FCSTD DOCUMENT  (FreeCAD 0.19R24267 +99 (Git))
Label: Pedals
License: All rights reserved
LicenseURL: http://en.wikipedia.org/wiki/All_rights_reserved
objects: Part::Feature×135, TechDraw::DrawViewDimension×109, TechDraw::DrawProjGroupItem×35, Sketcher::SketchObject×29, PartDesign::Body×19, PartDesign::Pad×16, TechDraw::DrawProjGroup×16, PartDesign::Pocket×13, TechDraw::DrawViewAnnotation×13, Part::FeaturePython×11, TechDraw::DrawSVGTemplate×7, TechDraw::DrawPage×7, App::Part×6, PartDesign::Draft×3, PartDesign::FeatureBase×3, PartDesign::Chamfer×2, TechDraw::DrawViewSection×2, App::DocumentObjectGroup×2, PartDesign::Thickness×1, TechDraw::DrawViewDetail×1
note: 267 computed .brp shape members not serialized (recipe doc carries the construction recipe); baked Part::Feature solids carry a one-line shape summary decoded from their .brp

FEATURE [Sketcher::SketchObject] Sketch
  FullyConstrained = true
  MapMode = 5
  Support = -> [XY_Plane008]
  sketch-geometry (12):
    g0: LineSegment StartX=-14 StartY=10 StartZ=0 EndX=14 EndY=10 EndZ=0
    g1: LineSegment StartX=14 StartY=10 StartZ=0 EndX=14 EndY=-10 EndZ=0
    g2: LineSegment StartX=14 StartY=-10 StartZ=0 EndX=-14 EndY=-10 EndZ=0
    g3: LineSegment StartX=-14 StartY=-10 StartZ=0 EndX=-14 EndY=10 EndZ=0
    g4: LineSegment StartX=-13 StartY=9 StartZ=0 EndX=13 EndY=9 EndZ=0
    g5: LineSegment StartX=13 StartY=9 StartZ=0 EndX=13 EndY=-9 EndZ=0
    g6: LineSegment StartX=13 StartY=-9 StartZ=0 EndX=-13 EndY=-9 EndZ=0
    g7: LineSegment StartX=-13 StartY=-9 StartZ=0 EndX=-13 EndY=9 EndZ=0
    g8: LineSegment StartX=-13 StartY=10 StartZ=0 EndX=-13 EndY=-9 EndZ=0
    g9: LineSegment StartX=13 StartY=10 StartZ=0 EndX=13 EndY=-9 EndZ=0
    g10: LineSegment StartX=-14 StartY=10 StartZ=0 EndX=-13 EndY=10 EndZ=0
    g11: LineSegment StartX=13 StartY=10 StartZ=0 EndX=14 EndY=10 EndZ=0
  constraints (32):
    c: Coincident(g0,g1)
    c: Coincident(g1,g2)
    c: Coincident(g2,g3)
    c: Coincident(g3,g0)
    c: Horizontal(g0)
    c: Horizontal(g2)
    c: Vertical(g1)
    c: Vertical(g3)
    c: Symmetric(g0,g2,g-1)
    c: DistanceY(g3,g3) = 20
    c: DistanceX(g2,g2) = 28
    c: Coincident(g4,g5)
    c: Coincident(g5,g6)
    c: Coincident(g6,g7)
    c: Coincident(g7,g4)
    c: Horizontal(g4)
    c: Horizontal(g6)
    c: Vertical(g5)
    c: Vertical(g7)
    c: DistanceY(g4,g3) = 1
    c: DistanceX(g3,g4) = 1
    c: Symmetric(g4,g6,g-1)
    c: PointOnObject(g8,g0)
    c: Coincident(g8,g6)
    c: Vertical(g8)
    c: PointOnObject(g9,g0)
    c: Coincident(g9,g5)
    c: Vertical(g9)
    c: Coincident(g10,g3)
    c: Coincident(g10,g8)
    c: Coincident(g11,g9)
    c: Coincident(g11,g1)
FEATURE [PartDesign::Pad] Pad
  Direction = (1,1,1)
  Length = 180
  Length2 = 100
  Profile = -> Sketch
  Type = 0
FEATURE [Sketcher::SketchObject] Sketch001
  FullyConstrained = true
  MapMode = 5
  Support = -> [XY_Plane009]
  sketch-geometry (12):
    g0: LineSegment StartX=-15 StartY=10 StartZ=0 EndX=15 EndY=10 EndZ=0
    g1: LineSegment StartX=15 StartY=10 StartZ=0 EndX=15 EndY=-10 EndZ=0
    g2: LineSegment StartX=15 StartY=-10 StartZ=0 EndX=-15 EndY=-10 EndZ=0
    g3: LineSegment StartX=-15 StartY=-10 StartZ=0 EndX=-15 EndY=10 EndZ=0
    g4: LineSegment StartX=-14 StartY=9 StartZ=0 EndX=14 EndY=9 EndZ=0
    g5: LineSegment StartX=14 StartY=9 StartZ=0 EndX=14 EndY=-9 EndZ=0
    g6: LineSegment StartX=14 StartY=-9 StartZ=0 EndX=-14 EndY=-9 EndZ=0
    g7: LineSegment StartX=-14 StartY=-9 StartZ=0 EndX=-14 EndY=9 EndZ=0
    g8: LineSegment StartX=-14 StartY=10 StartZ=0 EndX=-14 EndY=-9 EndZ=0
    g9: LineSegment StartX=14 StartY=10 StartZ=0 EndX=14 EndY=-9 EndZ=0
    g10: LineSegment StartX=-15 StartY=10 StartZ=0 EndX=-14 EndY=10 EndZ=0
    g11: LineSegment StartX=14 StartY=10 StartZ=0 EndX=15 EndY=10 EndZ=0
  constraints (32):
    c: Coincident(g0,g1)
    c: Coincident(g1,g2)
    c: Coincident(g2,g3)
    c: Coincident(g3,g0)
    c: Horizontal(g0)
    c: Horizontal(g2)
    c: Vertical(g1)
    c: Vertical(g3)
    c: Symmetric(g0,g2,g-1)
    c: DistanceY(g3,g3) = 20
    c: DistanceX(g2,g2) = 30
    c: Coincident(g4,g5)
    c: Coincident(g5,g6)
    c: Coincident(g6,g7)
    c: Coincident(g7,g4)
    c: Horizontal(g4)
    c: Horizontal(g6)
    c: Vertical(g5)
    c: Vertical(g7)
    c: DistanceY(g4,g3) = 1
    c: DistanceX(g3,g4) = 1
    c: Symmetric(g4,g6,g-1)
    c: PointOnObject(g8,g0)
    c: Coincident(g8,g6)
    c: Vertical(g8)
    c: PointOnObject(g9,g0)
    c: Coincident(g9,g5)
    c: Vertical(g9)
    c: Coincident(g10,g3)
    c: Coincident(g10,g8)
    c: Coincident(g11,g9)
    c: Coincident(g11,g1)
FEATURE [PartDesign::Pad] Pad001
  Direction = (1,1,1)
  Length = 240
  Length2 = 100
  Offset = -10
  Profile = -> Sketch001
  Type = 0
FEATURE [Sketcher::SketchObject] Sketch002
  ExternalGeometry = -> [Pad001]
  FullyConstrained = true
  MapMode = 5
  Placement = pos=(15,0,0) rot=(0.57735,0.57735,0.57735;2.0944rad)
  Support = -> [Pad001]
  sketch-geometry (3):
    g0: LineSegment StartX=0 StartY=240 StartZ=0 EndX=0 EndY=0 EndZ=0
    g1: Circle CenterX=0 CenterY=190 CenterZ=0 NormalX=0 NormalY=0 NormalZ=1 AngleXU=0 Radius=3
    g2: Circle CenterX=4e-16 CenterY=25 CenterZ=0 NormalX=0 NormalY=0 NormalZ=1 AngleXU=0 Radius=3
  constraints (10):
    c: PointOnObject(g0,g-4)
    c: Coincident(g0,g-1)
    c: Vertical(g0)
    c: PointOnObject(g1,g0)
    c: Diameter(g1) = 6
    c: Distance(g1,g0) = 50
    c: Distance(g-4) = 20
    c: Diameter(g2) = 6
    c: Distance(g2,g1) = 165
    c: Distance(g2,g-5) = 10
FEATURE [PartDesign::Pocket] Pocket
  BaseFeature = -> Pad001
  Length = 5
  Length2 = 100
  Profile = -> Sketch002
  Type = 1
FEATURE [Sketcher::SketchObject] Sketch003
  ExternalGeometry = -> [Pad]
  FullyConstrained = false
  MapMode = 5
  Placement = pos=(14,0,0) rot=(0.57735,0.57735,0.57735;2.0944rad)
  Support = -> [Pad]
  sketch-geometry (8):
    g0: LineSegment StartX=0 StartY=180 StartZ=0 EndX=0 EndY=0 EndZ=0
    g1: Circle CenterX=0 CenterY=10 CenterZ=0 NormalX=0 NormalY=0 NormalZ=1 AngleXU=0 Radius=3
    g2: Circle CenterX=4e-16 CenterY=80 CenterZ=0 NormalX=0 NormalY=0 NormalZ=1 AngleXU=0 Radius=3
    g3: LineSegment StartX=4e-16 StartY=80 StartZ=0 EndX=4e-16 EndY=120.768 EndZ=0
    g4: Circle CenterX=4e-16 CenterY=90 CenterZ=0 NormalX=0 NormalY=0 NormalZ=1 AngleXU=0 Radius=3
    g5: Circle CenterX=4e-16 CenterY=100 CenterZ=0 NormalX=0 NormalY=0 NormalZ=1 AngleXU=0 Radius=3
    g6: Circle CenterX=4e-16 CenterY=110 CenterZ=0 NormalX=0 NormalY=0 NormalZ=1 AngleXU=0 Radius=3
    g7: Circle CenterX=0 CenterY=60 CenterZ=0 NormalX=0 NormalY=0 NormalZ=1 AngleXU=0 Radius=2
  constraints (23):
    c: PointOnObject(g0,g-5)
    c: Coincident(g0,g-1)
    c: Vertical(g0)
    c: PointOnObject(g1,g0)
    c: Diameter(g1) = 6
    c: DistanceY(g-1,g1) = 10
    c: Diameter(g2) = 6
    c: Distance(g2,g-4) = 10
    c: DistanceY(g1,g2) = 70
    c: Coincident(g3,g2)
    c: Vertical(g3)
    c: PointOnObject(g4,g3)
    c: Equal(g4,g5)
    c: Equal(g5,g2)
    c: DistanceY(g2,g4) = 10
    c: DistanceY(g4,g5) = 10
    c: PointOnObject(g5,g3)
    c: PointOnObject(g6,g3)
    c: DistanceY(g5,g6) = 10
    c: Equal(g6,g5)
    c: PointOnObject(g7,g0)
    c: Diameter(g7) = 4
    c: DistanceY(g-6,g7) = 60
FEATURE [PartDesign::Pocket] Pocket001
  BaseFeature = -> Pad
  Length = 5
  Length2 = 100
  Profile = -> Sketch003
  Type = 1
FEATURE [Sketcher::SketchObject] Sketch005
  FullyConstrained = true
  MapMode = 5
  Support = -> [XY_Plane010]
  sketch-geometry (12):
    g0: LineSegment StartX=-14 StartY=12.5 StartZ=0 EndX=14 EndY=12.5 EndZ=0
    g1: LineSegment StartX=14 StartY=12.5 StartZ=0 EndX=14 EndY=-12.5 EndZ=0
    g2: LineSegment StartX=14 StartY=-12.5 StartZ=0 EndX=-14 EndY=-12.5 EndZ=0
    g3: LineSegment StartX=-14 StartY=-12.5 StartZ=0 EndX=-14 EndY=12.5 EndZ=0
    g4: LineSegment StartX=-13 StartY=11.5 StartZ=0 EndX=13 EndY=11.5 EndZ=0
    g5: LineSegment StartX=13 StartY=11.5 StartZ=0 EndX=13 EndY=-11.5 EndZ=0
    g6: LineSegment StartX=13 StartY=-11.5 StartZ=0 EndX=-13 EndY=-11.5 EndZ=0
    g7: LineSegment StartX=-13 StartY=-11.5 StartZ=0 EndX=-13 EndY=11.5 EndZ=0
    g8: LineSegment StartX=-13 StartY=12.5 StartZ=0 EndX=-13 EndY=-11.5 EndZ=0
    g9: LineSegment StartX=13 StartY=12.5 StartZ=0 EndX=13 EndY=-11.5 EndZ=0
    g10: LineSegment StartX=-14 StartY=12.5 StartZ=0 EndX=-13 EndY=12.5 EndZ=0
    g11: LineSegment StartX=13 StartY=12.5 StartZ=0 EndX=14 EndY=12.5 EndZ=0
  constraints (32):
    c: Coincident(g0,g1)
    c: Coincident(g1,g2)
    c: Coincident(g2,g3)
    c: Coincident(g3,g0)
    c: Horizontal(g0)
    c: Horizontal(g2)
    c: Vertical(g1)
    c: Vertical(g3)
    c: Symmetric(g0,g2,g-1)
    c: DistanceY(g3,g3) = 25
    c: DistanceX(g2,g2) = 28
    c: Coincident(g4,g5)
    c: Coincident(g5,g6)
    c: Coincident(g6,g7)
    c: Coincident(g7,g4)
    c: Horizontal(g4)
    c: Horizontal(g6)
    c: Vertical(g5)
    c: Vertical(g7)
    c: DistanceY(g4,g3) = 1
    c: DistanceX(g3,g4) = 1
    c: Symmetric(g4,g6,g-1)
    c: PointOnObject(g8,g0)
    c: Coincident(g8,g6)
    c: Vertical(g8)
    c: PointOnObject(g9,g0)
    c: Coincident(g9,g5)
    c: Vertical(g9)
    c: Coincident(g10,g3)
    c: Coincident(g10,g8)
    c: Coincident(g11,g9)
    c: Coincident(g11,g1)
FEATURE [PartDesign::Pad] Pad002
  Direction = (1,1,1)
  Length = 50
  Length2 = 100
  Profile = -> Sketch005
  Type = 0
FEATURE [PartDesign::Draft] Draft
  Angle = 15
  Base = -> Pad002 [Face9]
  BaseFeature = -> Pad002
  SupportTransform = false
FEATURE [Sketcher::SketchObject] Sketch006
  FullyConstrained = true
  MapMode = 5
  Placement = pos=(14,0,0) rot=(0.57735,0.57735,0.57735;2.0944rad)
  Support = -> [Draft]
  sketch-geometry (1):
    g0: Circle CenterX=0 CenterY=12 CenterZ=0 NormalX=0 NormalY=0 NormalZ=1 AngleXU=0 Radius=3
  constraints (3):
    c: PointOnObject(g0,g-2)
    c: Diameter(g0) = 6
    c: Distance(g-1,g0) = 12
FEATURE [PartDesign::Pocket] Pocket002
  BaseFeature = -> Draft
  Length = 5
  Length2 = 100
  Profile = -> Sketch006
  Type = 1
FEATURE [PartDesign::Body] _______________________003  label="Упор пружины"
  Group = -> [Sketch005,Pad002,Draft,Sketch006,Pocket002]
  Origin = -> Origin010
  Placement = pos=(0,-13.1352,-2.8136) rot=(-1,0,0;0.523599rad)
  Tip = -> Pocket002
FEATURE [Part::Feature] Part__Feature069  label="01 - Pied"
  Placement = pos=(142.918,-74.3145,196.645) rot=(0,0,1;0rad)
  shape: bbox 314.5 x 48 x 7.5 mm, 33 faces (baked)
FEATURE [Part::Feature] Part__Feature070  label="02 - Pied SYM"
  Placement = pos=(142.918,-74.3145,-127.355) rot=(0,0,1;0rad)
  shape: bbox 314.5 x 48 x 7.5 mm, 33 faces (baked)
FEATURE [Part::Feature] Part__Feature071  label="03 - Equerre fixation sol"
  Placement = pos=(267.668,181.146,167.895) rot=(1,0,0;1.5708rad)
  shape: bbox 65 x 37.5 x 50 mm, 100 faces, 2 solids (baked)
FEATURE [Part::Feature] Part__Feature072  label="04 - Equerre fixation sol SYM"
  Placement = pos=(267.668,181.146,-56.1054) rot=(1,0,0;1.5708rad)
  shape: bbox 65 x 37.5 x 50 mm, 100 faces, 2 solids (baked)
FEATURE [Part::Feature] Part__Feature073  label="05 - Equerre fixation sol 2"
  Placement = pos=(19.4178,179.899,167.895) rot=(1,0,0;1.5708rad)
  shape: bbox 65 x 27 x 50 mm, 97 faces, 2 solids (baked)
FEATURE [Part::Feature] Part__Feature074  label="06 - Equerre fixation sol 2 SYM"
  Placement = pos=(19.4178,179.899,-56.1054) rot=(1,0,0;1.5708rad)
  shape: bbox 65 x 27 x 50 mm, 97 faces, 2 solids (baked)
FEATURE [Part::Feature] Part__Feature075  label="07 - Axe court"
  Placement = pos=(288.168,200.646,30.8946) rot=(0,0,1;0rad)
  shape: bbox 17.32 x 17.32 x 316 mm, 29 faces (baked)
FEATURE [Part::Feature] Part__Feature076  label="07 - Axe court001"
  Placement = pos=(25.9178,189.899,30.8946) rot=(0,0,1;0rad)
  shape: bbox 17.32 x 17.32 x 316 mm, 29 faces (baked)
FEATURE [Part::Feature] Part__Feature077  label="08 - Axe long"
  Placement = pos=(130.86,215.417,30.8946) rot=(0,0,1;0rad)
  shape: bbox 17.32 x 17.32 x 324 mm, 29 faces (baked)
FEATURE [Part::Feature] Part__Feature078  label="09 - Levier pedales A-E"
  Placement = pos=(178.538,257.451,148.595) rot=(-0.810568,-0.414113,0.414113;1.77929rad)
  shape: bbox 94.99 x 131.6 x 40 mm, 76 faces (baked)
FEATURE [Part::Feature] Part__Feature079  label="10 - Levier pedales F"
  Placement = pos=(178.562,257.423,34.9946) rot=(-0.810765,-0.41392,0.41392;1.77905rad)
  shape: bbox 95.05 x 131.5 x 40 mm, 78 faces (baked)
FEATURE [Part::Feature] Part__Feature080  label="09 - Levier pedales A-E001"
  Placement = pos=(178.485,257.51,-86.3054) rot=(-0.810139,-0.414533,0.414533;1.77981rad)
  shape: bbox 94.85 x 131.7 x 40 mm, 76 faces (baked)
FEATURE [Part::Feature] Part__Feature081  label="11 - Palier bronze"
  Placement = pos=(130.86,215.417,14.1946) rot=(-0.439546,-0.783326,-0.439546;1.81261rad)
  shape: bbox 24 x 24 x 8.6 mm, 9 faces (baked)
FEATURE [Part::Feature] Part__Feature082  label="11 - Palier bronze001"
  Placement = pos=(130.86,215.417,55.7946) rot=(0.439546,0.783326,-0.439546;1.81261rad)
  shape: bbox 24 x 24 x 8.6 mm, 9 faces (baked)
FEATURE [Part::Feature] Part__Feature083  label="11 - Palier bronze002"
  Placement = pos=(130.86,215.417,127.795) rot=(-0.423866,-0.800422,-0.423866;1.7916rad)
  shape: bbox 24 x 24 x 8.6 mm, 9 faces (baked)
FEATURE [Part::Feature] Part__Feature084  label="11 - Palier bronze003"
  Placement = pos=(130.86,215.417,169.395) rot=(0.423866,0.800422,-0.423866;1.7916rad)
  shape: bbox 24 x 24 x 8.6 mm, 9 faces (baked)
FEATURE [Part::Feature] Part__Feature085  label="11 - Palier bronze004"
  Placement = pos=(130.86,215.417,-107.105) rot=(0.078533,-0.993814,0.078533;1.577rad)
  shape: bbox 24 x 24 x 8.6 mm, 9 faces (baked)
FEATURE [Part::Feature] Part__Feature086  label="11 - Palier bronze005"
  Placement = pos=(130.86,215.417,-65.5054) rot=(-0.078533,0.993814,0.078533;1.577rad)
  shape: bbox 24 x 24 x 8.6 mm, 9 faces (baked)
FEATURE [Part::Feature] Part__Feature087  label="12 - Pivot suspension"
  Placement = pos=(175.936,282.783,11.9946) rot=(0.308259,0.951303,0;3.14159rad)
  shape: bbox 11.55 x 11.55 x 20.5 mm, 28 faces (baked)
FEATURE [Part::Feature] Part__Feature088  label="13 - Ecrou suspension"
  Placement = pos=(175.936,282.783,-2.00541) rot=(0,0,1;0rad)
  shape: bbox 11 x 11 x 4.5 mm, 10 faces (baked)
FEATURE [Part::Feature] Part__Feature089  label="14 - Amortisseur"
  Placement = pos=(270.501,227.576,5.49459) rot=(0.252673,0.933977,-0.252673;1.63905rad)
  shape: bbox 118.3 x 72.79 x 31.6 mm, 228 faces, 4 solids (baked)
FEATURE [Part::Feature] Part__Feature090  label="15 - Pivot levier"
  Placement = pos=(159.004,251.963,34.9946) rot=(0,0,1;1.19261rad)
  shape: bbox 22.9 x 24.48 x 31.5 mm, 28 faces (baked)
FEATURE [Part::Feature] Part__Feature091  label="16 - Coulisseau frein"
  Placement = pos=(224.058,226.117,34.9946) rot=(-0.054456,0.010422,-0.998462;0.378751rad)
  shape: bbox 68.35 x 35.6 x 12.99 mm, 11 faces (baked)
FEATURE [Part::Feature] Part__Feature092  label="17 - Axe nu"
  Placement = pos=(154.822,253.625,34.9946) rot=(0,0,-1;0.378182rad)
  shape: bbox 8.047 x 8.047 x 40 mm, 8 faces (baked)
FEATURE [Part::Feature] Part__Feature093  label="18 - Vibreur"
  Placement = pos=(189.956,293.62,34.9946) rot=(-0.665096,-0.339551,0.665096;3.79627rad)
  shape: bbox 30.23 x 46.77 x 28 mm, 137 faces, 6 solids (baked)
FEATURE [Part::Feature] Part__Feature094  label="15 - Pivot levier001"
  Placement = pos=(158.736,251.576,-86.3054) rot=(0,0,1;1.08724rad)
  shape: bbox 23.66 x 24.93 x 31.5 mm, 28 faces (baked)
FEATURE [Part::Feature] Part__Feature095  label="19 - Axe capteur"
  Placement = pos=(154.752,253.668,-86.3054) rot=(-0.15035,0.988633,0;3.14159rad)
  shape: bbox 8.63 x 8.268 x 40 mm, 18 faces, 2 solids (baked)
FEATURE [Part::Feature] Part__Feature096  label="20 - Coulisseau embrayage"
  Placement = pos=(234.876,211.592,-86.3054) rot=(0,0,-1;0.483554rad)
  shape: bbox 79.02 x 47.64 x 10.82 mm, 11 faces (baked)
FEATURE [Part::Feature] Part__Feature097  label="21 - Ressort embrayage"
  Placement = pos=(215.93,221.542,-86.3054) rot=(0,0,1;1.08724rad)
  shape: bbox 47.07 x 34.38 x 15.81 mm, 3 faces (baked)
FEATURE [Part::Feature] Part__Feature098  label="15 - Pivot levier002"
  Placement = pos=(179.773,280.728,-86.3054) rot=(-0.512361,0.85877,0;3.14159rad)
  shape: bbox 23.74 x 23.74 x 31.5 mm, 28 faces (baked)
FEATURE [Part::Feature] Part__Feature099  label="17 - Axe nu001"
  Placement = pos=(175.813,282.865,-86.3054) rot=(0,0,1;1.06237rad)
  shape: bbox 8.329 x 8.329 x 40 mm, 8 faces (baked)
FEATURE [Part::Feature] Part__Feature100  label="22 - Biellette embrayage"
  Placement = pos=(223.773,256.979,-86.3054) rot=(0,0,-1;0.494932rad)
  shape: bbox 91.8 x 55.35 x 10 mm, 28 faces (baked)
FEATURE [Part::Feature] Part__Feature101  label="24 - Guide coulisseau taraud澀"
  Placement = pos=(269.394,193.466,-86.3054) rot=(0,0,1;2.65804rad)
  shape: bbox 66.88 x 46.28 x 30 mm, 19 faces (baked)
FEATURE [Part::Feature] Part__Feature102  label="25 - Tampon embrayage"
  Placement = pos=(249.409,223.162,-86.3054) rot=(-0.650221,-0.392969,0.650221;3.89045rad)
  shape: bbox 38.38 x 29.13 x 18 mm, 16 faces (baked)
FEATURE [Part::Feature] Part__Feature103  label="26 - Axe 12mm"
  Placement = pos=(269.394,193.466,-86.3054) rot=(0,0,-1;0rad)
  shape: bbox 12 x 12 x 32 mm, 12 faces (baked)
FEATURE [Part::Feature] Part__Feature104  label="27 - Axe 8mm"
  Placement = pos=(271.733,231.093,-86.3054) rot=(0,0,-1;0rad)
  shape: bbox 8 x 8 x 52 mm, 14 faces (baked)
FEATURE [Part::Feature] Part__Feature105  label="28 - Pivot renvoi"
  Placement = pos=(288.168,200.646,-106.305) rot=(0,0,-1;1.55065rad)
  shape: bbox 38.57 x 52.92 x 4 mm, 15 faces (baked)
FEATURE [Part::Feature] Part__Feature106  label="28 - Pivot renvoi001"
  Placement = pos=(288.168,200.646,-70.3054) rot=(0,0,-1;1.55065rad)
  shape: bbox 38.57 x 52.92 x 4 mm, 15 faces (baked)
FEATURE [Part::Feature] Part__Feature107  label="11 - Palier bronze006"
  Placement = pos=(288.168,200.646,-107.105) rot=(-0.279247,-0.918718,-0.279247;1.65547rad)
  shape: bbox 24 x 24 x 8.6 mm, 9 faces (baked)
FEATURE [Part::Feature] Part__Feature108  label="11 - Palier bronze007"
  Placement = pos=(288.168,200.646,-65.5054) rot=(-0.327241,0.886469,0.327241;1.69101rad)
  shape: bbox 24 x 24 x 8.6 mm, 9 faces (baked)
FEATURE [Part::Feature] Part__Feature109  label="15 - Pivot levier003"
  Placement = pos=(267.773,233.231,-86.3054) rot=(0,0,-1;2.06573rad)
  shape: bbox 23.74 x 24.96 x 31.5 mm, 28 faces (baked)
FEATURE [Part::Feature] Part__Feature110  label="29 - Entretoise_20"
  Placement = pos=(288.168,200.646,-117.105) rot=(0,0,1;0rad)
  shape: bbox 20 x 20 x 20 mm, 6 faces (baked)
FEATURE [Part::Feature] Part__Feature111  label="29 - Entretoise_23.5"
  Placement = pos=(130.86,215.417,-119.355) rot=(0,0,1;0rad)
  shape: bbox 20 x 20 x 23.5 mm, 6 faces (baked)
FEATURE [Part::Feature] Part__Feature112  label="30 - Pousseur mousse"
  Placement = pos=(260.07,211.809,34.9946) rot=(-0.300774,-0.951003,-0.07162;1.57595rad)
  shape: bbox 25.55 x 19.19 x 12.11 mm, 8 faces (baked)
FEATURE [Part::Feature] Part__Feature113  label="31 - Mousse loadcell"
  Placement = pos=(236.604,221.132,34.9946) rot=(-0.353533,-0.935271,-0.01678;1.57108rad)
  shape: bbox 29.34 x 20.66 x 11.5 mm, 4 faces (baked)
FEATURE [Part::Feature] Part__Feature114  label="32 - Guide coulisseau frein"
  Placement = pos=(288.168,200.646,34.9946) rot=(0,0,1;2.76341rad)
  shape: bbox 109.8 x 58.06 x 41.6 mm, 35 faces (baked)
FEATURE [Part::Feature] Part__Feature115  label="33 - Entretoise pedale"
  Placement = pos=(197.009,334.183,148.595) rot=(-0.454956,0.890514,0;3.14159rad)
  shape: bbox 31.86 x 39.29 x 31.5 mm, 10 faces (baked)
FEATURE [Part::Feature] Part__Feature116  label="33 - Entretoise pedale001"
  Placement = pos=(197.077,334.145,34.9946) rot=(-0.454701,0.890644,0;3.14159rad)
  shape: bbox 31.87 x 39.29 x 31.5 mm, 10 faces (baked)
FEATURE [Part::Feature] Part__Feature117  label="33 - Entretoise pedale002"
  Placement = pos=(196.86,334.266,-86.3054) rot=(-0.455514,0.890229,0;3.14159rad)
  shape: bbox 31.83 x 39.31 x 31.5 mm, 10 faces (baked)
FEATURE [Part::Feature] Part__Feature118  label="34 - Patte suspension"
  Placement = pos=(209.515,208.042,0.494593) rot=(0,0,-1;0.09377rad)
  shape: bbox 179.3 x 36.8 x 12 mm, 37 faces, 3 solids (baked)
FEATURE [Part::Feature] Part__Feature119  label="29 - Entretoise_10"
  Placement = pos=(130.86,215.417,8.84459) rot=(0,0,1;0.052395rad)
  shape: bbox 20 x 20 x 10.7 mm, 6 faces (baked)
FEATURE [Part::Feature] Part__Feature120  label="29 - Entretoise_021"
  Placement = pos=(288.168,200.646,8.84459) rot=(0,0,1;2.89054rad)
  shape: bbox 20 x 20 x 10.7 mm, 6 faces (baked)
FEATURE [Part::Feature] Part__Feature121  label="29 - Entretoise_66"
  Placement = pos=(288.168,200.646,-32.5054) rot=(0,0,1;0rad)
  shape: bbox 20 x 20 x 66 mm, 6 faces (baked)
FEATURE [Part::Feature] Part__Feature122  label="29 - Entretoise_022"
  Placement = pos=(130.86,215.417,-32.5054) rot=(0,0,1;0rad)
  shape: bbox 20 x 20 x 66 mm, 6 faces (baked)
FEATURE [Part::Feature] Part__Feature123  label="35 - Patte potentiometre"
  Placement = pos=(243.331,193.814,0.494593) rot=(0.046816,0.997806,-0.046816;1.57299rad)
  shape: bbox 26.1 x 27.01 x 43 mm, 70 faces, 2 solids (baked)
FEATURE [Part::Feature] Part__Feature124  label="36 - Loadcell"
  Placement = pos=(267.945,193.078,34.9946) rot=(0.184731,0.965271,-0.184731;1.60614rad)
  shape: bbox 14.62 x 32.34 x 34 mm, 103 faces, 6 solids (baked)
FEATURE [Part::Feature] Part__Feature125  label="23 - Guide coulisseau simple"
  Placement = pos=(288.168,200.646,148.795) rot=(0,0,1;2.76338rad)
  shape: bbox 68.52 x 41.08 x 30 mm, 14 faces (baked)
FEATURE [Part::Feature] Part__Feature126  label="29 - Entretoise_78"
  Placement = pos=(288.168,200.646,94.7946) rot=(0,0,1;0.293677rad)
  shape: bbox 20 x 20 x 78 mm, 6 faces (baked)
FEATURE [Part::Feature] Part__Feature127  label="29 - Entretoise_72"
  Placement = pos=(130.86,215.417,91.7946) rot=(0,0,1;0.075049rad)
  shape: bbox 20 x 20 x 72 mm, 6 faces (baked)
FEATURE [Part::Feature] Part__Feature128  label="29 - Entretoise_25.1"
  Placement = pos=(288.168,200.646,176.345) rot=(0,0,1;0.075049rad)
  shape: bbox 20 x 20 x 25.1 mm, 6 faces (baked)
FEATURE [Part::Feature] Part__Feature129  label="29 - Entretoise_23.006"
  Placement = pos=(130.86,215.417,181.145) rot=(0,0,1;0rad)
  shape: bbox 20 x 20 x 23.5 mm, 6 faces (baked)
FEATURE [Part::Feature] Part__Feature130  label="37 - Repose pied"
  Placement = pos=(-22.9077,203.899,-131.105) rot=(0,0,1;0rad)
  shape: bbox 131.2 x 22.09 x 324 mm, 68 faces (baked)
FEATURE [Part::Feature] Part__Feature131  label="38 - Pedale F-E"
  Placement = pos=(153.634,292.994,34.9946) rot=(-0.262805,-0.928368,-0.262805;1.64505rad)
  shape: bbox 45.41 x 71.46 x 124.8 mm, 68 faces (baked)
FEATURE [Part::Feature] Part__Feature132  label="38 - Pedale F-E001"
  Placement = pos=(153.493,293.035,-86.3054) rot=(-0.262016,-0.928814,-0.262016;1.64458rad)
  shape: bbox 45.29 x 71.54 x 124.8 mm, 68 faces (baked)
FEATURE [Part::Feature] Part__Feature133  label="39 - Coulisseau accelerateur"
  Placement = pos=(251.915,215.05,148.795) rot=(-0.933244,0.178618,-0.31169;1.10138rad)
  shape: bbox 95.77 x 45.52 x 10.47 mm, 11 faces (baked)
FEATURE [Part::Feature] Part__Feature134  label="40 - Pivot levier carre"
  Placement = pos=(158.982,251.977,148.795) rot=(-0.561577,0.827424,0;3.14159rad)
  shape: bbox 24.13 x 23.39 x 31.5 mm, 16 faces (baked)
FEATURE [Part::Feature] Part__Feature135  label="19 - Axe capteur001"
  Placement = pos=(154.8,253.638,148.595) rot=(-0.202188,0.979347,0;3.14159rad)
  shape: bbox 8.657 x 8.048 x 40 mm, 18 faces, 2 solids (baked)
FEATURE [Part::Feature] Part__Feature136  label="41 - Ressort accelerateur"
  Placement = pos=(234.267,222.063,148.795) rot=(0,0,1;1.19258rad)
  shape: bbox 63.36 x 38.44 x 16 mm, 4 faces (baked)
FEATURE [Part::Feature] Part__Feature137  label="43 - Barre transversale"
  Placement = pos=(106.184,207.434,30.8946) rot=(0,0,1;0.785398rad)
  shape: bbox 21.8 x 21.8 x 330 mm, 30 faces (baked)
FEATURE [Part::Feature] Part__Feature138  label="44 - Pedale A"
  Placement = pos=(116.87,227.059,89.5959) rot=(-0.249406,-0.935747,-0.249348;1.63705rad)
  shape: bbox 92.07 x 154 x 85.4 mm, 37 faces (baked)
FEATURE [Part::Feature] Part__Feature139  label="45 - Goupille"
  Placement = pos=(275.569,217.68,8.49459) rot=(0.956256,0.292532,0;3.14159rad)
  shape: bbox 17.7 x 11.96 x 1 mm, 22 faces (baked)
FEATURE [Part::Feature] Part__Feature140  label="46 - Support controleur"
  Placement = pos=(22.174,181.696,-35.3554) rot=(0,0,1;0.069813rad)
  shape: bbox 94.97 x 25.82 x 76 mm, 39 faces (baked)
FEATURE [Part::Feature] Part__Feature141  label="47 - Entretoise capteur"
  Placement = pos=(143.992,254.051,168.595) rot=(0,0,1;0rad)
  shape: bbox 5.5 x 5.5 x 3 mm, 6 faces (baked)
FEATURE [Part::Feature] Part__Feature142  label="47 - Entretoise capteur001"
  Placement = pos=(136.959,244.327,168.595) rot=(0,0,1;0rad)
  shape: bbox 5.5 x 5.5 x 3 mm, 6 faces (baked)
FEATURE [Part::Feature] Part__Feature143  label="47 - Entretoise capteur002"
  Placement = pos=(153.44,239.813,168.595) rot=(0,0,1;0rad)
  shape: bbox 5.5 x 5.5 x 3 mm, 6 faces (baked)
FEATURE [Part::Feature] Part__Feature144  label="47 - Entretoise capteur003"
  Placement = pos=(143.943,254.067,-66.3054) rot=(0,0,1;0rad)
  shape: bbox 5.5 x 5.5 x 3 mm, 6 faces (baked)
FEATURE [Part::Feature] Part__Feature145  label="47 - Entretoise capteur004"
  Placement = pos=(136.923,244.335,-66.3054) rot=(0,0,1;0rad)
  shape: bbox 5.5 x 5.5 x 3 mm, 6 faces (baked)
FEATURE [Part::Feature] Part__Feature146  label="47 - Entretoise capteur005"
  Placement = pos=(153.409,239.841,-66.3054) rot=(0,0,1;0rad)
  shape: bbox 5.5 x 5.5 x 3 mm, 6 faces (baked)
FEATURE [Part::Feature] Part__Feature147  label="48 - Capteur hall"
  Placement = pos=(147.725,246.414,171.595) rot=(0,0,1;0.944646rad)
  shape: bbox 30.49 x 30.94 x 9.5 mm, 66 faces, 4 solids (baked)
FEATURE [Part::Feature] Part__Feature148  label="48 - Capteur hall001"
  Placement = pos=(147.686,246.436,-63.3054) rot=(0,0,1;0.945899rad)
  shape: bbox 30.49 x 30.94 x 9.5 mm, 66 faces, 4 solids (baked)
FEATURE [Part::Feature] Part__Feature149  label="49 - Potentiometre"
  Placement = pos=(254.837,215.331,-32.7579) rot=(0.749807,0.432461,-0.500767;1.91208rad)
  shape: bbox 16.61 x 27.96 x 16.24 mm, 45 faces, 4 solids (baked)
FEATURE [Part::Feature] Part__Feature150  label="48 - Capteur hall002"
  Placement = pos=(256.308,203.642,-4.00541) rot=(0.046868,0.998901,0;3.14159rad)
  shape: bbox 24.87 x 23.06 x 9.5 mm, 66 faces, 4 solids (baked)
FEATURE [Part::Feature] Part__Feature151  label="47 - Entretoise capteur006"
  Placement = pos=(257.504,194.992,-4.00541) rot=(0,0,1;0rad)
  shape: bbox 5.5 x 5.5 x 3 mm, 6 faces (baked)
FEATURE [Part::Feature] Part__Feature152  label="47 - Entretoise capteur007"
  Placement = pos=(264.975,210.36,-4.00541) rot=(0,0,1;0rad)
  shape: bbox 5.5 x 5.5 x 3 mm, 6 faces (baked)
FEATURE [Part::Feature] Part__Feature153  label="47 - Entretoise capteur008"
  Placement = pos=(253.028,211.483,-4.00541) rot=(0,0,1;0rad)
  shape: bbox 5.5 x 5.5 x 3 mm, 6 faces (baked)
FEATURE [Part::Feature] Part__Feature154  label="Vis FHc_vis F HC M 6 X  25"
  Placement = pos=(176.745,337.732,148.595) rot=(0.812452,0.173613,0.556579;2.03623rad)
  shape: bbox 27.71 x 23.3 x 11.3 mm, 17 faces (baked)
FEATURE [Part::Feature] Part__Feature155  label="Vis FHc_vis F HC M 6 X  026"
  Placement = pos=(167.168,322.443,148.595) rot=(0.812452,0.173613,0.556579;2.03623rad)
  shape: bbox 27.71 x 23.3 x 11.3 mm, 17 faces (baked)
FEATURE [Part::Feature] Part__Feature156  label="Vis FHc_vis F HC M 6 X  027"
  Placement = pos=(167.845,321.904,-86.3054) rot=(0.726221,0.656145,0.205128;1.61474rad)
  shape: bbox 27.72 x 23.28 x 11.3 mm, 17 faces (baked)
FEATURE [Part::Feature] Part__Feature157  label="Vis FHc_vis F HC M 6 X  028"
  Placement = pos=(177.301,337.353,34.9946) rot=(0.72695,0.655599,0.20429;1.61436rad)
  shape: bbox 27.7 x 23.31 x 11.3 mm, 17 faces (baked)
FEATURE [Part::Feature] Part__Feature158  label="Vis FHc_vis F HC M 6 X  029"
  Placement = pos=(168.04,321.836,34.9946) rot=(0.72695,0.655599,0.20429;1.61436rad)
  shape: bbox 27.7 x 23.31 x 11.3 mm, 17 faces (baked)
FEATURE [Part::Feature] Part__Feature159  label="Ecrou Hm_Ecrou H M 10"
  Placement = pos=(172.017,244.602,-86.3054) rot=(-0.482464,-0.875687,0.020017;1.5712rad)
  shape: bbox 12.43 x 18.38 x 18.48 mm, 22 faces (baked)
FEATURE [Part::Feature] Part__Feature160  label="Ecrou Hm_Ecrou H M 011"
  Placement = pos=(176.443,242.278,-86.3054) rot=(-0.471392,-0.881893,0.007329;1.57085rad)
  shape: bbox 12.43 x 18.38 x 18.48 mm, 22 faces (baked)
FEATURE [Part::Feature] Part__Feature161  label="Ecrou Hm_Ecrou H M 012"
  Placement = pos=(172.922,246.438,148.795) rot=(-0.434637,-0.897688,0.072437;1.57607rad)
  shape: bbox 10.85 x 18.77 x 18.48 mm, 22 faces (baked)
FEATURE [Part::Feature] Part__Feature162  label="Ecrou Hm_Ecrou H M 013"
  Placement = pos=(177.569,244.591,148.795) rot=(-0.434637,-0.897688,0.072437;1.57607rad)
  shape: bbox 10.85 x 18.77 x 18.48 mm, 22 faces (baked)
FEATURE [Part::Feature] Part__Feature163  label="Vis FHc_vis F HC M 8 X  12"
  Placement = pos=(259.918,189.899,-138.605) rot=(0,0,1;0rad)
  shape: bbox 15.8 x 15.8 x 16.65 mm, 17 faces (baked)
FEATURE [Part::Feature] Part__Feature164  label="Vis FHc_vis F HC M 8 X  013"
  Placement = pos=(130.86,215.417,-138.605) rot=(0,0,1;0rad)
  shape: bbox 15.8 x 15.8 x 16.65 mm, 17 faces (baked)
FEATURE [Part::Feature] Part__Feature165  label="Vis FHc_vis F HC M 8 X  014"
  Placement = pos=(25.9178,189.899,-138.605) rot=(0,0,1;0rad)
  shape: bbox 15.8 x 15.8 x 16.65 mm, 17 faces (baked)
FEATURE [Part::Feature] Part__Feature166  label="Vis FHc_vis F HC M 8 X  015"
  Placement = pos=(288.168,200.646,-131.105) rot=(0,0,1;0rad)
  shape: bbox 15.8 x 15.8 x 16.65 mm, 17 faces (baked)
FEATURE [Part::Feature] Part__Feature167  label="Vis FHc_vis F HC M 8 X  016"
  Placement = pos=(25.9178,189.899,200.395) rot=(-0.195284,0.980747,0;3.14159rad)
  shape: bbox 15.8 x 15.8 x 16.65 mm, 17 faces (baked)
FEATURE [Part::Feature] Part__Feature168  label="Vis FHc_vis F HC M 8 X  017"
  Placement = pos=(130.86,215.417,200.395) rot=(0.289642,0.957135,0;3.14159rad)
  shape: bbox 15.8 x 15.8 x 16.65 mm, 17 faces (baked)
FEATURE [Part::Feature] Part__Feature169  label="Vis FHc_vis F HC M 8 X  018"
  Placement = pos=(259.918,189.899,200.395) rot=(0.212648,0.977129,0;3.14159rad)
  shape: bbox 15.8 x 15.8 x 16.65 mm, 17 faces (baked)
FEATURE [Part::Feature] Part__Feature170  label="Vis FHc_vis F HC M 8 X  019"
  Placement = pos=(288.168,200.646,192.895) rot=(0.598305,0.801268,0;3.14159rad)
  shape: bbox 15.8 x 15.8 x 16.65 mm, 17 faces (baked)
FEATURE [Part::Feature] Part__Feature171  label="Ecrou Hm_Ecrou H M  4"
  Placement = pos=(271.733,231.093,-108.305) rot=(0,0,1;0rad)
  shape: bbox 8.084 x 8.084 x 2.001 mm, 22 faces (baked)
FEATURE [Part::Feature] Part__Feature172  label="Ecrou Hm_Ecrou H M  005"
  Placement = pos=(271.733,231.093,-110.305) rot=(0,0,1;0rad)
  shape: bbox 8.084 x 8.084 x 2.001 mm, 22 faces (baked)
FEATURE [Part::Feature] Part__Feature173  label="Ecrou Hm_Ecrou H M  006"
  Placement = pos=(271.733,231.093,-64.3054) rot=(0.975931,0.218077,0;3.14159rad)
  shape: bbox 8.084 x 8.084 x 2.001 mm, 22 faces (baked)
FEATURE [Part::Feature] Part__Feature174  label="Ecrou Hm_Ecrou H M  007"
  Placement = pos=(271.733,231.093,-62.3054) rot=(0.980747,0.195284,0;3.14159rad)
  shape: bbox 8.084 x 8.084 x 2.001 mm, 22 faces (baked)
FEATURE [Part::Feature] Part__Feature175  label="Ecrou Hm_Ecrou H M 014"
  Placement = pos=(254.573,240.355,-86.3054) rot=(0.487486,0.873013,0.014332;1.571rad)
  shape: bbox 12.59 x 18.32 x 18.48 mm, 22 faces (baked)
FEATURE [Part::Feature] Part__Feature176  label="Ecrou Hm_Ecrou H M  008"
  Placement = pos=(190.333,275.028,-86.3054) rot=(-0.493539,-0.869462,0.021345;1.57125rad)
  shape: bbox 5.345 x 7.926 x 8.084 mm, 22 faces (baked)
FEATURE [Part::Feature] Part__Feature177  label="Ecrou Hm_Ecrou H M 015"
  Placement = pos=(188.573,275.978,-86.3054) rot=(0.487486,0.873013,0.014332;1.571rad)
  shape: bbox 12.59 x 18.32 x 18.48 mm, 22 faces (baked)
FEATURE [Part::Feature] Part__Feature178  label="Vis CHc_vis CHc M 5 X  16  "
  Placement = pos=(269.394,193.466,-61.3054) rot=(0.980747,0.195284,0;3.14159rad)
  shape: bbox 8.501 x 8.501 x 21 mm, 18 faces (baked)
FEATURE [Part::Feature] Part__Feature179  label="Vis CHc_vis CHc M 4 X   8  "
  Placement = pos=(269.394,193.466,-110.305) rot=(0,0,1;0rad)
  shape: bbox 7.577 x 7.577 x 12 mm, 18 faces (baked)
FEATURE [Part::Feature] Part__Feature180  label="Vis CHc_vis CHc M 4 X  16  "
  Placement = pos=(244.952,232.957,-86.3054) rot=(0.876808,-0.480512,0.017767;1.57111rad)
  shape: bbox 14.03 x 20.07 x 7.31 mm, 18 faces (baked)
FEATURE [Part::Feature] Part__Feature181  label="Vis CHc_vis CHc M 4 X  16  001"
  Placement = pos=(260.003,225.053,-86.3054) rot=(0.871544,-0.489507,0.028178;1.57159rad)
  shape: bbox 14.05 x 20.08 x 7.35 mm, 18 faces (baked)
FEATURE [Part::Feature] Part__Feature182  label="Vis FHc_vis F HC M 6 X  030"
  Placement = pos=(177.078,337.438,-86.3054) rot=(0.726221,0.656145,0.205128;1.61474rad)
  shape: bbox 27.72 x 23.28 x 11.3 mm, 17 faces (baked)
FEATURE [Part::Feature] Part__Feature183  label="Vis FHc_vis F HC M 6 X  10"
  Placement = pos=(98.4055,215.212,148.395) rot=(0.862856,0.357407,0.357407;1.71777rad)
  shape: bbox 15.17 x 15.17 x 11.3 mm, 17 faces (baked)
FEATURE [Part::Feature] Part__Feature184  label="Vis FHc_vis F HC M 6 X  031"
  Placement = pos=(98.4055,215.212,-86.6054) rot=(0.862856,0.357407,0.357407;1.71777rad)
  shape: bbox 15.17 x 15.17 x 11.3 mm, 17 faces (baked)
FEATURE [Part::Feature] Part__Feature185  label="Vis FHc_vis F HC M 6 X  032"
  Placement = pos=(98.4055,215.212,30.8946) rot=(0.862856,0.357407,0.357407;1.71777rad)
  shape: bbox 15.17 x 15.17 x 11.3 mm, 17 faces (baked)
FEATURE [Part::Feature] Part__Feature186  label="Vis Hc à bout plat_Vis Hc M4-5 Bout plat"
  Placement = pos=(273.763,206.369,56.9946) rot=(0,0,1;0rad)
  shape: bbox 4.001 x 4.001 x 5.001 mm, 22 faces (baked)
FEATURE [Part::Feature] Part__Feature187  label="Vis Hc à bout plat_Vis Hc M4-5 Bout plat001"
  Placement = pos=(273.763,206.369,12.9946) rot=(-0.195284,0.980747,0;3.14159rad)
  shape: bbox 4.001 x 4.001 x 5.001 mm, 22 faces (baked)
FEATURE [Part::Feature] Part__Feature188  label="Ecrou borgne_crou borgne M 6"
  Placement = pos=(194.839,324.626,-86.3054) rot=(0,0,1;0.945899rad)
  shape: bbox 13.78 x 13.51 x 11.55 mm, 24 faces (baked)
FEATURE [Part::Feature] Part__Feature189  label="Ecrou borgne_crou borgne M 007"
  Placement = pos=(184.309,310.028,-86.3054) rot=(0,0,1;0.945899rad)
  shape: bbox 13.78 x 13.51 x 11.55 mm, 24 faces (baked)
FEATURE [Part::Feature] Part__Feature190  label="Ecrou borgne_crou borgne M 008"
  Placement = pos=(195.039,324.509,34.9946) rot=(0,0,1;0.944072rad)
  shape: bbox 13.78 x 13.51 x 11.55 mm, 24 faces (baked)
FEATURE [Part::Feature] Part__Feature191  label="Ecrou borgne_crou borgne M 009"
  Placement = pos=(185.697,309.05,34.9946) rot=(0,0,1;0.944072rad)
  shape: bbox 13.78 x 13.51 x 11.55 mm, 24 faces (baked)
FEATURE [Part::Feature] Part__Feature192  label="Ecrou borgne_crou borgne M 010"
  Placement = pos=(194.976,324.546,148.595) rot=(0,0,1;0.944646rad)
  shape: bbox 13.78 x 13.51 x 11.55 mm, 24 faces (baked)
FEATURE [Part::Feature] Part__Feature193  label="Ecrou borgne_crou borgne M 011"
  Placement = pos=(184.428,309.961,148.595) rot=(0,0,1;0.944646rad)
  shape: bbox 13.78 x 13.51 x 11.55 mm, 24 faces (baked)
FEATURE [Part::Feature] Part__Feature194  label="Vis FHc_vis F HC M 3 X   6"
  Placement = pos=(112.901,200.717,20.8946) rot=(-0.862856,-0.357407,0.357407;1.71777rad)
  shape: bbox 8.238 x 8.238 x 5.5 mm, 17 faces (baked)
FEATURE [Part::Feature] Part__Feature195  label="Vis FHc_vis F HC M 3 X   007"
  Placement = pos=(112.901,200.717,-19.1054) rot=(-0.862856,-0.357407,0.357407;1.71777rad)
  shape: bbox 8.238 x 8.238 x 5.5 mm, 17 faces (baked)
FEATURE [Part::Feature] Part__Feature196  label="Vis CHc_vis CHc M 3 x  10  "
  Placement = pos=(143.943,254.067,-58.8054) rot=(0.980747,0.195284,0;3.14159rad)
  shape: bbox 5.501 x 5.501 x 13 mm, 18 faces (baked)
FEATURE [Part::Feature] Part__Feature197  label="Vis CHc_vis CHc M 3 x  10  001"
  Placement = pos=(136.923,244.335,-58.8054) rot=(0.980747,0.195284,0;3.14159rad)
  shape: bbox 5.501 x 5.501 x 13 mm, 18 faces (baked)
FEATURE [Part::Feature] Part__Feature198  label="Vis CHc_vis CHc M 3 x  10  002"
  Placement = pos=(153.409,239.841,-58.8054) rot=(0.980747,0.195284,0;3.14159rad)
  shape: bbox 5.501 x 5.501 x 13 mm, 18 faces (baked)
FEATURE [Part::Feature] Part__Feature199  label="Vis CHc_vis CHc M 3 x  10  003"
  Placement = pos=(143.992,254.051,176.095) rot=(0.980747,0.195284,0;3.14159rad)
  shape: bbox 5.501 x 5.501 x 13 mm, 18 faces (baked)
FEATURE [Part::Feature] Part__Feature200  label="Vis CHc_vis CHc M 3 x  10  004"
  Placement = pos=(136.959,244.327,176.095) rot=(0.980747,0.195284,0;3.14159rad)
  shape: bbox 5.501 x 5.501 x 13 mm, 18 faces (baked)
FEATURE [Part::Feature] Part__Feature201  label="Vis CHc_vis CHc M 3 x  10  005"
  Placement = pos=(153.44,239.813,176.095) rot=(0.980747,0.195284,0;3.14159rad)
  shape: bbox 5.501 x 5.501 x 13 mm, 18 faces (baked)
FEATURE [App::Part] _0___Pedalier_CSP_V2  label="00 - Pedalier CSP V2"
  Group = -> [Part__Feature069,Part__Feature070,Part__Feature071,Part__Feature072,Part__Feature073,Part__Feature074,Part__Feature075,Part__Feature076,Part__Feature077,Part__Feature078,Part__Feature079,Part__Feature080,Part__Feature081,Part__Feature082,Part__Feature083,Part__Feature084,Part__Feature085,Part__Feature086,Part__Feature087,Part__Feature088,Part__Feature089,Part__Feature090,Part__Feature091,+110 more]
  Origin = -> Origin013
  Placement = pos=(-340,-295,-204) rot=(0.57735,0.57735,0.57735;2.0944rad)
FEATURE [Sketcher::SketchObject] Sketch007
  FullyConstrained = true
  MapMode = 5
  Support = -> [XY_Plane015]
  sketch-geometry (1):
    g0: Circle CenterX=0 CenterY=0 CenterZ=0 NormalX=0 NormalY=0 NormalZ=1 AngleXU=0 Radius=7.5
  constraints (2):
    c: Coincident(g0,g-1)
    c: Diameter(g0) = 15
FEATURE [PartDesign::Pad] Pad003
  Direction = (1,1,1)
  Length = 70
  Length2 = 100
  Profile = -> Sketch007
  Type = 0
FEATURE [PartDesign::Thickness] Thickness
  Base = -> Pad003 [Face3,Face2]
  BaseFeature = -> Pad003
  Intersection = false
  Join = 0
  Mode = 0
  SupportTransform = false
  Value = 2
FEATURE [Sketcher::SketchObject] Sketch008
  FullyConstrained = true
  MapMode = 5
  Support = -> [XY_Plane016]
  sketch-geometry (12):
    g0: LineSegment StartX=-12.5 StartY=12.5 StartZ=0 EndX=12.5 EndY=12.5 EndZ=0
    g1: LineSegment StartX=12.5 StartY=12.5 StartZ=0 EndX=12.5 EndY=-12.5 EndZ=0
    g2: LineSegment StartX=12.5 StartY=-12.5 StartZ=0 EndX=-12.5 EndY=-12.5 EndZ=0
    g3: LineSegment StartX=-12.5 StartY=-12.5 StartZ=0 EndX=-12.5 EndY=12.5 EndZ=0
    g4: LineSegment StartX=-11.5 StartY=11.5 StartZ=0 EndX=11.5 EndY=11.5 EndZ=0
    g5: LineSegment StartX=11.5 StartY=11.5 StartZ=0 EndX=11.5 EndY=-11.5 EndZ=0
    g6: LineSegment StartX=11.5 StartY=-11.5 StartZ=0 EndX=-11.5 EndY=-11.5 EndZ=0
    g7: LineSegment StartX=-11.5 StartY=-11.5 StartZ=0 EndX=-11.5 EndY=11.5 EndZ=0
    g8: LineSegment StartX=-11.5 StartY=12.5 StartZ=0 EndX=-11.5 EndY=-11.5 EndZ=0
    g9: LineSegment StartX=11.5 StartY=12.5 StartZ=0 EndX=11.5 EndY=-11.5 EndZ=0
    g10: LineSegment StartX=-12.5 StartY=12.5 StartZ=0 EndX=-11.5 EndY=12.5 EndZ=0
    g11: LineSegment StartX=11.5 StartY=12.5 StartZ=0 EndX=12.5 EndY=12.5 EndZ=0
  constraints (32):
    c: Coincident(g0,g1)
    c: Coincident(g1,g2)
    c: Coincident(g2,g3)
    c: Coincident(g3,g0)
    c: Horizontal(g0)
    c: Horizontal(g2)
    c: Vertical(g1)
    c: Vertical(g3)
    c: Symmetric(g0,g2,g-1)
    c: DistanceY(g3,g3) = 25
    c: DistanceX(g2,g2) = 25
    c: Coincident(g4,g5)
    c: Coincident(g5,g6)
    c: Coincident(g6,g7)
    c: Coincident(g7,g4)
    c: Horizontal(g4)
    c: Horizontal(g6)
    c: Vertical(g5)
    c: Vertical(g7)
    c: DistanceY(g4,g3) = 1
    c: DistanceX(g3,g4) = 1
    c: Symmetric(g4,g6,g-1)
    c: PointOnObject(g8,g0)
    c: Coincident(g8,g6)
    c: Vertical(g8)
    c: PointOnObject(g9,g0)
    c: Coincident(g9,g5)
    c: Vertical(g9)
    c: Coincident(g10,g3)
    c: Coincident(g10,g8)
    c: Coincident(g11,g9)
    c: Coincident(g11,g1)
FEATURE [PartDesign::Pad] Pad004
  Direction = (1,1,1)
  Length = 20
  Length2 = 100
  Profile = -> Sketch008
  Type = 0
FEATURE [Sketcher::SketchObject] Sketch009
  ExternalGeometry = -> [Pad004]
  FullyConstrained = false
  MapMode = 5
  Placement = pos=(12.5,0,0) rot=(0.57735,0.57735,0.57735;2.0944rad)
  Support = -> [Pad004]
  sketch-geometry (1):
    g0: Circle CenterX=4.5 CenterY=10 CenterZ=0 NormalX=0 NormalY=0 NormalZ=1 AngleXU=0 Radius=3
  constraints (2):
    c: Diameter(g0) = 6
    c: DistanceX(g0,g-5) = 8
FEATURE [PartDesign::Pocket] Pocket003
  BaseFeature = -> Pad004
  Length = 5
  Length2 = 100
  Profile = -> Sketch009
  Type = 1
FEATURE [Sketcher::SketchObject] Sketch010
  ExternalGeometry = -> [Pocket003]
  FullyConstrained = true
  MapMode = 5
  Placement = pos=(0,-12.5,0) rot=(1,0,0;1.5708rad)
  Support = -> [Pocket003]
  sketch-geometry (1):
    g0: Circle CenterX=-6e-16 CenterY=10 CenterZ=0 NormalX=0 NormalY=0 NormalZ=1 AngleXU=0 Radius=5
  constraints (2):
    c: Symmetric(g-5,g-6,g0)
    c: Diameter(g0) = 10
FEATURE [PartDesign::Pocket] Pocket004
  BaseFeature = -> Pocket003
  Length = 5
  Length2 = 100
  Profile = -> Sketch010
  Type = 1
FEATURE [PartDesign::Body] _______________________004  label="Крепление пружины"
  Group = -> [Sketch008,Pad004,Sketch009,Pocket003,Sketch010,Pocket004]
  Origin = -> Origin016
  Placement = pos=(0.5,-130.38,67.6455) rot=(1,0,0;2.72271rad)
  Tip = -> Pocket004
FEATURE [Part::FeaturePython] ThreadedRod  label="M10x110.0-ThreadedRod"  # Fasteners workbench fastener (typed FeaturePython)
  Placement = pos=(0.5,-133.991,58.3067) rot=(1,0,0;1.15192rad)
  baseObject = -> _______________________004 [Edge24]
  diameter = 10
  diameterCustom = 6
  invert = true
  length = 110
  matchOuter = false
  offset = 11
  pitchCustom = 1
  thread = false
FEATURE [Part::FeaturePython] Nut  label="M10-Nut"  # Fasteners workbench fastener (typed FeaturePython)
  Placement = pos=(0.5,-122.571,53.2225) rot=(-1,0,0;1.98968rad)
  baseObject = -> ThreadedRod [Edge2]
  diameter = 4
  invert = true
  matchOuter = false
  offset = 11
  thread = false
  type = 8
FEATURE [Sketcher::SketchObject] Sketch011
  FullyConstrained = true
  MapMode = 5
  Placement = pos=(0,0,0) rot=(0.57735,0.57735,0.57735;2.0944rad)
  Support = -> [YZ_Plane015]
  sketch-geometry (1):
    g0: Circle CenterX=0 CenterY=10 CenterZ=0 NormalX=0 NormalY=0 NormalZ=1 AngleXU=0 Radius=3
  constraints (3):
    c: PointOnObject(g0,g-2)
    c: Diameter(g0) = 6
    c: DistanceY(g-1,g0) = 10
FEATURE [PartDesign::Pocket] Pocket005
  BaseFeature = -> Thickness
  Length = 5
  Length2 = 100
  Midplane = true
  Profile = -> Sketch011
  Reversed = true
  Type = 1
FEATURE [PartDesign::Body] Body001  label="Втулка упор пружины"
  Group = -> [Sketch007,Pad003,Thickness,Sketch011,Pocket005]
  Origin = -> Origin015
  Placement = pos=(-0.218848,0.0914786,-1.27323) rot=(1,0,0;1.16937rad)
  Tip = -> Pocket005
FEATURE [PartDesign::Draft] Draft001
  Angle = 17
  Base = -> Pocket001 [Face4]
  BaseFeature = -> Pocket001
  SupportTransform = false
FEATURE [Part::FeaturePython] Nut001  label="M10-Nut001"  # Fasteners workbench fastener (typed FeaturePython)
  Placement = pos=(0.5,-131.707,57.2899) rot=(-1,0,0;1.98968rad)
  baseObject = -> ThreadedRod [Edge2]
  diameter = 10
  invert = true
  matchOuter = false
  offset = 1
  thread = false
  type = 7
FEATURE [TechDraw::DrawSVGTemplate] Template
  Height = 210
  Orientation = 1
  Width = 297
FEATURE [PartDesign::Chamfer] Chamfer
  Angle = 45
  Base = -> Draft001 [Edge3]
  BaseFeature = -> Draft001
  ChamferType = 1
  FlipDirection = false
  Size = 10
  Size2 = 20
  SupportTransform = false
FEATURE [Sketcher::SketchObject] Sketch012
  FullyConstrained = false
  MapMode = 5
  Placement = pos=(0,-10,0) rot=(1,0,0;1.5708rad)
  sketch-geometry (2):
    g0: Circle CenterX=0 CenterY=170 CenterZ=0 NormalX=0 NormalY=0 NormalZ=1 AngleXU=0 Radius=2.5
    g1: Circle CenterX=0 CenterY=150 CenterZ=0 NormalX=0 NormalY=0 NormalZ=1 AngleXU=0 Radius=2.5
  constraints (5):
    c: PointOnObject(g0,g-2)
    c: PointOnObject(g1,g-2)
    c: Equal(g1,g0)
    c: Diameter(g0) = 5
    c: Distance(g1,g0) = 20
FEATURE [Sketcher::SketchObject] Sketch013
  ExternalGeometry = -> [Pocket]
  FullyConstrained = true
  MapMode = 5
  Placement = pos=(0,-9,0) rot=(0,0.707107,0.707107;3.14159rad)
  Support = -> [Pocket]
  sketch-geometry (2):
    g0: Circle CenterX=0 CenterY=220 CenterZ=0 NormalX=0 NormalY=0 NormalZ=1 AngleXU=0 Radius=3
    g1: Circle CenterX=0 CenterY=10 CenterZ=0 NormalX=0 NormalY=0 NormalZ=1 AngleXU=0 Radius=3
  constraints (6):
    c: PointOnObject(g0,g-2)
    c: PointOnObject(g1,g-2)
    c: Equal(g1,g0)
    c: Diameter(g0) = 6
    c: DistanceY(g0,g-6) = 20
    c: DistanceY(g-1,g1) = 10
FEATURE [PartDesign::Pocket] Pocket007
  BaseFeature = -> Pocket
  Length = 5
  Length2 = 100
  Profile = -> Sketch013
  Type = 1
FEATURE [Sketcher::SketchObject] Sketch018
  FullyConstrained = true
  MapMode = 5
  Support = -> [XY_Plane020]
  sketch-geometry (12):
    g0: LineSegment StartX=-14 StartY=12.5 StartZ=0 EndX=14 EndY=12.5 EndZ=0
    g1: LineSegment StartX=14 StartY=12.5 StartZ=0 EndX=14 EndY=-12.5 EndZ=0
    g2: LineSegment StartX=14 StartY=-12.5 StartZ=0 EndX=-14 EndY=-12.5 EndZ=0
    g3: LineSegment StartX=-14 StartY=-12.5 StartZ=0 EndX=-14 EndY=12.5 EndZ=0
    g4: LineSegment StartX=-13 StartY=11.5 StartZ=0 EndX=13 EndY=11.5 EndZ=0
    g5: LineSegment StartX=13 StartY=11.5 StartZ=0 EndX=13 EndY=-11.5 EndZ=0
    g6: LineSegment StartX=13 StartY=-11.5 StartZ=0 EndX=-13 EndY=-11.5 EndZ=0
    g7: LineSegment StartX=-13 StartY=-11.5 StartZ=0 EndX=-13 EndY=11.5 EndZ=0
    g8: LineSegment StartX=-13 StartY=12.5 StartZ=0 EndX=-13 EndY=-11.5 EndZ=0
    g9: LineSegment StartX=13 StartY=12.5 StartZ=0 EndX=13 EndY=-11.5 EndZ=0
    g10: LineSegment StartX=-14 StartY=12.5 StartZ=0 EndX=-13 EndY=12.5 EndZ=0
    g11: LineSegment StartX=13 StartY=12.5 StartZ=0 EndX=14 EndY=12.5 EndZ=0
  constraints (32):
    c: Coincident(g0,g1)
    c: Coincident(g1,g2)
    c: Coincident(g2,g3)
    c: Coincident(g3,g0)
    c: Horizontal(g0)
    c: Horizontal(g2)
    c: Vertical(g1)
    c: Vertical(g3)
    c: Symmetric(g0,g2,g-1)
    c: DistanceY(g3,g3) = 25
    c: DistanceX(g2,g2) = 28
    c: Coincident(g4,g5)
    c: Coincident(g5,g6)
    c: Coincident(g6,g7)
    c: Coincident(g7,g4)
    c: Horizontal(g4)
    c: Horizontal(g6)
    c: Vertical(g5)
    c: Vertical(g7)
    c: DistanceY(g4,g3) = 1
    c: DistanceX(g3,g4) = 1
    c: Symmetric(g4,g6,g-1)
    c: PointOnObject(g8,g0)
    c: Coincident(g8,g6)
    c: Vertical(g8)
    c: PointOnObject(g9,g0)
    c: Coincident(g9,g5)
    c: Vertical(g9)
    c: Coincident(g10,g3)
    c: Coincident(g10,g8)
    c: Coincident(g11,g9)
    c: Coincident(g11,g1)
FEATURE [Sketcher::SketchObject] Sketch026
  FullyConstrained = true
  MapMode = 5
  Support = -> [XY_Plane021]
  sketch-geometry (12):
    g0: LineSegment StartX=-15 StartY=10 StartZ=0 EndX=15 EndY=10 EndZ=0
    g1: LineSegment StartX=15 StartY=10 StartZ=0 EndX=15 EndY=-10 EndZ=0
    g2: LineSegment StartX=15 StartY=-10 StartZ=0 EndX=-15 EndY=-10 EndZ=0
    g3: LineSegment StartX=-15 StartY=-10 StartZ=0 EndX=-15 EndY=10 EndZ=0
    g4: LineSegment StartX=-14 StartY=9 StartZ=0 EndX=14 EndY=9 EndZ=0
    g5: LineSegment StartX=14 StartY=9 StartZ=0 EndX=14 EndY=-9 EndZ=0
    g6: LineSegment StartX=14 StartY=-9 StartZ=0 EndX=-14 EndY=-9 EndZ=0
    g7: LineSegment StartX=-14 StartY=-9 StartZ=0 EndX=-14 EndY=9 EndZ=0
    g8: LineSegment StartX=-14 StartY=10 StartZ=0 EndX=-14 EndY=-9 EndZ=0
    g9: LineSegment StartX=14 StartY=10 StartZ=0 EndX=14 EndY=-9 EndZ=0
    g10: LineSegment StartX=-15 StartY=10 StartZ=0 EndX=-14 EndY=10 EndZ=0
    g11: LineSegment StartX=14 StartY=10 StartZ=0 EndX=15 EndY=10 EndZ=0
  constraints (32):
    c: Coincident(g0,g1)
    c: Coincident(g1,g2)
    c: Coincident(g2,g3)
    c: Coincident(g3,g0)
    c: Horizontal(g0)
    c: Horizontal(g2)
    c: Vertical(g1)
    c: Vertical(g3)
    c: Symmetric(g0,g2,g-1)
    c: DistanceY(g3,g3) = 20
    c: DistanceX(g2,g2) = 30
    c: Coincident(g4,g5)
    c: Coincident(g5,g6)
    c: Coincident(g6,g7)
    c: Coincident(g7,g4)
    c: Horizontal(g4)
    c: Horizontal(g6)
    c: Vertical(g5)
    c: Vertical(g7)
    c: DistanceY(g4,g3) = 1
    c: DistanceX(g3,g4) = 1
    c: Symmetric(g4,g6,g-1)
    c: PointOnObject(g8,g0)
    c: Coincident(g8,g6)
    c: Vertical(g8)
    c: PointOnObject(g9,g0)
    c: Coincident(g9,g5)
    c: Vertical(g9)
    c: Coincident(g10,g3)
    c: Coincident(g10,g8)
    c: Coincident(g11,g9)
    c: Coincident(g11,g1)
FEATURE [PartDesign::Pad] Pad005
  Direction = (1,1,1)
  Length = 240
  Length2 = 100
  Offset = -10
  Profile = -> Sketch026
  Type = 0
FEATURE [Sketcher::SketchObject] Sketch025
  ExternalGeometry = -> [Pad005]
  FullyConstrained = false
  MapMode = 5
  Placement = pos=(15,0,0) rot=(0.57735,0.57735,0.57735;2.0944rad)
  Support = -> [Pad005]
  sketch-geometry (4):
    g0: LineSegment StartX=0 StartY=240 StartZ=0 EndX=0 EndY=0 EndZ=0
    g1: Circle CenterX=0 CenterY=191.706 CenterZ=0 NormalX=0 NormalY=0 NormalZ=1 AngleXU=0 Radius=3
    g2: Circle CenterX=0 CenterY=26.7063 CenterZ=0 NormalX=0 NormalY=0 NormalZ=1 AngleXU=0 Radius=3
    g3: Circle CenterX=0 CenterY=46.7063 CenterZ=0 NormalX=0 NormalY=0 NormalZ=1 AngleXU=0 Radius=3
  constraints (12):
    c: PointOnObject(g0,g-4)
    c: Coincident(g0,g-1)
    c: Vertical(g0)
    c: Diameter(g1) = 6
    c: Distance(g-4) = 20
    c: Diameter(g2) = 6
    c: DistanceY(g2,g1) = 165
    c: PointOnObject(g1,g0)
    c: PointOnObject(g2,g0)
    c: PointOnObject(g3,g0)
    c: Equal(g3,g2)
    c: Distance(g2,g3) = 20
FEATURE [PartDesign::Pad] Pad009
  Direction = (1,1,1)
  Length = 50
  Length2 = 100
  Profile = -> Sketch018
  Type = 0
FEATURE [PartDesign::Draft] Draft003
  Angle = 15
  Base = -> Pad009 [Face9]
  BaseFeature = -> Pad009
  SupportTransform = false
FEATURE [Sketcher::SketchObject] Sketch015
  FullyConstrained = true
  MapMode = 5
  Placement = pos=(14,0,0) rot=(0.57735,0.57735,0.57735;2.0944rad)
  Support = -> [Draft003]
  sketch-geometry (1):
    g0: Circle CenterX=0 CenterY=12 CenterZ=0 NormalX=0 NormalY=0 NormalZ=1 AngleXU=0 Radius=3
  constraints (3):
    c: PointOnObject(g0,g-2)
    c: Diameter(g0) = 6
    c: Distance(g-1,g0) = 12
FEATURE [PartDesign::Pocket] Pocket009
  BaseFeature = -> Pad005
  Length = 5
  Length2 = 100
  Profile = -> Sketch025
  Type = 1
FEATURE [Sketcher::SketchObject] Sketch023
  ExternalGeometry = -> [Pocket009]
  FullyConstrained = true
  MapMode = 5
  Placement = pos=(0,-9,0) rot=(0,0.707107,0.707107;3.14159rad)
  Support = -> [Pocket009]
  sketch-geometry (2):
    g0: Circle CenterX=0 CenterY=220 CenterZ=0 NormalX=0 NormalY=0 NormalZ=1 AngleXU=0 Radius=3
    g1: Circle CenterX=0 CenterY=10 CenterZ=0 NormalX=0 NormalY=0 NormalZ=1 AngleXU=0 Radius=3
  constraints (6):
    c: PointOnObject(g0,g-2)
    c: PointOnObject(g1,g-2)
    c: Equal(g1,g0)
    c: Diameter(g0) = 6
    c: DistanceY(g0,g-6) = 20
    c: DistanceY(g-1,g1) = 10
FEATURE [PartDesign::Pocket] Pocket010
  BaseFeature = -> Draft003
  Length = 5
  Length2 = 100
  Profile = -> Sketch015
  Type = 1
FEATURE [PartDesign::Pocket] Pocket013
  BaseFeature = -> Pocket009
  Length = 5
  Length2 = 100
  Profile = -> Sketch023
  Type = 1
FEATURE [PartDesign::Body] _______________________005  label="Упор пружины001"
  Group = -> [Sketch018,Pad009,Draft003,Sketch015,Pocket010]
  Origin = -> Origin017
  Placement = pos=(0,-13.1352,-2.8136) rot=(-1,0,0;0.523599rad)
  Tip = -> Pocket010
FEATURE [PartDesign::Body] _______________________008  label="Основа педали001"
  Group = -> [Sketch026,Pad005,Sketch025,Pocket009,Sketch023,Pocket013]
  Origin = -> Origin018
  Placement = pos=(0,16,4e-15) rot=(1,0,0;1.5708rad)
  Tip = -> Pocket013
FEATURE [PartDesign::FeatureBase] Clone001
  BaseFeature = -> _______________________004
  Placement = pos=(0.5,-134.948,69.6792) rot=(1,0,0;2.72271rad)
FEATURE [PartDesign::Body] Body003  label="Крепление пружины001"
  BaseFeature = -> _______________________004
  Group = -> [Clone001]
  Origin = -> Origin024
  Placement = pos=(0,16.7841,72.0144) rot=(1,0,0;0.488692rad)
  Tip = -> Clone001
FEATURE [Part::FeaturePython] ThreadedRod001  label="M10x95.0-ThreadedRod"  # Fasteners workbench fastener (typed FeaturePython)
  Placement = pos=(0.5,-133.884,60.2426) rot=(1,0,0;1.64061rad)
  baseObject = -> Body003 [Edge24]
  diameter = 10
  diameterCustom = 6
  invert = true
  length = 95
  matchOuter = false
  offset = 11
  pitchCustom = 1
  thread = false
FEATURE [Sketcher::SketchObject] Sketch034
  ExternalGeometry = -> [Pocket007]
  FullyConstrained = true
  MapMode = 5
  Placement = pos=(15,0,0) rot=(0.57735,0.57735,0.57735;2.0944rad)
  Support = -> [Pocket007]
  sketch-geometry (1):
    g0: Circle CenterX=2 CenterY=110 CenterZ=0 NormalX=0 NormalY=0 NormalZ=1 AngleXU=0 Radius=3
  constraints (3):
    c: Diameter(g0) = 6
    c: DistanceY(g0,g-5) = 130
    c: Distance(g0,g-4) = 8
FEATURE [PartDesign::Pocket] Pocket017
  BaseFeature = -> Pocket007
  Length = 5
  Length2 = 100
  Profile = -> Sketch034
  Type = 0
FEATURE [PartDesign::Body] _______________________001  label="Основа педали"
  Group = -> [Sketch001,Pad001,Sketch002,Pocket,Sketch013,Pocket007,Sketch034,Pocket017]
  Origin = -> Origin009
  Placement = pos=(0,16,4e-15) rot=(1,0,0;1.5708rad)
  Tip = -> Pocket017
FEATURE [TechDraw::DrawProjGroupItem] ProjItem001  label="Front001"
  CoarseView = false
  Direction = (1,0,0)
  Focus = 100
  HardHidden = false
  IsoCount = 0
  IsoHidden = false
  IsoVisible = false
  LockPosition = true
  Perspective = false
  Rotation = 0
  RotationVector = (0,1,0)
  Scale = 0.5
  ScaleType = 2
  SeamHidden = false
  SeamVisible = true
  SmoothHidden = false
  SmoothVisible = true
  Source = -> [_______________________001]
  Type = 0
  X = 0
  XDirection = (0,1,0)
  Y = 0
FEATURE [TechDraw::DrawViewDimension] Dimension013
  Arbitrary = false
  ArbitraryTolerances = false
  EqualTolerance = true
  FormatSpec = %.2f
  FormatSpecOverTolerance = %+.2f
  FormatSpecUnderTolerance = %+.2f
  Inverted = false
  LockPosition = false
  MeasureType = 1
  OverTolerance = 0
  References2D = -> [ProjItem001]
  Rotation = 0
  ScaleType = 0
  TheoreticalExact = false
  Type = 1
  UnderTolerance = 0
  X = -2.41399
  Y = -14.9297
FEATURE [TechDraw::DrawViewDimension] Dimension014
  Arbitrary = false
  ArbitraryTolerances = false
  EqualTolerance = true
  FormatSpec = %.2f
  FormatSpecOverTolerance = %+.2f
  FormatSpecUnderTolerance = %+.2f
  Inverted = false
  LockPosition = false
  MeasureType = 1
  OverTolerance = 0
  References2D = -> [ProjItem001]
  Rotation = 0
  ScaleType = 0
  TheoreticalExact = false
  Type = 1
  UnderTolerance = 0
  X = -18.6597
  Y = -8.624
FEATURE [TechDraw::DrawViewDimension] Dimension017
  Arbitrary = false
  ArbitraryTolerances = false
  EqualTolerance = true
  FormatSpec = %.2f
  FormatSpecOverTolerance = %+.2f
  FormatSpecUnderTolerance = %+.2f
  Inverted = false
  LockPosition = false
  MeasureType = 1
  OverTolerance = 0
  References2D = -> [ProjItem001]
  Rotation = 0
  ScaleType = 0
  TheoreticalExact = false
  Type = 2
  UnderTolerance = 0
  X = -69.8008
  Y = 0
FEATURE [TechDraw::DrawProjGroupItem] ProjItem005  label="Bottom001"
  CoarseView = false
  Direction = (0,0,-1)
  Focus = 100
  HardHidden = false
  IsoCount = 0
  IsoHidden = false
  IsoVisible = false
  LockPosition = false
  Perspective = false
  Rotation = 0
  RotationVector = (1,0,0)
  ScaleType = 2
  SeamHidden = false
  SeamVisible = true
  SmoothHidden = false
  SmoothVisible = true
  Source = -> [_______________________001]
  Type = 5
  X = 0
  XDirection = (0,1,0)
  Y = 27.2371
FEATURE [TechDraw::DrawViewDimension] Dimension021
  Arbitrary = false
  ArbitraryTolerances = false
  EqualTolerance = true
  FormatSpec = %.2f
  FormatSpecOverTolerance = %+.2f
  FormatSpecUnderTolerance = %+.2f
  Inverted = false
  LockPosition = false
  MeasureType = 1
  OverTolerance = 0
  References2D = -> [ProjItem005]
  Rotation = 0
  ScaleType = 0
  TheoreticalExact = false
  Type = 1
  UnderTolerance = 0
  X = -55.2122
  Y = -9.98063
FEATURE [TechDraw::DrawViewDimension] Dimension022
  Arbitrary = false
  ArbitraryTolerances = false
  EqualTolerance = true
  FormatSpec = %.2f
  FormatSpecOverTolerance = %+.2f
  FormatSpecUnderTolerance = %+.2f
  Inverted = false
  LockPosition = false
  MeasureType = 1
  OverTolerance = 0
  References2D = -> [ProjItem005]
  Rotation = 0
  ScaleType = 0
  TheoreticalExact = false
  Type = 1
  UnderTolerance = 0
  X = 68.5599
  Y = -2.21198
FEATURE [TechDraw::DrawViewDimension] Dimension023
  Arbitrary = false
  ArbitraryTolerances = false
  EqualTolerance = true
  FormatSpec = ⌀%.2f
  FormatSpecOverTolerance = %+.2f
  FormatSpecUnderTolerance = %+.2f
  Inverted = false
  LockPosition = false
  MeasureType = 1
  OverTolerance = 0
  References2D = -> [ProjItem005]
  Rotation = 0
  ScaleType = 0
  TheoreticalExact = false
  Type = 5
  UnderTolerance = 0
  X = -39.6418
  Y = 17.4986
FEATURE [Part::Feature] Part__Feature202  label="COMPOUND"
  shape: bbox 8.7 x 5.6 x 10.5 mm, 0 faces, 0 solids (baked)
FEATURE [Part::Feature] Part__Feature203  label="COMPOUND001"
  shape: bbox 17.4 x 24.95 x 24.8 mm, 138 faces, 12 solids (baked)
FEATURE [App::Part] Document  label="Потенциометр"
  Group = -> [Part__Feature202,Part__Feature203]
  Origin = -> Origin028
  Placement = pos=(24,-94,2) rot=(0.707107,0,-0.707107;3.14159rad)
FEATURE [Sketcher::SketchObject] Sketch035
  FullyConstrained = true
  MapMode = 5
  Support = -> [XY_Plane029]
  sketch-geometry (6):
    g0: LineSegment StartX=-7.5 StartY=-12.5 StartZ=0 EndX=7.5 EndY=-12.5 EndZ=0
    g1: LineSegment StartX=7.5 StartY=-12.5 StartZ=0 EndX=7.5 EndY=12.5 EndZ=0
    g2: LineSegment StartX=7.5 StartY=12.5 StartZ=0 EndX=-7.5 EndY=12.5 EndZ=0
    g3: LineSegment StartX=-7.5 StartY=12.5 StartZ=0 EndX=-7.5 EndY=-12.5 EndZ=0
    g4: Circle CenterX=0 CenterY=-7.5 CenterZ=0 NormalX=0 NormalY=0 NormalZ=1 AngleXU=0 Radius=2.5
    g5: Circle CenterX=0 CenterY=7.5 CenterZ=0 NormalX=0 NormalY=0 NormalZ=1 AngleXU=0 Radius=2
  constraints (17):
    c: Coincident(g0,g1)
    c: Coincident(g1,g2)
    c: Coincident(g2,g3)
    c: Coincident(g3,g0)
    c: Horizontal(g0)
    c: Horizontal(g2)
    c: Vertical(g1)
    c: Vertical(g3)
    c: Symmetric(g1,g0,g-1)
    c: DistanceX(g2,g2) = 15
    c: DistanceY(g3,g3) = 25
    c: PointOnObject(g4,g-2)
    c: Diameter(g4) = 5
    c: DistanceY(g0,g4) = 5
    c: PointOnObject(g5,g-2)
    c: Diameter(g5) = 4
    c: DistanceY(g5,g2) = 5
FEATURE [PartDesign::Pad] Pad012
  Direction = (1,1,1)
  Length = 6
  Length2 = 100
  Profile = -> Sketch035
  Type = 0
FEATURE [PartDesign::Body] Body005  label="Рычаг потенциометра"
  Group = -> [Sketch035,Pad012]
  Origin = -> Origin029
  Placement = pos=(1,-94.9696,9.6527) rot=(0.60812,0.510274,0.60812;2.19793rad)
  Tip = -> Pad012
FEATURE [Sketcher::SketchObject] Sketch036
  FullyConstrained = true
  MapMode = 5
  Support = -> [XY_Plane030]
  sketch-geometry (6):
    g0: LineSegment StartX=-5 StartY=35 StartZ=0 EndX=5 EndY=35 EndZ=0
    g1: LineSegment StartX=5 StartY=35 StartZ=0 EndX=5 EndY=-35 EndZ=0
    g2: LineSegment StartX=5 StartY=-35 StartZ=0 EndX=-5 EndY=-35 EndZ=0
    g3: LineSegment StartX=-5 StartY=-35 StartZ=0 EndX=-5 EndY=35 EndZ=0
    g4: Circle CenterX=0 CenterY=30 CenterZ=0 NormalX=0 NormalY=0 NormalZ=1 AngleXU=0 Radius=2
    g5: Circle CenterX=0 CenterY=-30 CenterZ=0 NormalX=0 NormalY=0 NormalZ=1 AngleXU=0 Radius=2
  constraints (17):
    c: Coincident(g0,g1)
    c: Coincident(g1,g2)
    c: Coincident(g2,g3)
    c: Coincident(g3,g0)
    c: Horizontal(g0)
    c: Horizontal(g2)
    c: Vertical(g1)
    c: Vertical(g3)
    c: Symmetric(g0,g2,g-1)
    c: PointOnObject(g4,g-2)
    c: PointOnObject(g5,g-2)
    c: Equal(g5,g4)
    c: Diameter(g4) = 4
    c: DistanceY(g4,g0) = 5
    c: DistanceY(g2,g5) = 5
    c: DistanceY(g1,g1) = 70
    c: DistanceX(g0,g0) = 10
FEATURE [PartDesign::Pad] Pad013
  Direction = (1,1,1)
  Length = 1.5
  Length2 = 100
  Profile = -> Sketch036
  Type = 0
FEATURE [PartDesign::Body] Body006  label="Штанга потенциометра"
  Group = -> [Sketch036,Pad013]
  Origin = -> Origin030
  Placement = pos=(7,-122.823,29.6892) rot=(-0.227333,0.94691,-0.227333;1.62532rad)
  Tip = -> Pad013
FEATURE [PartDesign::Chamfer] Chamfer001
  Angle = 45
  Base = -> Chamfer [Edge2,Edge18]
  BaseFeature = -> Chamfer
  ChamferType = 0
  FlipDirection = false
  Size = 10
  Size2 = 1
  SupportTransform = false
FEATURE [TechDraw::DrawViewDimension] Dimension032
  Arbitrary = false
  ArbitraryTolerances = false
  EqualTolerance = true
  FormatSpec = %.2f
  FormatSpecOverTolerance = %+.2f
  FormatSpecUnderTolerance = %+.2f
  Inverted = false
  LockPosition = false
  MeasureType = 1
  OverTolerance = 0
  References2D = -> [ProjItem001]
  Rotation = 0
  ScaleType = 0
  TheoreticalExact = false
  Type = 2
  UnderTolerance = 0
  X = 64.7818
  Y = 12.6592
FEATURE [TechDraw::DrawViewDimension] Dimension035
  Arbitrary = false
  ArbitraryTolerances = false
  EqualTolerance = true
  FormatSpec = ⌀%.2f
  FormatSpecOverTolerance = %+.2f
  FormatSpecUnderTolerance = %+.2f
  Inverted = false
  LockPosition = false
  MeasureType = 1
  OverTolerance = 0
  References2D = -> [ProjItem001]
  Rotation = 0
  ScaleType = 0
  TheoreticalExact = false
  Type = 5
  UnderTolerance = 0
  X = -3.57066
  Y = 12.0233
FEATURE [Sketcher::SketchObject] Sketch037
  FullyConstrained = true
  MapMode = 5
  Support = -> [XY_Plane031]
  sketch-geometry (4):
    g0: LineSegment StartX=-170 StartY=170 StartZ=0 EndX=170 EndY=170 EndZ=0
    g1: LineSegment StartX=170 StartY=170 StartZ=0 EndX=170 EndY=-170 EndZ=0
    g2: LineSegment StartX=170 StartY=-170 StartZ=0 EndX=-170 EndY=-170 EndZ=0
    g3: LineSegment StartX=-170 StartY=-170 StartZ=0 EndX=-170 EndY=170 EndZ=0
  constraints (11):
    c: Coincident(g0,g1)
    c: Coincident(g1,g2)
    c: Coincident(g2,g3)
    c: Coincident(g3,g0)
    c: Horizontal(g0)
    c: Horizontal(g2)
    c: Vertical(g1)
    c: Vertical(g3)
    c: DistanceX(g0,g0) = 340
    c: DistanceY(g1,g1) = 340
    c: Symmetric(g0,g2,g-1)
FEATURE [PartDesign::Pad] Pad014
  Direction = (1,1,1)
  Length = 16
  Length2 = 100
  Profile = -> Sketch037
  Type = 0
FEATURE [PartDesign::Body] Body007  label="Основание"
  Group = -> [Sketch037,Pad014]
  Origin = -> Origin031
  Placement = pos=(0,0,-10) rot=(0,0,1;0rad)
  Tip = -> Pad014
FEATURE [Sketcher::SketchObject] Sketch038
  FullyConstrained = true
  MapMode = 5
  Support = -> [XY_Plane033]
  sketch-geometry (4):
    g0: LineSegment StartX=-15 StartY=70 StartZ=0 EndX=15 EndY=70 EndZ=0
    g1: LineSegment StartX=15 StartY=70 StartZ=0 EndX=15 EndY=-70 EndZ=0
    g2: LineSegment StartX=15 StartY=-70 StartZ=0 EndX=-15 EndY=-70 EndZ=0
    g3: LineSegment StartX=-15 StartY=-70 StartZ=0 EndX=-15 EndY=70 EndZ=0
  constraints (11):
    c: Coincident(g0,g1)
    c: Coincident(g1,g2)
    c: Coincident(g2,g3)
    c: Coincident(g3,g0)
    c: Horizontal(g0)
    c: Horizontal(g2)
    c: Vertical(g1)
    c: Vertical(g3)
    c: DistanceX(g0,g0) = 30
    c: DistanceY(g1,g1) = 140
    c: Symmetric(g0,g2,g-1)
FEATURE [PartDesign::Pad] Pad015
  Direction = (1,1,1)
  Length = 16
  Length2 = 100
  Profile = -> Sketch038
  Type = 0
FEATURE [PartDesign::Body] Body008  label="Боковина"
  Group = -> [Sketch038,Pad015]
  Origin = -> Origin033
  Placement = pos=(170,-100,21) rot=(0,-1,0;1.5708rad)
  Tip = -> Pad015
FEATURE [Part::FeaturePython] Clone005  label="Боковина001"  # Draft clone (typed FeaturePython)
  AttacherType = Attacher::AttachEngine3D
  Fuse = false
  Objects = -> [Body008]
  Placement = pos=(-154,-100,21) rot=(0,-1,0;1.5708rad)
  Scale = (1,1,1)
FEATURE [Sketcher::SketchObject] Sketch039
  FullyConstrained = true
  MapMode = 5
  Support = -> [XY_Plane034]
  sketch-geometry (4):
    g0: LineSegment StartX=-170 StartY=70 StartZ=0 EndX=170 EndY=70 EndZ=0
    g1: LineSegment StartX=170 StartY=70 StartZ=0 EndX=170 EndY=-70 EndZ=0
    g2: LineSegment StartX=170 StartY=-70 StartZ=0 EndX=-170 EndY=-70 EndZ=0
    g3: LineSegment StartX=-170 StartY=-70 StartZ=0 EndX=-170 EndY=70 EndZ=0
  constraints (11):
    c: Coincident(g0,g1)
    c: Coincident(g1,g2)
    c: Coincident(g2,g3)
    c: Coincident(g3,g0)
    c: Horizontal(g0)
    c: Horizontal(g2)
    c: Vertical(g1)
    c: Vertical(g3)
    c: Symmetric(g2,g0,g-1)
    c: DistanceX(g0,g0) = 340
    c: DistanceY(g3,g3) = 140
FEATURE [PartDesign::Pad] Pad016
  Direction = (1,1,1)
  Length = 6
  Length2 = 100
  Profile = -> Sketch039
  Type = 0
FEATURE [PartDesign::Body] Body009  label="Крышка"
  Group = -> [Sketch039,Pad016]
  Origin = -> Origin034
  Placement = pos=(0,-100,36) rot=(0,0,1;0rad)
  Tip = -> Pad016
FEATURE [PartDesign::Pocket] Pocket018
  BaseFeature = -> Chamfer001
  Length = 5
  Length2 = 100
  Profile = -> Sketch012
  Type = 0
FEATURE [PartDesign::Body] _______________________  label="Рычаг педали"
  Group = -> [Sketch,Pad,Sketch003,Pocket001,Draft001,Chamfer,Sketch012,Chamfer001,Pocket018]
  Origin = -> Origin008
  Placement = pos=(0,-179,-8.66025) rot=(-1,0,0;0.523599rad)
  Tip = -> Pocket018
FEATURE [PartDesign::FeatureBase] Clone
  BaseFeature = -> _______________________
  Placement = pos=(0,-179,-8.66025) rot=(-1,0,0;0.523599rad)
FEATURE [PartDesign::Body] Body  label="Рычаг"
  BaseFeature = -> _______________________
  Group = -> [Clone]
  Origin = -> Origin023
  Tip = -> Clone
FEATURE [Sketcher::SketchObject] Sketch040
  FullyConstrained = true
  MapMode = 5
  Support = -> [XY_Plane035]
  sketch-geometry (6):
    g0: LineSegment StartX=-35 StartY=42.5 StartZ=0 EndX=35 EndY=42.5 EndZ=0
    g1: LineSegment StartX=35 StartY=42.5 StartZ=0 EndX=35 EndY=-42.5 EndZ=0
    g2: LineSegment StartX=35 StartY=-42.5 StartZ=0 EndX=-35 EndY=-42.5 EndZ=0
    g3: LineSegment StartX=-35 StartY=-42.5 StartZ=0 EndX=-35 EndY=42.5 EndZ=0
    g4: Circle CenterX=0 CenterY=2.5 CenterZ=0 NormalX=0 NormalY=0 NormalZ=1 AngleXU=0 Radius=2.5
    g5: Circle CenterX=0 CenterY=22.5 CenterZ=0 NormalX=0 NormalY=0 NormalZ=1 AngleXU=0 Radius=2.5
  constraints (17):
    c: Coincident(g0,g1)
    c: Coincident(g1,g2)
    c: Coincident(g2,g3)
    c: Coincident(g3,g0)
    c: Horizontal(g0)
    c: Horizontal(g2)
    c: Vertical(g1)
    c: Vertical(g3)
    c: DistanceX(g0,g0) = 70
    c: DistanceY(g1,g1) = 85
    c: Symmetric(g2,g0,g-1)
    c: PointOnObject(g4,g-2)
    c: PointOnObject(g5,g-2)
    c: Equal(g5,g4)
    c: Diameter(g4) = 5
    c: DistanceY(g4,g5) = 20
    c: DistanceY(g5,g0) = 20
FEATURE [PartDesign::Pad] Pad017
  Direction = (1,1,1)
  Length = 6
  Length2 = 100
  Profile = -> Sketch040
  Type = 0
FEATURE [PartDesign::Body] Body010  label="Накладка"
  Group = -> [Sketch040,Pad017]
  Origin = -> Origin035
  Placement = pos=(0,-113.93,124.667) rot=(1,0,0;1.0472rad)
  Tip = -> Pad017
FEATURE [App::Part] Part001  label="Педаль Газ"
  Group = -> [_______________________,_______________________001,_______________________003,Body001,_______________________004,ThreadedRod,Nut,Nut001,Document,Body005,Body006,Body010]
  Origin = -> Origin012
  Placement = pos=(205,-8,0) rot=(0,0,1;0rad)
FEATURE [Part::FeaturePython] Clone004  label="Педаль Тормоз"  # Draft clone (typed FeaturePython)
  AttacherType = Attacher::AttachEngine3D
  Fuse = false
  Objects = -> [Part001]
  Placement = pos=(85,-9,0) rot=(0,0,1;0rad)
  Scale = (1,1,1)
FEATURE [Part::FeaturePython] Clone006  label="Накладка001"  # Draft clone (typed FeaturePython)
  AttacherType = Attacher::AttachEngine3D
  Fuse = false
  Objects = -> [Body010]
  Placement = pos=(0,-114.43,123.801) rot=(1,0,0;1.0472rad)
  Scale = (1,1,1)
FEATURE [Sketcher::SketchObject] Sketch041
  FullyConstrained = true
  MapMode = 5
  Placement = pos=(0,0,0) rot=(0.57735,0.57735,0.57735;2.0944rad)
  Support = -> [YZ_Plane036]
  sketch-geometry (9):
    g0: LineSegment StartX=5.59401 StartY=-40 StartZ=0 EndX=40.594 EndY=-40 EndZ=0
    g1: LineSegment StartX=40.594 StartY=-40 StartZ=0 EndX=-5.59401 EndY=40 EndZ=0
    g2: LineSegment StartX=-5.59401 StartY=40 StartZ=0 EndX=-40.594 EndY=40 EndZ=0
    g3: LineSegment StartX=-40.594 StartY=40 StartZ=0 EndX=5.59401 EndY=-40 EndZ=0
    g4: Circle CenterX=8.97521 CenterY=-32 CenterZ=0 NormalX=0 NormalY=0 NormalZ=1 AngleXU=0 Radius=3
    g5: Circle CenterX=-27.9752 CenterY=32 CenterZ=0 NormalX=0 NormalY=0 NormalZ=1 AngleXU=0 Radius=3
    g6: Circle CenterX=28.9752 CenterY=-32 CenterZ=0 NormalX=0 NormalY=0 NormalZ=1 AngleXU=0 Radius=3
    g7: LineSegment StartX=-32.594 StartY=40 StartZ=0 EndX=13.594 EndY=-40 EndZ=0
    g8: LineSegment StartX=0.975209 StartY=-32 StartZ=0 EndX=35.9752 EndY=-32 EndZ=0
  constraints (28):
    c: Coincident(g0,g1)
    c: Coincident(g1,g2)
    c: Coincident(g2,g3)
    c: Coincident(g3,g0)
    c: Horizontal(g0)
    c: Horizontal(g2)
    c: Symmetric(g1,g0,g-1)
    c: DistanceY(g1,g1) = 80
    c: DistanceX(g0,g0) = 35
    c: Equal(g4,g5)
    c: Equal(g5,g6)
    c: Diameter(g6) = 6
    c: PointOnObject(g7,g2)
    c: PointOnObject(g7,g0)
    c: PointOnObject(g8,g3)
    c: PointOnObject(g8,g1)
    c: Horizontal(g8)
    c: PointOnObject(g6,g8)
    c: PointOnObject(g4,g8)
    c: PointOnObject(g5,g7)
    c: DistanceX(g2,g7) = 8
    c: PointOnObject(g4,g7)
    c: DistanceY(g0,g8) = 8
    c: DistanceX(g4,g6) = 20
    c: DistanceY(g5,g7) = 8
    c: Parallel(g3,g1)
    c: Parallel(g7,g3)
    c: Angle(g2,g1) = 2.0944
FEATURE [PartDesign::Pad] Pad018
  Direction = (1,1,1)
  Length = 1
  Length2 = 100
  Placement = pos=(0,0,0) rot=(0.57735,0.57735,0.57735;2.0944rad)
  Profile = -> Sketch041
  Type = 0
FEATURE [PartDesign::Body] Body011  label="Опора втулки"
  Group = -> [Sketch041,Pad018]
  Origin = -> Origin036
  Placement = pos=(16,-39,33) rot=(0,0,1;0rad)
  Tip = -> Pad018
FEATURE [Part::FeaturePython] Clone007  label="Опора втулки001"  # Draft clone (typed FeaturePython)
  AttacherType = Attacher::AttachEngine3D
  Fuse = false
  Objects = -> [Body011]
  Placement = pos=(-16,-39,33) rot=(0,0,1;0rad)
  Scale = (1,1,1)
FEATURE [Sketcher::SketchObject] Sketch042
  FullyConstrained = false
  MapMode = 5
  Support = -> [XY_Plane]
  sketch-geometry (10):
    g0: LineSegment StartX=-25.054 StartY=75 StartZ=0 EndX=4.94599 EndY=75 EndZ=0
    g1: LineSegment StartX=4.94599 StartY=75 StartZ=0 EndX=4.94599 EndY=0 EndZ=0
    g2: LineSegment StartX=4.94599 StartY=0 StartZ=0 EndX=-25.054 EndY=0 EndZ=0
    g3: LineSegment StartX=-25.054 StartY=0 StartZ=0 EndX=-25.054 EndY=75 EndZ=0
    g4: LineSegment StartX=-24.054 StartY=75 StartZ=0 EndX=3.94599 EndY=75 EndZ=0
    g5: LineSegment StartX=3.94599 StartY=75 StartZ=0 EndX=3.94599 EndY=1 EndZ=0
    g6: LineSegment StartX=3.94599 StartY=1 StartZ=0 EndX=-24.054 EndY=1 EndZ=0
    g7: LineSegment StartX=-24.054 StartY=1 StartZ=0 EndX=-24.054 EndY=75 EndZ=0
    g8: LineSegment StartX=3.94599 StartY=75 StartZ=0 EndX=4.94599 EndY=75 EndZ=0
    g9: LineSegment StartX=-25.054 StartY=75 StartZ=0 EndX=-24.054 EndY=75 EndZ=0
  constraints (27):
    c: Coincident(g0,g1)
    c: Coincident(g1,g2)
    c: Coincident(g2,g3)
    c: Coincident(g3,g0)
    c: Horizontal(g0)
    c: Horizontal(g2)
    c: Vertical(g1)
    c: Vertical(g3)
    c: PointOnObject(g1,g-1)
    c: Coincident(g4,g5)
    c: Coincident(g5,g6)
    c: Coincident(g6,g7)
    c: Coincident(g7,g4)
    c: Horizontal(g4)
    c: Horizontal(g6)
    c: Vertical(g5)
    c: Vertical(g7)
    c: DistanceY(g3,g3) = 75
    c: DistanceX(g2,g2) = 30
    c: DistanceX(g4,g0) = 1
    c: DistanceX(g0,g4) = 1
    c: DistanceY(g1,g5) = 1
    c: Coincident(g8,g5)
    c: Coincident(g8,g1)
    c: Horizontal(g8)
    c: Coincident(g9,g3)
    c: Coincident(g9,g7)
FEATURE [PartDesign::Pad] Pad019
  Direction = (1,1,1)
  Length = 20
  Length2 = 100
  Profile = -> Sketch042
  Type = 0
FEATURE [Sketcher::SketchObject] Sketch043
  ExternalGeometry = -> [Pad019]
  FullyConstrained = false
  MapMode = 5
  Placement = pos=(4.94599,0,0) rot=(0.57735,0.57735,0.57735;2.0944rad)
  Support = -> [Pad019]
  sketch-geometry (3):
    g0: Circle CenterX=67 CenterY=10 CenterZ=0 NormalX=0 NormalY=0 NormalZ=1 AngleXU=0 Radius=3
    g1: LineSegment StartX=1e-16 StartY=10 StartZ=0 EndX=69.9961 EndY=10 EndZ=0
    g2: Circle CenterX=15 CenterY=10 CenterZ=0 NormalX=0 NormalY=0 NormalZ=1 AngleXU=0 Radius=3
  constraints (9):
    c: Diameter(g0) = 6
    c: Horizontal(g1)
    c: PointOnObject(g1,g-4)
    c: DistanceY(g1,g-4) = 10
    c: PointOnObject(g0,g1)
    c: DistanceX(g0,g-6) = 8
    c: PointOnObject(g2,g1)
    c: Equal(g2,g0)
    c: DistanceX(g1,g2) = 15
FEATURE [PartDesign::Pocket] Pocket019
  BaseFeature = -> Pad019
  Length = 5
  Length2 = 100
  Profile = -> Sketch043
  Type = 1
FEATURE [PartDesign::Body] Body012  label="Качелька"
  Group = -> [Sketch042,Pad019,Sketch043,Pocket019]
  Origin = -> Origin
  Placement = pos=(11,-0.457783,80.2122) rot=(1,0,0;3.21141rad)
  Tip = -> Pocket019
FEATURE [PartDesign::FeatureBase] Clone002
  BaseFeature = -> Body001
  Placement = pos=(-0.218848,0.0914786,-1.27323) rot=(1,0,0;1.16937rad)
FEATURE [PartDesign::Body] Body004  label="Втулка"
  BaseFeature = -> Body001
  Group = -> [Clone002]
  Origin = -> Origin025
  Placement = pos=(1.17533,-5.41775,69.3796) rot=(0.999991,-0.002015,0.003715;0.461398rad)
  Tip = -> Clone002
FEATURE [App::Part] Part002  label="Педаль Сцепление"
  Group = -> [_______________________008,_______________________005,Body,Body003,Body004,ThreadedRod001,Clone006,Body011,Clone007,Body012]
  Origin = -> Origin022
  Placement = pos=(-45,-9,0) rot=(0,0,1;0rad)
FEATURE [Sketcher::SketchObject] Sketch044
  FullyConstrained = true
  MapMode = 5
  Support = -> [XY_Plane037]
  sketch-geometry (4):
    g0: LineSegment StartX=-15 StartY=50 StartZ=0 EndX=15 EndY=50 EndZ=0
    g1: LineSegment StartX=15 StartY=50 StartZ=0 EndX=15 EndY=-50 EndZ=0
    g2: LineSegment StartX=15 StartY=-50 StartZ=0 EndX=-15 EndY=-50 EndZ=0
    g3: LineSegment StartX=-15 StartY=-50 StartZ=0 EndX=-15 EndY=50 EndZ=0
  constraints (11):
    c: Coincident(g0,g1)
    c: Coincident(g1,g2)
    c: Coincident(g2,g3)
    c: Coincident(g3,g0)
    c: Horizontal(g0)
    c: Horizontal(g2)
    c: Vertical(g1)
    c: Vertical(g3)
    c: DistanceX(g0,g0) = 30
    c: DistanceY(g1,g1) = 100
    c: Symmetric(g0,g2,g-1)
FEATURE [PartDesign::Pad] Pad020
  Direction = (1,1,1)
  Length = 16
  Length2 = 100
  Profile = -> Sketch044
  Type = 0
FEATURE [PartDesign::Body] Body013  label="Центральная подпорка"
  Group = -> [Sketch044,Pad020]
  Origin = -> Origin037
  Placement = pos=(6,-121,21) rot=(0,-1,0;1.5708rad)
  Tip = -> Pad020
FEATURE [App::Part] Part003  label="Корпус"
  Group = -> [Body007,Body008,Clone005,Body009,Body013]
  Origin = -> Origin032
  Placement = pos=(83,-162,-16) rot=(0,0,1;0rad)
FEATURE [App::Part] Part  label="Pedals"
  Group = -> [Part001,Part002,Clone004,Part003]
  Origin = -> Origin011
FEATURE [Part::FeaturePython] Clone008  label="Рычаг педали001"  # Draft clone (typed FeaturePython)
  AttacherType = Attacher::AttachEngine3D
  Fuse = false
  Objects = -> [_______________________]
  Placement = pos=(-231,-179,-8.66025) rot=(0,0,1;0rad)
  Scale = (1,1,1)
FEATURE [TechDraw::DrawProjGroupItem] ProjItem  label="Front"
  CoarseView = false
  Direction = (0,-1,0)
  Focus = 100
  HardHidden = false
  IsoCount = 0
  IsoHidden = false
  IsoVisible = false
  LockPosition = true
  Perspective = false
  Rotation = 0
  RotationVector = (1,0,0)
  Scale = 0.5
  ScaleType = 2
  SeamHidden = false
  SeamVisible = true
  SmoothHidden = false
  SmoothVisible = true
  Source = -> [Clone008]
  Type = 0
  X = 0
  XDirection = (1,0,0)
  Y = 0
FEATURE [TechDraw::DrawProjGroupItem] ProjItem006  label="Left"
  CoarseView = false
  Direction = (-1,-1e-16,0)
  Focus = 100
  HardHidden = false
  IsoCount = 0
  IsoHidden = false
  IsoVisible = false
  LockPosition = false
  Perspective = false
  Rotation = 0
  RotationVector = (1,0,0)
  ScaleType = 2
  SeamHidden = false
  SeamVisible = true
  SmoothHidden = false
  SmoothVisible = true
  Source = -> [Clone008]
  Type = 1
  X = 35.6564
  XDirection = (1e-16,-1,0)
  Y = 0
FEATURE [TechDraw::DrawProjGroupItem] ProjItem007  label="FrontTopLeft"
  CoarseView = false
  Direction = (-0.57735,-0.57735,0.57735)
  Focus = 100
  HardHidden = false
  IsoCount = 0
  IsoHidden = false
  IsoVisible = false
  LockPosition = false
  Perspective = false
  Rotation = 0
  RotationVector = (1,0,0)
  ScaleType = 2
  SeamHidden = false
  SeamVisible = true
  SmoothHidden = false
  SmoothVisible = true
  Source = -> [Clone008]
  Type = 6
  X = 76.5669
  XDirection = (0.707107,-0.707107,0)
  Y = -2.94243
FEATURE [TechDraw::DrawProjGroup] ProjGroup
  Anchor = -> ProjItem
  AutoDistribute = true
  LockPosition = false
  ProjectionType = 0
  Rotation = 0
  Scale = 0.5
  ScaleType = 2
  Source = -> [Clone008]
  Views = -> [ProjItem,ProjItem006,ProjItem007]
  X = 27.473
  Y = 146.122
  spacingX = 15
  spacingY = 15
FEATURE [TechDraw::DrawProjGroupItem] ProjItem008  label="FrontTopLeft001"
  CoarseView = false
  Direction = (0.58,-0.58,1)
  Focus = 100
  HardHidden = false
  IsoCount = 0
  IsoHidden = false
  IsoVisible = false
  LockPosition = false
  Perspective = false
  Rotation = 0
  RotationVector = (1,0,0)
  ScaleType = 2
  SeamHidden = false
  SeamVisible = true
  SmoothHidden = false
  SmoothVisible = true
  Source = -> [_______________________001]
  Type = 6
  X = 10.3996
  XDirection = (0.707107,0.707107,0)
  Y = -71.7007
FEATURE [TechDraw::DrawProjGroup] ProjGroup001
  Anchor = -> ProjItem001
  AutoDistribute = false
  LockPosition = false
  ProjectionType = 0
  Rotation = 0
  Scale = 0.5
  ScaleType = 2
  Source = -> [_______________________001]
  Views = -> [ProjItem001,ProjItem005,ProjItem008]
  X = 204.116
  Y = 146.925
  spacingX = 15
  spacingY = 15
FEATURE [TechDraw::DrawViewDimension] Dimension
  Arbitrary = false
  ArbitraryTolerances = false
  EqualTolerance = true
  FormatSpec = %.2f
  FormatSpecOverTolerance = %+.2f
  FormatSpecUnderTolerance = %+.2f
  Inverted = false
  LockPosition = false
  MeasureType = 1
  OverTolerance = 0
  References2D = -> [ProjItem006]
  Rotation = 0
  ScaleType = 0
  TheoreticalExact = false
  Type = 2
  UnderTolerance = 0
  X = 13.7009
  Y = 0
FEATURE [TechDraw::DrawViewDimension] Dimension036
  Arbitrary = false
  ArbitraryTolerances = false
  EqualTolerance = true
  FormatSpec = %.2f
  FormatSpecOverTolerance = %+.2f
  FormatSpecUnderTolerance = %+.2f
  Inverted = false
  LockPosition = false
  MeasureType = 1
  OverTolerance = 0
  References2D = -> [ProjItem]
  Rotation = 0
  ScaleType = 0
  TheoreticalExact = false
  Type = 2
  UnderTolerance = 0
  X = 11.9082
  Y = -0.322911
FEATURE [TechDraw::DrawViewDimension] Dimension037
  Arbitrary = false
  ArbitraryTolerances = false
  EqualTolerance = true
  FormatSpec = ⌀%.2f
  FormatSpecOverTolerance = %+.2f
  FormatSpecUnderTolerance = %+.2f
  Inverted = false
  LockPosition = false
  MeasureType = 1
  OverTolerance = 0
  References2D = -> [ProjItem]
  Rotation = 0
  ScaleType = 0
  TheoreticalExact = false
  Type = 5
  UnderTolerance = 0
  X = -13.3685
  Y = 32.1619
FEATURE [TechDraw::DrawViewDimension] Dimension038
  Arbitrary = false
  ArbitraryTolerances = false
  EqualTolerance = true
  FormatSpec = %.2f
  FormatSpecOverTolerance = %+.2f
  FormatSpecUnderTolerance = %+.2f
  Inverted = false
  LockPosition = false
  MeasureType = 1
  OverTolerance = 0
  References2D = -> [ProjItem]
  Rotation = 0
  ScaleType = 0
  TheoreticalExact = false
  Type = 1
  UnderTolerance = 0
  X = -0.387493
  Y = 54.666
FEATURE [TechDraw::DrawViewDimension] Dimension039
  Arbitrary = false
  ArbitraryTolerances = false
  EqualTolerance = true
  FormatSpec = ⌀%.2f
  FormatSpecOverTolerance = %+.2f
  FormatSpecUnderTolerance = %+.2f
  Inverted = false
  LockPosition = false
  MeasureType = 1
  OverTolerance = 0
  References2D = -> [ProjItem]
  Rotation = 0
  ScaleType = 0
  TheoreticalExact = false
  Type = 5
  UnderTolerance = 0
  X = -13.9497
  Y = 40.9193
FEATURE [TechDraw::DrawViewDimension] Dimension040
  Arbitrary = false
  ArbitraryTolerances = false
  EqualTolerance = true
  FormatSpec = %.2f
  FormatSpecOverTolerance = %+.2f
  FormatSpecUnderTolerance = %+.2f
  Inverted = false
  LockPosition = false
  MeasureType = 1
  OverTolerance = 0
  References2D = -> [ProjItem]
  Rotation = 0
  ScaleType = 0
  TheoreticalExact = false
  Type = 2
  UnderTolerance = 0
  X = 10.8383
  Y = 53.6773
FEATURE [TechDraw::DrawViewDimension] Dimension041
  Arbitrary = false
  ArbitraryTolerances = false
  EqualTolerance = true
  FormatSpec = %.2f
  FormatSpecOverTolerance = %+.2f
  FormatSpecUnderTolerance = %+.2f
  Inverted = false
  LockPosition = false
  MeasureType = 1
  OverTolerance = 0
  References2D = -> [ProjItem]
  Rotation = 0
  ScaleType = 0
  TheoreticalExact = false
  Type = 2
  UnderTolerance = 0
  X = 9.36441
  Y = 37.8203
FEATURE [TechDraw::DrawViewDimension] Dimension042
  Arbitrary = false
  ArbitraryTolerances = false
  EqualTolerance = true
  FormatSpec = %.2f
  FormatSpecOverTolerance = %+.2f
  FormatSpecUnderTolerance = %+.2f
  Inverted = false
  LockPosition = false
  MeasureType = 1
  OverTolerance = 0
  References2D = -> [ProjItem]
  Rotation = 0
  ScaleType = 0
  TheoreticalExact = false
  Type = 1
  UnderTolerance = 0
  X = -13.4752
  Y = -44.2158
FEATURE [TechDraw::DrawViewDimension] Dimension043
  Arbitrary = false
  ArbitraryTolerances = false
  EqualTolerance = true
  FormatSpec = %.2f
  FormatSpecOverTolerance = %+.2f
  FormatSpecUnderTolerance = %+.2f
  Inverted = false
  LockPosition = false
  MeasureType = 1
  OverTolerance = 0
  References2D = -> [ProjItem006]
  Rotation = 0
  ScaleType = 0
  TheoreticalExact = false
  Type = 1
  UnderTolerance = 0
  X = 0.212239
  Y = 53.957
FEATURE [TechDraw::DrawViewDimension] Dimension044
  Arbitrary = false
  ArbitraryTolerances = false
  EqualTolerance = true
  FormatSpec = ⌀%.2f
  FormatSpecOverTolerance = %+.2f
  FormatSpecUnderTolerance = %+.2f
  Inverted = false
  LockPosition = false
  MeasureType = 1
  OverTolerance = 0
  References2D = -> [ProjItem005]
  Rotation = 0
  ScaleType = 0
  TheoreticalExact = false
  Type = 5
  UnderTolerance = 0
  X = 64.945
  Y = 15.7057
FEATURE [TechDraw::DrawViewDimension] Dimension045
  Arbitrary = false
  ArbitraryTolerances = false
  EqualTolerance = true
  FormatSpec = %.2f
  FormatSpecOverTolerance = %+.2f
  FormatSpecUnderTolerance = %+.2f
  Inverted = false
  LockPosition = false
  MeasureType = 1
  OverTolerance = 0
  References2D = -> [ProjItem005]
  Rotation = 0
  ScaleType = 0
  TheoreticalExact = false
  Type = 2
  UnderTolerance = 0
  X = -69.3385
  Y = 1.06119
FEATURE [TechDraw::DrawViewDimension] Dimension046
  Arbitrary = false
  ArbitraryTolerances = false
  EqualTolerance = true
  FormatSpec = %.2f
  FormatSpecOverTolerance = %+.2f
  FormatSpecUnderTolerance = %+.2f
  Inverted = false
  LockPosition = false
  MeasureType = 1
  OverTolerance = 0
  References2D = -> [ProjItem001]
  Rotation = 0
  ScaleType = 0
  TheoreticalExact = false
  Type = 2
  UnderTolerance = 0
  X = 67.299
  Y = -9.92835
FEATURE [TechDraw::DrawViewDimension] Dimension047
  Arbitrary = false
  ArbitraryTolerances = false
  EqualTolerance = true
  FormatSpec = %.2f
  FormatSpecOverTolerance = %+.2f
  FormatSpecUnderTolerance = %+.2f
  Inverted = false
  LockPosition = false
  MeasureType = 1
  OverTolerance = 0
  References2D = -> [ProjItem001]
  Rotation = 0
  ScaleType = 0
  TheoreticalExact = false
  Type = 1
  UnderTolerance = 0
  X = -47.2878
  Y = -5.94268
FEATURE [TechDraw::DrawViewDimension] Dimension048
  Arbitrary = false
  ArbitraryTolerances = false
  EqualTolerance = true
  FormatSpec = %.2f
  FormatSpecOverTolerance = %+.2f
  FormatSpecUnderTolerance = %+.2f
  Inverted = false
  LockPosition = false
  MeasureType = 1
  OverTolerance = 0
  References2D = -> [ProjItem001]
  Rotation = 0
  ScaleType = 0
  TheoreticalExact = false
  Type = 1
  UnderTolerance = 0
  X = 53.5378
  Y = -7.00388
FEATURE [TechDraw::DrawViewDimension] Dimension049
  Arbitrary = false
  ArbitraryTolerances = false
  EqualTolerance = true
  FormatSpec = ⌀%.2f
  FormatSpecOverTolerance = %+.2f
  FormatSpecUnderTolerance = %+.2f
  Inverted = false
  LockPosition = false
  MeasureType = 1
  OverTolerance = 0
  References2D = -> [ProjItem001]
  Rotation = 0
  ScaleType = 0
  TheoreticalExact = false
  Type = 5
  UnderTolerance = 0
  X = -43.9334
  Y = 3.60806
FEATURE [TechDraw::DrawViewDimension] Dimension050
  Arbitrary = false
  ArbitraryTolerances = false
  EqualTolerance = true
  FormatSpec = ⌀%.2f
  FormatSpecOverTolerance = %+.2f
  FormatSpecUnderTolerance = %+.2f
  Inverted = false
  LockPosition = false
  MeasureType = 1
  OverTolerance = 0
  References2D = -> [ProjItem001]
  Rotation = 0
  ScaleType = 0
  TheoreticalExact = false
  Type = 5
  UnderTolerance = 0
  X = 34.5949
  Y = 12.0976
FEATURE [TechDraw::DrawViewDimension] Dimension051
  Arbitrary = false
  ArbitraryTolerances = false
  EqualTolerance = true
  FormatSpec = %.2f
  FormatSpecOverTolerance = %+.2f
  FormatSpecUnderTolerance = %+.2f
  Inverted = false
  LockPosition = false
  MeasureType = 1
  OverTolerance = 0
  References2D = -> [ProjItem006]
  Rotation = 0
  ScaleType = 0
  TheoreticalExact = false
  Type = 1
  UnderTolerance = 0
  X = 9.92835
  Y = 44.514
FEATURE [TechDraw::DrawViewDimension] Dimension052
  Arbitrary = false
  ArbitraryTolerances = false
  EqualTolerance = true
  FormatSpec = ⌀%.2f
  FormatSpecOverTolerance = %+.2f
  FormatSpecUnderTolerance = %+.2f
  Inverted = false
  LockPosition = false
  MeasureType = 1
  OverTolerance = 0
  References2D = -> [ProjItem006]
  Rotation = 0
  ScaleType = 0
  TheoreticalExact = false
  Type = 5
  UnderTolerance = 0
  X = 10.091
  Y = 20.7201
FEATURE [TechDraw::DrawViewDimension] Dimension053
  Arbitrary = false
  ArbitraryTolerances = false
  EqualTolerance = true
  FormatSpec = ⌀%.2f
  FormatSpecOverTolerance = %+.2f
  FormatSpecUnderTolerance = %+.2f
  Inverted = false
  LockPosition = false
  MeasureType = 1
  OverTolerance = 0
  References2D = -> [ProjItem006]
  Rotation = 0
  ScaleType = 0
  TheoreticalExact = false
  Type = 5
  UnderTolerance = 0
  X = 10.8982
  Y = -12.5128
FEATURE [TechDraw::DrawViewDimension] Dimension054
  Arbitrary = false
  ArbitraryTolerances = false
  EqualTolerance = true
  FormatSpec = ⌀%.2f
  FormatSpecOverTolerance = %+.2f
  FormatSpecUnderTolerance = %+.2f
  Inverted = false
  LockPosition = false
  MeasureType = 1
  OverTolerance = 0
  References2D = -> [ProjItem006]
  Rotation = 0
  ScaleType = 0
  TheoreticalExact = false
  Type = 5
  UnderTolerance = 0
  X = 10.6291
  Y = -33.3675
FEATURE [TechDraw::DrawViewDimension] Dimension055
  Arbitrary = false
  ArbitraryTolerances = false
  EqualTolerance = true
  FormatSpec = %.2f
  FormatSpecOverTolerance = %+.2f
  FormatSpecUnderTolerance = %+.2f
  Inverted = false
  LockPosition = false
  MeasureType = 1
  OverTolerance = 0
  References2D = -> [ProjItem006]
  Rotation = 0
  ScaleType = 0
  TheoreticalExact = false
  Type = 2
  UnderTolerance = 0
  X = -16.7934
  Y = -41.344
FEATURE [TechDraw::DrawViewDimension] Dimension056
  Arbitrary = false
  ArbitraryTolerances = false
  EqualTolerance = true
  FormatSpec = %.2f
  FormatSpecOverTolerance = %+.2f
  FormatSpecUnderTolerance = %+.2f
  Inverted = false
  LockPosition = false
  MeasureType = 1
  OverTolerance = 0
  References2D = -> [ProjItem006]
  Rotation = 0
  ScaleType = 0
  TheoreticalExact = false
  Type = 2
  UnderTolerance = 0
  X = -15.6998
  Y = -15.9425
FEATURE [TechDraw::DrawViewDimension] Dimension057
  Arbitrary = false
  ArbitraryTolerances = false
  EqualTolerance = true
  FormatSpec = %.2f
  FormatSpecOverTolerance = %+.2f
  FormatSpecUnderTolerance = %+.2f
  Inverted = false
  LockPosition = false
  MeasureType = 1
  OverTolerance = 0
  References2D = -> [ProjItem006]
  Rotation = 0
  ScaleType = 0
  TheoreticalExact = false
  Type = 2
  UnderTolerance = 0
  X = -10.0991
  Y = -26.5433
FEATURE [TechDraw::DrawViewDimension] Dimension058
  Arbitrary = false
  ArbitraryTolerances = false
  EqualTolerance = true
  FormatSpec = %.2f
  FormatSpecOverTolerance = %+.2f
  FormatSpecUnderTolerance = %+.2f
  Inverted = false
  LockPosition = false
  MeasureType = 1
  OverTolerance = 0
  References2D = -> [ProjItem006]
  Rotation = 0
  ScaleType = 0
  TheoreticalExact = false
  Type = 2
  UnderTolerance = 0
  X = -14.5914
  Y = -0.381795
FEATURE [TechDraw::DrawViewDimension] Dimension059
  Arbitrary = false
  ArbitraryTolerances = false
  EqualTolerance = true
  FormatSpec = %.2f
  FormatSpecOverTolerance = %+.2f
  FormatSpecUnderTolerance = %+.2f
  Inverted = false
  LockPosition = false
  MeasureType = 1
  OverTolerance = 0
  References2D = -> [ProjItem006]
  Rotation = 0
  ScaleType = 0
  TheoreticalExact = false
  Type = 2
  UnderTolerance = 0
  X = -13.8545
  Y = 8.89246
FEATURE [TechDraw::DrawViewDimension] Dimension060
  Arbitrary = false
  ArbitraryTolerances = false
  EqualTolerance = true
  FormatSpec = %.2f
  FormatSpecOverTolerance = %+.2f
  FormatSpecUnderTolerance = %+.2f
  Inverted = false
  LockPosition = false
  MeasureType = 1
  OverTolerance = 0
  References2D = -> [ProjItem006]
  Rotation = 0
  ScaleType = 0
  TheoreticalExact = false
  Type = 2
  UnderTolerance = 0
  X = -12.6754
  Y = 19.051
FEATURE [TechDraw::DrawViewDimension] Dimension065
  Arbitrary = false
  ArbitraryTolerances = false
  EqualTolerance = true
  FormatSpec = %.2f
  FormatSpecOverTolerance = %+.2f
  FormatSpecUnderTolerance = %+.2f
  Inverted = false
  LockPosition = false
  MeasureType = 1
  OverTolerance = 0
  References2D = -> [ProjItem006]
  Rotation = 0
  ScaleType = 0
  TheoreticalExact = false
  Type = 2
  UnderTolerance = 0
  X = -3.25153
  Y = -23.9532
FEATURE [TechDraw::DrawViewDimension] Dimension066
  Arbitrary = false
  ArbitraryTolerances = false
  EqualTolerance = true
  FormatSpec = %.2f
  FormatSpecOverTolerance = %+.2f
  FormatSpecUnderTolerance = %+.2f
  Inverted = false
  LockPosition = false
  MeasureType = 1
  OverTolerance = 0
  References2D = -> [ProjItem006]
  Rotation = 0
  ScaleType = 0
  TheoreticalExact = false
  Type = 2
  UnderTolerance = 0
  X = -9.08187
  Y = -7.12588
FEATURE [TechDraw::DrawViewAnnotation] Annotation
  Font = osifont
  LineSpace = 80
  LockPosition = false
  MaxWidth = -1
  Rotation = 0
  ScaleType = 0
  Text = \u0420\u044b\u0447\u0430\u0433 \u043f\u0435\u0434\u0430\u043b\u0438
  TextSize = 5
  TextStyle = 0
  X = 31.7518
  Y = 79.9389
FEATURE [TechDraw::DrawViewAnnotation] Annotation001
  Font = osifont
  LineSpace = 80
  LockPosition = false
  MaxWidth = -1
  Rotation = 0
  ScaleType = 0
  Text = \u041e\u0441\u043d\u043e\u0432\u0430\u043d\u0438\u0435 \u043f\u0435\u0434\u0430\u043b\u0438
  TextSize = 5
  TextStyle = 0
  X = 189.454
  Y = 111.418
FEATURE [TechDraw::DrawSVGTemplate] Template001
  Height = 297
  Orientation = 0
  Width = 210
FEATURE [TechDraw::DrawProjGroupItem] ProjItem009  label="Front002"
  CoarseView = false
  Direction = (1,0,0)
  Focus = 100
  HardHidden = false
  IsoCount = 0
  IsoHidden = false
  IsoVisible = false
  LockPosition = true
  Perspective = false
  Rotation = 0
  RotationVector = (0,1,0)
  Scale = 0.5
  ScaleType = 2
  SeamHidden = false
  SeamVisible = true
  SmoothHidden = false
  SmoothVisible = true
  Source = -> [Part001]
  Type = 0
  X = 0
  XDirection = (0,1,0)
  Y = 0
FEATURE [TechDraw::DrawProjGroupItem] ProjItem010  label="Bottom"
  CoarseView = false
  Direction = (0,0,-1)
  Focus = 100
  HardHidden = false
  IsoCount = 0
  IsoHidden = false
  IsoVisible = false
  LockPosition = false
  Perspective = false
  Rotation = 0
  RotationVector = (1,0,0)
  ScaleType = 2
  SeamHidden = false
  SeamVisible = true
  SmoothHidden = false
  SmoothVisible = true
  Source = -> [Part001]
  Type = 5
  X = 0
  XDirection = (0,1,0)
  Y = -81.6702
FEATURE [TechDraw::DrawProjGroup] ProjGroup002
  Anchor = -> ProjItem009
  AutoDistribute = false
  LockPosition = false
  ProjectionType = 0
  Rotation = 0
  Scale = 0.5
  ScaleType = 2
  Source = -> [Part001]
  Views = -> [ProjItem009,ProjItem010]
  X = 105.319
  Y = 236.147
  spacingX = 15
  spacingY = 15
FEATURE [TechDraw::DrawViewSection] SectionView  label="Section  - "
  BaseView = -> ProjItem010
  CoarseView = false
  CutSurfaceDisplay = 2
  Direction = (1,0,0)
  FileGeomPattern = <path>
  FileHatchPattern = <path>
  Focus = 100
  FuseBeforeCut = false
  HardHidden = false
  HatchScale = 1
  IsoCount = 0
  IsoHidden = false
  IsoVisible = false
  LockPosition = false
  NameGeomPattern = Алмаз
  Perspective = false
  Rotation = 0
  Scale = 0.5
  ScaleType = 0
  SeamHidden = false
  SeamVisible = true
  SectionDirection = 3
  SectionNormal = (1,0,0)
  SectionOrigin = (206,-112,81.34)
  SmoothHidden = false
  SmoothVisible = true
  Source = -> [Part001]
  X = 103.938
  XDirection = (0,1,0)
  Y = 71.1619
FEATURE [TechDraw::DrawViewDimension] Dimension067
  Arbitrary = false
  ArbitraryTolerances = false
  EqualTolerance = true
  FormatSpec = %.2f
  FormatSpecOverTolerance = %+.2f
  FormatSpecUnderTolerance = %+.2f
  Inverted = false
  LockPosition = false
  MeasureType = 1
  OverTolerance = 0
  References2D = -> [SectionView]
  Rotation = 0
  ScaleType = 0
  TheoreticalExact = false
  Type = 0
  UnderTolerance = 0
  X = 44.768
  Y = -26.2017
FEATURE [TechDraw::DrawViewDimension] Dimension068
  Arbitrary = false
  ArbitraryTolerances = false
  EqualTolerance = true
  FormatSpec = %.2f
  FormatSpecOverTolerance = %+.2f
  FormatSpecUnderTolerance = %+.2f
  Inverted = false
  LockPosition = false
  MeasureType = 1
  OverTolerance = 0
  References2D = -> [SectionView]
  Rotation = 0
  ScaleType = 0
  TheoreticalExact = false
  Type = 0
  UnderTolerance = 0
  X = 17.4943
  Y = -12.4779
FEATURE [TechDraw::DrawViewDimension] Dimension069
  Arbitrary = false
  ArbitraryTolerances = false
  EqualTolerance = true
  FormatSpec = %.2f
  FormatSpecOverTolerance = %+.2f
  FormatSpecUnderTolerance = %+.2f
  Inverted = false
  LockPosition = false
  MeasureType = 1
  OverTolerance = 0
  References2D = -> [SectionView]
  Rotation = 0
  ScaleType = 0
  TheoreticalExact = false
  Type = 0
  UnderTolerance = 0
  X = 6.09925
  Y = -25.0917
FEATURE [TechDraw::DrawViewDimension] Dimension070
  Arbitrary = false
  ArbitraryTolerances = false
  EqualTolerance = true
  FormatSpec = %.2f
  FormatSpecOverTolerance = %+.2f
  FormatSpecUnderTolerance = %+.2f
  Inverted = false
  LockPosition = false
  MeasureType = 1
  OverTolerance = 0
  References2D = -> [SectionView]
  Rotation = 0
  ScaleType = 0
  TheoreticalExact = false
  Type = 0
  UnderTolerance = 0
  X = 4.35858
  Y = -4.08963
FEATURE [TechDraw::DrawSVGTemplate] Template002
  Height = 210
  Orientation = 1
  Width = 297
FEATURE [TechDraw::DrawProjGroupItem] ProjItem011  label="Front003"
  CoarseView = false
  Direction = (1,0,0)
  Focus = 100
  HardHidden = false
  IsoCount = 0
  IsoHidden = false
  IsoVisible = false
  LockPosition = true
  Perspective = false
  Rotation = 0
  RotationVector = (0,1,0)
  ScaleType = 2
  SeamHidden = false
  SeamVisible = true
  SmoothHidden = false
  SmoothVisible = true
  Source = -> [Body001]
  Type = 0
  X = 0
  XDirection = (0,1,0)
  Y = 0
FEATURE [TechDraw::DrawProjGroupItem] ProjItem012  label="Left001"
  CoarseView = false
  Direction = (1e-16,-1,0)
  Focus = 100
  HardHidden = false
  IsoCount = 0
  IsoHidden = false
  IsoVisible = false
  LockPosition = false
  Perspective = false
  Rotation = 0
  RotationVector = (1,0,0)
  ScaleType = 2
  SeamHidden = false
  SeamVisible = true
  SmoothHidden = false
  SmoothVisible = true
  Source = -> [Body001]
  Type = 1
  X = 60.4303
  XDirection = (1,1e-16,0)
  Y = 0
FEATURE [TechDraw::DrawProjGroup] ProjGroup003
  Anchor = -> ProjItem011
  AutoDistribute = true
  LockPosition = false
  ProjectionType = 0
  Rotation = 0
  ScaleType = 0
  Source = -> [Body001]
  Views = -> [ProjItem011,ProjItem012]
  X = 57.0524
  Y = 169.526
  spacingX = 15
  spacingY = 15
FEATURE [TechDraw::DrawViewDimension] Dimension071
  Arbitrary = false
  ArbitraryTolerances = false
  EqualTolerance = true
  FormatSpec = %.2f
  FormatSpecOverTolerance = %+.2f
  FormatSpecUnderTolerance = %+.2f
  Inverted = false
  LockPosition = false
  MeasureType = 1
  OverTolerance = 0
  References2D = -> [ProjItem011]
  Rotation = 0
  ScaleType = 0
  TheoreticalExact = false
  Type = 0
  UnderTolerance = 0
  X = 9.56334
  Y = 18.172
FEATURE [TechDraw::DrawViewDimension] Dimension072
  Arbitrary = false
  ArbitraryTolerances = false
  EqualTolerance = true
  FormatSpec = ⌀%.2f
  FormatSpecOverTolerance = %+.2f
  FormatSpecUnderTolerance = %+.2f
  Inverted = false
  LockPosition = false
  MeasureType = 1
  OverTolerance = 0
  References2D = -> [ProjItem011]
  Rotation = 0
  ScaleType = 0
  TheoreticalExact = false
  Type = 5
  UnderTolerance = 0
  X = -30.483
  Y = -3.08459
FEATURE [TechDraw::DrawViewDimension] Dimension073
  Arbitrary = false
  ArbitraryTolerances = false
  EqualTolerance = true
  FormatSpec = %.2f
  FormatSpecOverTolerance = %+.2f
  FormatSpecUnderTolerance = %+.2f
  Inverted = false
  LockPosition = false
  MeasureType = 1
  OverTolerance = 0
  References2D = -> [ProjItem011]
  Rotation = 0
  ScaleType = 0
  TheoreticalExact = false
  Type = 0
  UnderTolerance = 0
  X = -40.3393
  Y = 18.238
FEATURE [TechDraw::DrawViewAnnotation] Annotation002
  Font = osifont
  LineSpace = 80
  LockPosition = false
  MaxWidth = -1
  Rotation = 0
  ScaleType = 0
  Text = \u0412\u0442\u0443\u043b\u043a\u0430 \u0434\u043b\u044f \u0448\u0442\u043e\u043a\u0430  | \u0422\u0440\u0443\u0431\u0430 \u043c\u0435\u0442\u0430\u043b\u043b\u043e\u043f\u043b\u0430\u0441\u0442\u0438\u043a\u043e\u0432\u0430\u044f 16\u043c\u043c
  TextSize = 5
  TextStyle = 0
  X = 53.6858
  Y = 139.765
FEATURE [TechDraw::DrawProjGroupItem] ProjItem013  label="Front004"
  CoarseView = false
  Direction = (-1,0,0)
  Focus = 100
  HardHidden = false
  IsoCount = 0
  IsoHidden = false
  IsoVisible = false
  LockPosition = true
  Perspective = false
  Rotation = 0
  RotationVector = (0,-1,0)
  ScaleType = 2
  SeamHidden = false
  SeamVisible = true
  SmoothHidden = false
  SmoothVisible = true
  Source = -> [ThreadedRod]
  Type = 0
  X = 0
  XDirection = (0,-1,0)
  Y = 0
FEATURE [TechDraw::DrawProjGroupItem] ProjItem014  label="Left002"
  CoarseView = false
  Direction = (-1e-16,1,0)
  Focus = 100
  HardHidden = false
  IsoCount = 0
  IsoHidden = false
  IsoVisible = false
  LockPosition = false
  Perspective = false
  Rotation = 0
  RotationVector = (1,0,0)
  ScaleType = 2
  SeamHidden = false
  SeamVisible = true
  SmoothHidden = false
  SmoothVisible = true
  Source = -> [ThreadedRod]
  Type = 1
  X = 71.7389
  XDirection = (-1,-1e-16,0)
  Y = 0
FEATURE [TechDraw::DrawProjGroup] ProjGroup004
  Anchor = -> ProjItem013
  AutoDistribute = true
  LockPosition = false
  ProjectionType = 0
  Rotation = 0
  ScaleType = 0
  Source = -> [ThreadedRod]
  Views = -> [ProjItem013,ProjItem014]
  X = 203.369
  Y = 168.073
  spacingX = 15
  spacingY = 15
FEATURE [TechDraw::DrawViewDimension] Dimension074
  Arbitrary = false
  ArbitraryTolerances = false
  EqualTolerance = true
  FormatSpec = %.2f
  FormatSpecOverTolerance = %+.2f
  FormatSpecUnderTolerance = %+.2f
  Inverted = false
  LockPosition = false
  MeasureType = 1
  OverTolerance = 0
  References2D = -> [ProjItem013]
  Rotation = 0
  ScaleType = 0
  TheoreticalExact = false
  Type = 0
  UnderTolerance = 0
  X = -5.66992
  Y = 15.2709
FEATURE [TechDraw::DrawViewDimension] Dimension075
  Arbitrary = false
  ArbitraryTolerances = false
  EqualTolerance = true
  FormatSpec = %.2f
  FormatSpecOverTolerance = %+.2f
  FormatSpecUnderTolerance = %+.2f
  Inverted = false
  LockPosition = false
  MeasureType = 1
  OverTolerance = 0
  References2D = -> [ProjItem013]
  Rotation = 0
  ScaleType = 0
  TheoreticalExact = false
  Type = 0
  UnderTolerance = 0
  X = 47.0232
  Y = 3.27055
FEATURE [TechDraw::DrawViewAnnotation] Annotation003
  Font = osifont
  LineSpace = 80
  LockPosition = false
  MaxWidth = -1
  Rotation = 0
  ScaleType = 0
  Text = \u0428\u0442\u043e\u043a \u043f\u0435\u0434\u0430\u043b\u0438. | \u041c\u043e\u0436\u043d\u043e \u0438\u0441\u043f\u043e\u043b\u044c\u0437\u043e\u0432\u0430\u0442\u044c \u0448\u043f\u0438\u043b\u044c\u043a\u0443 \u043d\u0430 10\u043c\u043c \u043d\u043e \u043c\u0435\u0448\u0430\u0435\u0442\u0441\u044f \u043e\u0441\u0442\u0440\u0430\u044f \u0440\u0435\u0437\u044c\u0431\u0430. | \u042f \u043d\u0430\u0440\u0435\u0437\u0430\u043b \u0440\u0435\u0437\u044c\u0431\u0443 \u043d\u0430 \u043f\u0440\u0443\u0442\u0435 \u043d\u0430 10\u043c\u043c \u043f\u043e\u043b\u0443\u0447\u0438\u043b\u043e\u0441\u044c \u0445\u043e\u0440\u043e\u0448\u043e. | \u041c\u043e\u0436\u043d\u043e \u043f\u043e\u0434\u043e\u0431\u0440\u0430\u0442\u044c \u0432\u0442\u0443\u043b\u043a\u0443 \u0438 \u0448\u0442\u043e\u043a \u0431\u043e\u043b\u0435\u0435 \u043f\u043b\u043e\u0442\u043d\u043e\u0433\u043e \u0440\u0430\u0437\u043c\u0435\u0440\u0430.
  TextSize = 5
  TextStyle = 0
  X = 215.79
  Y = 124.242
FEATURE [TechDraw::DrawViewAnnotation] Annotation004
  Font = osifont
  LineSpace = 80
  LockPosition = false
  MaxWidth = -1
  Rotation = 0
  ScaleType = 0
  Text = \u0425\u043e\u0434 \u043f\u0435\u0434\u0430\u043b\u0438 \u043f\u0440\u0438\u043c\u0435\u0440\u043d\u043e 20\u043c\u043c
  TextSize = 5
  TextStyle = 0
  X = 144.361
  Y = 85.5996
FEATURE [TechDraw::DrawProjGroupItem] ProjItem015  label="Front005"
  CoarseView = false
  Direction = (1,0,0)
  Focus = 100
  HardHidden = false
  IsoCount = 0
  IsoHidden = false
  IsoVisible = false
  LockPosition = true
  Perspective = false
  Rotation = -10
  RotationVector = (0,1,0)
  ScaleType = 2
  SeamHidden = false
  SeamVisible = true
  SmoothHidden = false
  SmoothVisible = true
  Source = -> [Body005]
  Type = 0
  X = 0
  XDirection = (0,1,0)
  Y = 0
FEATURE [TechDraw::DrawProjGroupItem] ProjItem016  label="FrontBottomLeft"
  CoarseView = false
  Direction = (0.57735,-0.57735,-0.57735)
  Focus = 100
  HardHidden = false
  IsoCount = 0
  IsoHidden = false
  IsoVisible = false
  LockPosition = false
  Perspective = false
  Rotation = 0
  RotationVector = (1,0,0)
  ScaleType = 2
  SeamHidden = false
  SeamVisible = true
  SmoothHidden = false
  SmoothVisible = true
  Source = -> [Body005]
  Type = 8
  X = 31.7701
  XDirection = (0.707107,0.707107,0)
  Y = -0.823399
FEATURE [TechDraw::DrawProjGroup] ProjGroup005
  Anchor = -> ProjItem015
  AutoDistribute = false
  LockPosition = false
  ProjectionType = 0
  Rotation = 0
  ScaleType = 0
  Source = -> [Body005]
  Views = -> [ProjItem015,ProjItem016]
  X = 34.2764
  Y = 94.7144
  spacingX = 15
  spacingY = 15
FEATURE [TechDraw::DrawViewDimension] Dimension076
  Arbitrary = false
  ArbitraryTolerances = false
  EqualTolerance = true
  FormatSpec = %.2f
  FormatSpecOverTolerance = %+.2f
  FormatSpecUnderTolerance = %+.2f
  Inverted = false
  LockPosition = false
  MeasureType = 1
  OverTolerance = 0
  References2D = -> [ProjItem015]
  Rotation = 0
  ScaleType = 0
  TheoreticalExact = false
  Type = 0
  UnderTolerance = 0
  X = -14.5183
  Y = -1.62074
FEATURE [TechDraw::DrawViewDimension] Dimension077
  Arbitrary = false
  ArbitraryTolerances = false
  EqualTolerance = true
  FormatSpec = %.2f
  FormatSpecOverTolerance = %+.2f
  FormatSpecUnderTolerance = %+.2f
  Inverted = false
  LockPosition = false
  MeasureType = 1
  OverTolerance = 0
  References2D = -> [ProjItem015]
  Rotation = 0
  ScaleType = 0
  TheoreticalExact = false
  Type = 0
  UnderTolerance = 0
  X = -3.29934
  Y = 20.8885
FEATURE [TechDraw::DrawViewDimension] Dimension078
  Arbitrary = false
  ArbitraryTolerances = false
  EqualTolerance = true
  FormatSpec = ⌀%.2f
  FormatSpecOverTolerance = %+.2f
  FormatSpecUnderTolerance = %+.2f
  Inverted = false
  LockPosition = false
  MeasureType = 1
  OverTolerance = 0
  References2D = -> [ProjItem015]
  Rotation = 0
  ScaleType = 0
  TheoreticalExact = false
  Type = 5
  UnderTolerance = 0
  X = -5.26746
  Y = 2.63373
FEATURE [TechDraw::DrawViewDimension] Dimension079
  Arbitrary = false
  ArbitraryTolerances = false
  EqualTolerance = true
  FormatSpec = ⌀%.2f
  FormatSpecOverTolerance = %+.2f
  FormatSpecUnderTolerance = %+.2f
  Inverted = false
  LockPosition = false
  MeasureType = 1
  OverTolerance = 0
  References2D = -> [ProjItem015]
  Rotation = 0
  ScaleType = 0
  TheoreticalExact = false
  Type = 5
  UnderTolerance = 0
  X = 1.50499
  Y = 2.63373
FEATURE [TechDraw::DrawViewDimension] Dimension080
  Arbitrary = false
  ArbitraryTolerances = false
  EqualTolerance = true
  FormatSpec = %.2f
  FormatSpecOverTolerance = %+.2f
  FormatSpecUnderTolerance = %+.2f
  Inverted = false
  LockPosition = false
  MeasureType = 1
  OverTolerance = 0
  References2D = -> [ProjItem015]
  Rotation = 0
  ScaleType = 0
  TheoreticalExact = false
  Type = 1
  UnderTolerance = 0
  X = 3.27969
  Y = -15.3884
FEATURE [TechDraw::DrawViewDimension] Dimension081
  Arbitrary = false
  ArbitraryTolerances = false
  EqualTolerance = true
  FormatSpec = %.2f
  FormatSpecOverTolerance = %+.2f
  FormatSpecUnderTolerance = %+.2f
  Inverted = false
  LockPosition = false
  MeasureType = 1
  OverTolerance = 0
  References2D = -> [ProjItem015]
  Rotation = 0
  ScaleType = 0
  TheoreticalExact = false
  Type = 2
  UnderTolerance = 0
  X = 10.9739
  Y = -0.280286
FEATURE [TechDraw::DrawViewDimension] Dimension082
  Arbitrary = false
  ArbitraryTolerances = false
  EqualTolerance = true
  FormatSpec = %.2f
  FormatSpecOverTolerance = %+.2f
  FormatSpecUnderTolerance = %+.2f
  Inverted = false
  LockPosition = false
  MeasureType = 1
  OverTolerance = 0
  References2D = -> [ProjItem015]
  Rotation = 0
  ScaleType = 0
  TheoreticalExact = false
  Type = 2
  UnderTolerance = 0
  X = 10.8171
  Y = 9.68646
FEATURE [TechDraw::DrawViewAnnotation] Annotation005
  Font = osifont
  LineSpace = 80
  LockPosition = false
  MaxWidth = -1
  Rotation = 0
  ScaleType = 0
  Text = \u041d\u0430\u043a\u043e\u043d\u0435\u0447\u043d\u0438\u043a \u043d\u0430 \u043f\u043e\u0442\u0435\u043d\u0446\u0438\u043e\u043c\u0435\u0442\u0440  | \u0434\u043b\u044f \u043a\u0440\u0435\u043f\u043b\u0435\u043d\u0438\u044f \u0442\u044f\u0433\u0438 \u043e\u0442 \u043f\u0435\u0434\u0430\u043b\u0438. | \u042f \u0438\u0437\u0433\u043e\u0442\u043e\u0432\u0438\u043b \u0435\u0433\u043e \u0438\u0437 \u0444\u0430\u043d\u0435\u0440\u044b 6\u043c\u043c.
  TextSize = 5
  TextStyle = 0
  X = 53.4976
  Y = 61.1672
FEATURE [TechDraw::DrawViewDimension] Dimension083
  Arbitrary = false
  ArbitraryTolerances = false
  EqualTolerance = true
  FormatSpec = %.2f
  FormatSpecOverTolerance = %+.2f
  FormatSpecUnderTolerance = %+.2f
  Inverted = false
  LockPosition = false
  MeasureType = 1
  OverTolerance = 0
  References2D = -> [ProjItem011]
  Rotation = 0
  ScaleType = 0
  TheoreticalExact = false
  Type = 0
  UnderTolerance = 0
  X = 36.4765
  Y = 10.5346
FEATURE [TechDraw::DrawProjGroupItem] ProjItem017  label="Front006"
  CoarseView = false
  Direction = (1,0,0)
  Focus = 100
  HardHidden = false
  IsoCount = 0
  IsoHidden = false
  IsoVisible = false
  LockPosition = true
  Perspective = false
  Rotation = 0
  RotationVector = (0,1,0)
  ScaleType = 2
  SeamHidden = false
  SeamVisible = true
  SmoothHidden = false
  SmoothVisible = true
  Source = -> [Body006]
  Type = 0
  X = 0
  XDirection = (0,1,0)
  Y = 0
FEATURE [TechDraw::DrawProjGroup] ProjGroup006
  Anchor = -> ProjItem017
  AutoDistribute = true
  LockPosition = false
  ProjectionType = 0
  Rotation = 0
  ScaleType = 0
  Source = -> [Body006]
  Views = -> [ProjItem017]
  X = 152.655
  Y = 77.1052
  spacingX = 15
  spacingY = 15
FEATURE [TechDraw::DrawViewDimension] Dimension084
  Arbitrary = false
  ArbitraryTolerances = false
  EqualTolerance = true
  FormatSpec = %.2f
  FormatSpecOverTolerance = %+.2f
  FormatSpecUnderTolerance = %+.2f
  Inverted = false
  LockPosition = false
  MeasureType = 1
  OverTolerance = 0
  References2D = -> [ProjItem017]
  Rotation = 0
  ScaleType = 0
  TheoreticalExact = false
  Type = 0
  UnderTolerance = 0
  X = 8.50178
  Y = 13.3576
FEATURE [TechDraw::DrawViewDimension] Dimension085
  Arbitrary = false
  ArbitraryTolerances = false
  EqualTolerance = true
  FormatSpec = ⌀%.2f
  FormatSpecOverTolerance = %+.2f
  FormatSpecUnderTolerance = %+.2f
  Inverted = false
  LockPosition = false
  MeasureType = 1
  OverTolerance = 0
  References2D = -> [ProjItem017]
  Rotation = 0
  ScaleType = 0
  TheoreticalExact = false
  Type = 5
  UnderTolerance = 0
  X = 17.8717
  Y = -5.6437
FEATURE [TechDraw::DrawViewDimension] Dimension086
  Arbitrary = false
  ArbitraryTolerances = false
  EqualTolerance = true
  FormatSpec = ⌀%.2f
  FormatSpecOverTolerance = %+.2f
  FormatSpecUnderTolerance = %+.2f
  Inverted = false
  LockPosition = false
  MeasureType = 1
  OverTolerance = 0
  References2D = -> [ProjItem017]
  Rotation = 0
  ScaleType = 0
  TheoreticalExact = false
  Type = 5
  UnderTolerance = 0
  X = -16.743
  Y = 11.2874
FEATURE [TechDraw::DrawViewDimension] Dimension087
  Arbitrary = false
  ArbitraryTolerances = false
  EqualTolerance = true
  FormatSpec = %.2f
  FormatSpecOverTolerance = %+.2f
  FormatSpecUnderTolerance = %+.2f
  Inverted = false
  LockPosition = false
  MeasureType = 1
  OverTolerance = 0
  References2D = -> [ProjItem017]
  Rotation = 0
  ScaleType = 0
  TheoreticalExact = false
  Type = 0
  UnderTolerance = 0
  X = 40.248
  Y = -7.29196
FEATURE [TechDraw::DrawViewDimension] Dimension088
  Arbitrary = false
  ArbitraryTolerances = false
  EqualTolerance = true
  FormatSpec = %.2f
  FormatSpecOverTolerance = %+.2f
  FormatSpecUnderTolerance = %+.2f
  Inverted = false
  LockPosition = false
  MeasureType = 1
  OverTolerance = 0
  References2D = -> [ProjItem017]
  Rotation = 0
  ScaleType = 0
  TheoreticalExact = false
  Type = 0
  UnderTolerance = 0
  X = -37.7696
  Y = 18.8996
FEATURE [TechDraw::DrawViewAnnotation] Annotation006
  Font = osifont
  LineSpace = 80
  LockPosition = false
  MaxWidth = -1
  Rotation = 0
  ScaleType = 0
  Text = \u0420\u044b\u0447\u0430\u0433 \u043a\u0440\u0435\u043f\u043b\u0435\u043d\u0438\u044f | \u043f\u0435\u0434\u0430\u043b\u0438 \u043a \u043f\u043e\u0442\u0435\u043d\u0446\u0438\u043e\u043c\u0435\u0442\u0440\u0443. | \u041c\u043e\u0436\u043d\u043e \u0438\u0437\u0433\u043e\u0442\u043e\u0432\u0438\u0442\u044c \u0438\u0437  | \u043f\u0440\u043e\u0432\u043e\u043b\u043e\u043a\u0438 \u0438\u043b\u0438 \u0438\u0437 \u0432\u0435\u043b\u043e\u0441\u0435\u043f\u0435\u0434\u043d\u043e\u0439 \u0441\u043f\u0438\u0446\u044b.
  TextSize = 5
  TextStyle = 0
  X = 152.262
  Y = 57.0285
FEATURE [Part::FeaturePython] Clone009  label="Крепление пружины002"  # Draft clone (typed FeaturePython)
  AttacherType = Attacher::AttachEngine3D
  Fuse = false
  Objects = -> [_______________________004]
  Placement = pos=(-272,-100,0) rot=(1,0,0;0rad)
  Scale = (1,1,1)
FEATURE [TechDraw::DrawProjGroupItem] ProjItem018  label="Front007"
  CoarseView = false
  Direction = (0,0,1)
  Focus = 100
  HardHidden = false
  IsoCount = 0
  IsoHidden = false
  IsoVisible = false
  LockPosition = true
  Perspective = false
  Rotation = 0
  RotationVector = (1,0,0)
  ScaleType = 2
  SeamHidden = false
  SeamVisible = true
  SmoothHidden = false
  SmoothVisible = true
  Source = -> [Clone009]
  Type = 0
  X = 0
  XDirection = (1,0,0)
  Y = 0
FEATURE [TechDraw::DrawProjGroupItem] ProjItem019  label="Left003"
  CoarseView = false
  Direction = (-1,0,1e-16)
  Focus = 100
  HardHidden = false
  IsoCount = 0
  IsoHidden = false
  IsoVisible = false
  LockPosition = false
  Perspective = false
  Rotation = 0
  RotationVector = (1,0,0)
  ScaleType = 2
  SeamHidden = false
  SeamVisible = true
  SmoothHidden = false
  SmoothVisible = true
  Source = -> [Clone009]
  Type = 1
  X = 37.2697
  XDirection = (1e-16,0,1)
  Y = 0
FEATURE [TechDraw::DrawProjGroupItem] ProjItem020  label="Top"
  CoarseView = false
  Direction = (0,1,0)
  Focus = 100
  HardHidden = false
  IsoCount = 0
  IsoHidden = false
  IsoVisible = false
  LockPosition = false
  Perspective = false
  Rotation = 0
  RotationVector = (1,0,0)
  ScaleType = 2
  SeamHidden = false
  SeamVisible = true
  SmoothHidden = false
  SmoothVisible = true
  Source = -> [Clone009]
  Type = 4
  X = 0
  XDirection = (1,0,0)
  Y = -39.0935
FEATURE [TechDraw::DrawProjGroupItem] ProjItem021  label="FrontTopLeft002"
  CoarseView = false
  Direction = (-0.57735,0.57735,0.57735)
  Focus = 100
  HardHidden = false
  IsoCount = 0
  IsoHidden = false
  IsoVisible = false
  LockPosition = false
  Perspective = false
  Rotation = 0
  RotationVector = (1,0,0)
  ScaleType = 2
  SeamHidden = false
  SeamVisible = true
  SmoothHidden = false
  SmoothVisible = true
  Source = -> [Clone009]
  Type = 6
  X = 40.2121
  XDirection = (0.707107,0,0.707107)
  Y = -37.1206
FEATURE [TechDraw::DrawProjGroup] ProjGroup007
  Anchor = -> ProjItem018
  AutoDistribute = true
  LockPosition = false
  ProjectionType = 0
  Rotation = 0
  ScaleType = 0
  Source = -> [Clone009]
  Views = -> [ProjItem018,ProjItem019,ProjItem020,ProjItem021]
  X = 227.733
  Y = 78.5889
  spacingX = 15
  spacingY = 15
FEATURE [TechDraw::DrawViewDimension] Dimension089
  Arbitrary = false
  ArbitraryTolerances = false
  EqualTolerance = true
  FormatSpec = %.2f
  FormatSpecOverTolerance = %+.2f
  FormatSpecUnderTolerance = %+.2f
  Inverted = false
  LockPosition = false
  MeasureType = 1
  OverTolerance = 0
  References2D = -> [ProjItem018]
  Rotation = 0
  ScaleType = 0
  TheoreticalExact = false
  Type = 2
  UnderTolerance = 0
  X = -18.7318
  Y = 0.593507
FEATURE [TechDraw::DrawViewDimension] Dimension090
  Arbitrary = false
  ArbitraryTolerances = false
  EqualTolerance = true
  FormatSpec = %.2f
  FormatSpecOverTolerance = %+.2f
  FormatSpecUnderTolerance = %+.2f
  Inverted = false
  LockPosition = false
  MeasureType = 1
  OverTolerance = 0
  References2D = -> [ProjItem018]
  Rotation = 0
  ScaleType = 0
  TheoreticalExact = false
  Type = 1
  UnderTolerance = 0
  X = 0.296754
  Y = -14.5773
FEATURE [TechDraw::DrawViewDimension] Dimension091
  Arbitrary = false
  ArbitraryTolerances = false
  EqualTolerance = true
  FormatSpec = %.2f
  FormatSpecOverTolerance = %+.2f
  FormatSpecUnderTolerance = %+.2f
  Inverted = false
  LockPosition = false
  MeasureType = 1
  OverTolerance = 0
  References2D = -> [ProjItem019]
  Rotation = 0
  ScaleType = 0
  TheoreticalExact = false
  Type = 1
  UnderTolerance = 0
  X = 0.296754
  Y = -13.3903
FEATURE [TechDraw::DrawViewDimension] Dimension092
  Arbitrary = false
  ArbitraryTolerances = false
  EqualTolerance = true
  FormatSpec = ⌀%.2f
  FormatSpecOverTolerance = %+.2f
  FormatSpecUnderTolerance = %+.2f
  Inverted = false
  LockPosition = false
  MeasureType = 1
  OverTolerance = 0
  References2D = -> [ProjItem019]
  Rotation = 0
  ScaleType = 0
  TheoreticalExact = false
  Type = 5
  UnderTolerance = 0
  X = 5.93507
  Y = -2.07728
FEATURE [TechDraw::DrawViewDimension] Dimension093
  Arbitrary = false
  ArbitraryTolerances = false
  EqualTolerance = true
  FormatSpec = %.2f
  FormatSpecOverTolerance = %+.2f
  FormatSpecUnderTolerance = %+.2f
  Inverted = false
  LockPosition = false
  MeasureType = 1
  OverTolerance = 0
  References2D = -> [ProjItem019]
  Rotation = 0
  ScaleType = 0
  TheoreticalExact = false
  Type = 2
  UnderTolerance = 0
  X = 14.2442
  Y = -0.699365
FEATURE [TechDraw::DrawViewDimension] Dimension094
  Arbitrary = false
  ArbitraryTolerances = false
  EqualTolerance = true
  FormatSpec = ⌀%.2f
  FormatSpecOverTolerance = %+.2f
  FormatSpecUnderTolerance = %+.2f
  Inverted = false
  LockPosition = false
  MeasureType = 1
  OverTolerance = 0
  References2D = -> [ProjItem020]
  Rotation = 0
  ScaleType = 0
  TheoreticalExact = false
  Type = 5
  UnderTolerance = 0
  X = 11.8701
  Y = 8.60586
FEATURE [TechDraw::DrawViewDimension] Dimension095
  Arbitrary = false
  ArbitraryTolerances = false
  EqualTolerance = true
  FormatSpec = %.2f
  FormatSpecOverTolerance = %+.2f
  FormatSpecUnderTolerance = %+.2f
  Inverted = false
  LockPosition = false
  MeasureType = 1
  OverTolerance = 0
  References2D = -> [ProjItem020]
  Rotation = 0
  ScaleType = 0
  TheoreticalExact = false
  Type = 2
  UnderTolerance = 0
  X = -19.6221
  Y = 1.18701
FEATURE [TechDraw::DrawViewDimension] Dimension096
  Arbitrary = false
  ArbitraryTolerances = false
  EqualTolerance = true
  FormatSpec = %.2f
  FormatSpecOverTolerance = %+.2f
  FormatSpecUnderTolerance = %+.2f
  Inverted = false
  LockPosition = false
  MeasureType = 1
  OverTolerance = 0
  References2D = -> [ProjItem020]
  Rotation = 0
  ScaleType = 0
  TheoreticalExact = false
  Type = 1
  UnderTolerance = 0
  X = -0.331274
  Y = -11.7392
FEATURE [TechDraw::DrawPage] Page002  label="Механизм педали 1:1"
  KeepUpdated = true
  NextBalloonIndex = 1
  ProjectionType = 0
  Template = -> Template002
  Views = -> [ProjGroup003,Dimension071,Dimension072,Dimension073,Annotation002,ProjGroup004,Dimension074,Dimension075,Annotation003,ProjGroup005,Dimension076,Dimension077,Dimension078,Dimension079,Dimension080,Dimension081,Dimension082,Annotation005,Dimension083,ProjGroup006,Dimension084,Dimension085,Dimension086,Dimension087,Dimension088,Annotation006,ProjGroup007,Dimension089,Dimension090,Dimension091,+5 more]
FEATURE [TechDraw::DrawViewDetail] Detail
  AnchorPoint = (2.54,-79.38,0)
  BaseView = -> ProjItem006
  CoarseView = false
  Direction = (-1,-1e-16,0)
  Focus = 100
  HardHidden = false
  IsoCount = 0
  IsoHidden = false
  IsoVisible = false
  LockPosition = false
  Perspective = false
  Radius = 25
  Reference = 1
  Rotation = 0
  ScaleType = 2
  SeamHidden = false
  SeamVisible = true
  SmoothHidden = false
  SmoothVisible = true
  Source = -> [Clone008]
  X = 87.6198
  XDirection = (1e-16,-1,0)
  Y = 46.3203
FEATURE [TechDraw::DrawViewDimension] Dimension097
  Arbitrary = false
  ArbitraryTolerances = false
  EqualTolerance = true
  FormatSpec = %.2f
  FormatSpecOverTolerance = %+.2f
  FormatSpecUnderTolerance = %+.2f
  Inverted = false
  LockPosition = false
  MeasureType = 1
  OverTolerance = 0
  References2D = -> [Detail]
  Rotation = 0
  ScaleType = 0
  TheoreticalExact = false
  Type = 2
  UnderTolerance = 0
  X = -20.0729
  Y = 4.24721
FEATURE [TechDraw::DrawViewDimension] Dimension098
  Arbitrary = false
  ArbitraryTolerances = false
  EqualTolerance = true
  FormatSpec = %.2f
  FormatSpecOverTolerance = %+.2f
  FormatSpecUnderTolerance = %+.2f
  Inverted = false
  LockPosition = false
  MeasureType = 1
  OverTolerance = 0
  References2D = -> [Detail]
  Rotation = 0
  ScaleType = 0
  TheoreticalExact = false
  Type = 2
  UnderTolerance = 0
  X = -17.7327
  Y = -8.67651
FEATURE [TechDraw::DrawViewDimension] Dimension099
  Arbitrary = false
  ArbitraryTolerances = false
  EqualTolerance = true
  FormatSpec = %.2f
  FormatSpecOverTolerance = %+.2f
  FormatSpecUnderTolerance = %+.2f
  Inverted = false
  LockPosition = false
  MeasureType = 1
  OverTolerance = 0
  References2D = -> [Detail]
  Rotation = 0
  ScaleType = 0
  TheoreticalExact = false
  Type = 1
  UnderTolerance = 0
  X = 12.1104
  Y = -24.1762
FEATURE [TechDraw::DrawViewDimension] Dimension100
  Arbitrary = false
  ArbitraryTolerances = false
  EqualTolerance = true
  FormatSpec = %.2f
  FormatSpecOverTolerance = %+.2f
  FormatSpecUnderTolerance = %+.2f
  Inverted = false
  LockPosition = false
  MeasureType = 1
  OverTolerance = 0
  References2D = -> [Detail]
  Rotation = 0
  ScaleType = 0
  TheoreticalExact = false
  Type = 1
  UnderTolerance = 0
  X = -19.1522
  Y = -18.6149
FEATURE [TechDraw::DrawViewDimension] Dimension101
  Arbitrary = false
  ArbitraryTolerances = false
  EqualTolerance = true
  FormatSpec = %.2f
  FormatSpecOverTolerance = %+.2f
  FormatSpecUnderTolerance = %+.2f
  Inverted = false
  LockPosition = false
  MeasureType = 1
  OverTolerance = 0
  References2D = -> [Detail]
  Rotation = 0
  ScaleType = 0
  TheoreticalExact = false
  Type = 6
  UnderTolerance = 0
  X = 2.22501
  Y = 0.581239
FEATURE [TechDraw::DrawViewDimension] Dimension102
  Arbitrary = false
  ArbitraryTolerances = false
  EqualTolerance = true
  FormatSpec = %.2f
  FormatSpecOverTolerance = %+.2f
  FormatSpecUnderTolerance = %+.2f
  Inverted = false
  LockPosition = false
  MeasureType = 1
  OverTolerance = 0
  References2D = -> [Detail]
  Rotation = 0
  ScaleType = 0
  TheoreticalExact = false
  Type = 6
  UnderTolerance = 0
  X = -4.4499
  Y = 16.6622
FEATURE [TechDraw::DrawPage] Page001  label="Конструкция педали 1:2"
  KeepUpdated = true
  NextBalloonIndex = 1
  ProjectionType = 0
  Template = -> Template
  Views = -> [ProjGroup001,Dimension013,Dimension014,Dimension017,Dimension021,Dimension022,Dimension023,Dimension032,Dimension035,ProjGroup,Dimension,Dimension036,Dimension037,Dimension038,Dimension039,Dimension040,Dimension041,Dimension042,Dimension043,Dimension044,Dimension045,Dimension046,Dimension047,Dimension048,Dimension049,Dimension050,Dimension051,Dimension052,Dimension053,Dimension054,Dimension055,+16 more]
FEATURE [TechDraw::DrawSVGTemplate] Template003
  Height = 297
  Orientation = 0
  Width = 210
FEATURE [TechDraw::DrawProjGroupItem] ProjItem022  label="Front008"
  CoarseView = false
  Direction = (1,0,0)
  Focus = 100
  HardHidden = false
  IsoCount = 0
  IsoHidden = false
  IsoVisible = false
  LockPosition = true
  Perspective = false
  Rotation = 0
  RotationVector = (0,1,0)
  Scale = 0.5
  ScaleType = 2
  SeamHidden = false
  SeamVisible = true
  SmoothHidden = false
  SmoothVisible = true
  Source = -> [Part002]
  Type = 0
  X = 0
  XDirection = (0,1,0)
  Y = 0
FEATURE [TechDraw::DrawProjGroupItem] ProjItem023  label="Bottom002"
  CoarseView = false
  Direction = (0,0,-1)
  Focus = 100
  HardHidden = false
  IsoCount = 0
  IsoHidden = false
  IsoVisible = false
  LockPosition = false
  Perspective = false
  Rotation = 0
  RotationVector = (1,0,0)
  ScaleType = 2
  SeamHidden = false
  SeamVisible = true
  SmoothHidden = false
  SmoothVisible = true
  Source = -> [Part002]
  Type = 5
  X = 0
  XDirection = (0,1,0)
  Y = -81.7786
FEATURE [TechDraw::DrawProjGroup] ProjGroup008
  Anchor = -> ProjItem022
  AutoDistribute = false
  LockPosition = false
  ProjectionType = 0
  Rotation = 0
  Scale = 0.5
  ScaleType = 2
  Source = -> [Part002]
  Views = -> [ProjItem022,ProjItem023]
  X = 105
  Y = 239.071
  spacingX = 15
  spacingY = 15
FEATURE [TechDraw::DrawViewSection] SectionView001  label="Section  - 001"
  BaseView = -> ProjItem023
  CoarseView = false
  CutSurfaceDisplay = 2
  Direction = (1,0,0)
  FileGeomPattern = <path>
  FileHatchPattern = <path>
  Focus = 100
  FuseBeforeCut = false
  HardHidden = false
  HatchScale = 1
  IsoCount = 0
  IsoHidden = false
  IsoVisible = false
  LockPosition = false
  NameGeomPattern = Алмаз
  Perspective = false
  Rotation = 0
  Scale = 0.5
  ScaleType = 0
  SeamHidden = false
  SeamVisible = true
  SectionDirection = 3
  SectionNormal = (1,0,0)
  SectionOrigin = (-45,-113,79.62)
  SmoothHidden = false
  SmoothVisible = true
  Source = -> [Part002]
  X = 124.156
  XDirection = (0,1,0)
  Y = 65.1167
FEATURE [TechDraw::DrawViewDimension] Dimension103
  Arbitrary = false
  ArbitraryTolerances = false
  EqualTolerance = true
  FormatSpec = %.2f
  FormatSpecOverTolerance = %+.2f
  FormatSpecUnderTolerance = %+.2f
  Inverted = false
  LockPosition = false
  MeasureType = 1
  OverTolerance = 0
  References2D = -> [SectionView001]
  Rotation = 0
  ScaleType = 0
  TheoreticalExact = false
  Type = 0
  UnderTolerance = 0
  X = 9.02679
  Y = -14.0953
FEATURE [TechDraw::DrawViewAnnotation] Annotation007
  Font = osifont
  LineSpace = 80
  LockPosition = false
  MaxWidth = -1
  Rotation = 0
  ScaleType = 0
  Text = \u042d\u0442\u043e \u043f\u043e\u043a\u0430 \u0447\u0442\u043e \u0442\u043e\u043b\u044c\u043a\u043e \u0438\u0434\u0435\u044f, | \u044f \u0435\u0449\u0435 \u043d\u0435 \u0434\u0430\u043b\u0430\u043b \u0442\u0430\u043a\u0443\u044e \u043f\u0435\u0434\u0430\u043b\u044c. | \u0418\u0434\u0435\u044f \u0432 \u0442\u043e\u043c \u0447\u0442\u043e\u0431\u044b \u043f\u0435\u0434\u0430\u043b\u044c | \u0440\u0430\u0431\u043e\u0442\u0430\u043b\u0430 \u0441 \u044d\u0444\u0444\u0435\u043a\u0442\u043e\u043c \u043a\u043e\u0440\u0437\u0438\u043d\u044b. | \u0418\u0434\u0435\u044e \u043f\u043e\u0434\u0441\u043c\u043e\u0442\u0440\u0435\u043b \u0443 \u043f\u0435\u0434\u0430\u0442\u043b\u0435\u0439  caravangoes. | \u041f\u043e \u0438\u0434\u0435\u0438 \u0432 \u043a\u043e\u043d\u0446\u0435 \u0448\u0442\u043e\u043a | \u0434\u043e\u043b\u0436\u0435\u043d \u043f\u0440\u0443\u0436\u0438\u043d\u0438\u0442\u044c \u0432\u0432\u0435\u0440\u0445.
  TextSize = 5
  TextStyle = 0
  X = 71.2566
  Y = 102.19
FEATURE [TechDraw::DrawViewDimension] Dimension104
  Arbitrary = false
  ArbitraryTolerances = false
  EqualTolerance = true
  FormatSpec = %.2f
  FormatSpecOverTolerance = %+.2f
  FormatSpecUnderTolerance = %+.2f
  Inverted = false
  LockPosition = false
  MeasureType = 1
  OverTolerance = 0
  References2D = -> [ProjItem022]
  Rotation = 0
  ScaleType = 0
  TheoreticalExact = false
  Type = 0
  UnderTolerance = 0
  X = 46.4563
  Y = -17.6771
FEATURE [TechDraw::DrawViewDimension] Dimension105
  Arbitrary = false
  ArbitraryTolerances = false
  EqualTolerance = true
  FormatSpec = %.2f
  FormatSpecOverTolerance = %+.2f
  FormatSpecUnderTolerance = %+.2f
  Inverted = false
  LockPosition = false
  MeasureType = 1
  OverTolerance = 0
  References2D = -> [ProjItem022]
  Rotation = 0
  ScaleType = 0
  TheoreticalExact = false
  Type = 1
  UnderTolerance = 0
  X = 20.7682
  Y = 8.33101
FEATURE [TechDraw::DrawViewDimension] Dimension106
  Arbitrary = false
  ArbitraryTolerances = false
  EqualTolerance = true
  FormatSpec = ⌀%.2f
  FormatSpecOverTolerance = %+.2f
  FormatSpecUnderTolerance = %+.2f
  Inverted = false
  LockPosition = false
  MeasureType = 1
  OverTolerance = 0
  References2D = -> [ProjItem022]
  Rotation = 0
  ScaleType = 0
  TheoreticalExact = false
  Type = 5
  UnderTolerance = 0
  X = 24.2503
  Y = -8.46836
FEATURE [TechDraw::DrawViewDimension] Dimension107
  Arbitrary = false
  ArbitraryTolerances = false
  EqualTolerance = true
  FormatSpec = ⌀%.2f
  FormatSpecOverTolerance = %+.2f
  FormatSpecUnderTolerance = %+.2f
  Inverted = false
  LockPosition = false
  MeasureType = 1
  OverTolerance = 0
  References2D = -> [ProjItem022]
  Rotation = 0
  ScaleType = 0
  TheoreticalExact = false
  Type = 5
  UnderTolerance = 0
  X = 34.515
  Y = -28.4845
FEATURE [TechDraw::DrawViewDimension] Dimension108
  Arbitrary = false
  ArbitraryTolerances = false
  EqualTolerance = true
  FormatSpec = ⌀%.2f
  FormatSpecOverTolerance = %+.2f
  FormatSpecUnderTolerance = %+.2f
  Inverted = false
  LockPosition = false
  MeasureType = 1
  OverTolerance = 0
  References2D = -> [ProjItem022]
  Rotation = 0
  ScaleType = 0
  TheoreticalExact = false
  Type = 5
  UnderTolerance = 0
  X = 39.7756
  Y = -25.4051
FEATURE [TechDraw::DrawViewDimension] Dimension109
  Arbitrary = false
  ArbitraryTolerances = false
  EqualTolerance = true
  FormatSpec = %.2f
  FormatSpecOverTolerance = %+.2f
  FormatSpecUnderTolerance = %+.2f
  Inverted = false
  LockPosition = false
  MeasureType = 1
  OverTolerance = 0
  References2D = -> [ProjItem022]
  Rotation = 0
  ScaleType = 0
  TheoreticalExact = false
  Type = 6
  UnderTolerance = 0
  X = 27.4573
  Y = -4.23418
FEATURE [TechDraw::DrawViewDimension] Dimension110
  Arbitrary = false
  ArbitraryTolerances = false
  EqualTolerance = true
  FormatSpec = %.2f
  FormatSpecOverTolerance = %+.2f
  FormatSpecUnderTolerance = %+.2f
  Inverted = false
  LockPosition = false
  MeasureType = 1
  OverTolerance = 0
  References2D = -> [ProjItem022]
  Rotation = 0
  ScaleType = 0
  TheoreticalExact = false
  Type = 6
  UnderTolerance = 0
  X = 48.9624
  Y = -37.9793
FEATURE [TechDraw::DrawViewDimension] Dimension111
  Arbitrary = false
  ArbitraryTolerances = false
  EqualTolerance = true
  FormatSpec = %.2f
  FormatSpecOverTolerance = %+.2f
  FormatSpecUnderTolerance = %+.2f
  Inverted = false
  LockPosition = false
  MeasureType = 1
  OverTolerance = 0
  References2D = -> [ProjItem022]
  Rotation = 0
  ScaleType = 0
  TheoreticalExact = false
  Type = 1
  UnderTolerance = 0
  X = 41.802
  Y = -52.2605
FEATURE [TechDraw::DrawViewDimension] Dimension112
  Arbitrary = false
  ArbitraryTolerances = false
  EqualTolerance = true
  FormatSpec = %.2f
  FormatSpecOverTolerance = %+.2f
  FormatSpecUnderTolerance = %+.2f
  Inverted = false
  LockPosition = false
  MeasureType = 1
  OverTolerance = 0
  References2D = -> [ProjItem022]
  Rotation = 0
  ScaleType = 0
  TheoreticalExact = false
  Type = 2
  UnderTolerance = 0
  X = 16.49
  Y = -38.8689
FEATURE [TechDraw::DrawViewDimension] Dimension113
  Arbitrary = false
  ArbitraryTolerances = false
  EqualTolerance = true
  FormatSpec = %.2f
  FormatSpecOverTolerance = %+.2f
  FormatSpecUnderTolerance = %+.2f
  Inverted = false
  LockPosition = false
  MeasureType = 1
  OverTolerance = 0
  References2D = -> [ProjItem022]
  Rotation = 0
  ScaleType = 0
  TheoreticalExact = false
  Type = 1
  UnderTolerance = 0
  X = 28.6552
  Y = -45.2074
FEATURE [TechDraw::DrawViewDimension] Dimension114
  Arbitrary = false
  ArbitraryTolerances = false
  EqualTolerance = true
  FormatSpec = %.2f
  FormatSpecOverTolerance = %+.2f
  FormatSpecUnderTolerance = %+.2f
  Inverted = false
  LockPosition = false
  MeasureType = 1
  OverTolerance = 0
  References2D = -> [ProjItem022]
  Rotation = 0
  ScaleType = 0
  TheoreticalExact = false
  Type = 1
  UnderTolerance = 0
  X = 6.31996
  Y = -14.9117
FEATURE [TechDraw::DrawViewDimension] Dimension115
  Arbitrary = false
  ArbitraryTolerances = false
  EqualTolerance = true
  FormatSpec = %.2f
  FormatSpecOverTolerance = %+.2f
  FormatSpecUnderTolerance = %+.2f
  Inverted = false
  LockPosition = false
  MeasureType = 1
  OverTolerance = 0
  References2D = -> [ProjItem022]
  Rotation = 0
  ScaleType = 0
  TheoreticalExact = false
  Type = 2
  UnderTolerance = 0
  X = 6.32037
  Y = 2.26889
FEATURE [TechDraw::DrawPage] Page003  label="Педаль сцепления 1:2"
  KeepUpdated = true
  NextBalloonIndex = 1
  ProjectionType = 0
  Template = -> Template003
  Views = -> [ProjGroup008,SectionView001,Dimension103,Annotation007,Dimension104,Dimension105,Dimension106,Dimension107,Dimension108,Dimension109,Dimension110,Dimension111,Dimension112,Dimension113,Dimension114,Dimension115]
FEATURE [TechDraw::DrawSVGTemplate] Template004
  Height = 210
  Orientation = 1
  Width = 297
FEATURE [TechDraw::DrawProjGroupItem] ProjItem024  label="Front009"
  CoarseView = false
  Direction = (0,0,1)
  Focus = 100
  HardHidden = false
  IsoCount = 0
  IsoHidden = false
  IsoVisible = false
  LockPosition = true
  Perspective = false
  Rotation = 0
  RotationVector = (1,0,0)
  Scale = 0.25
  ScaleType = 2
  SeamHidden = false
  SeamVisible = true
  SmoothHidden = false
  SmoothVisible = true
  Source = -> [Body007]
  Type = 0
  X = 0
  XDirection = (1,0,0)
  Y = 0
FEATURE [TechDraw::DrawProjGroup] ProjGroup009
  Anchor = -> ProjItem024
  AutoDistribute = true
  LockPosition = false
  ProjectionType = 0
  Rotation = 0
  Scale = 0.25
  ScaleType = 2
  Source = -> [Body007]
  Views = -> [ProjItem024]
  X = 66.2622
  Y = 150.837
  spacingX = 15
  spacingY = 15
FEATURE [TechDraw::DrawViewAnnotation] Annotation008
  Font = osifont
  LineSpace = 80
  LockPosition = false
  MaxWidth = -1
  Rotation = 0
  ScaleType = 0
  Text = \u041e\u0441\u043d\u043e\u0432\u0430\u043d\u0438\u0435 \u0438\u0437 \u041b\u0414\u0421\u041f 16\u043c\u043c
  TextSize = 5
  TextStyle = 0
  X = 66.9706
  Y = 156.102
FEATURE [TechDraw::DrawViewDimension] Dimension116
  Arbitrary = false
  ArbitraryTolerances = false
  EqualTolerance = true
  FormatSpec = %.2f
  FormatSpecOverTolerance = %+.2f
  FormatSpecUnderTolerance = %+.2f
  Inverted = false
  LockPosition = false
  MeasureType = 1
  OverTolerance = 0
  References2D = -> [ProjItem024]
  Rotation = 0
  ScaleType = 0
  TheoreticalExact = false
  Type = 2
  UnderTolerance = 0
  X = 47.2481
  Y = 0
FEATURE [TechDraw::DrawViewDimension] Dimension117
  Arbitrary = false
  ArbitraryTolerances = false
  EqualTolerance = true
  FormatSpec = %.2f
  FormatSpecOverTolerance = %+.2f
  FormatSpecUnderTolerance = %+.2f
  Inverted = false
  LockPosition = false
  MeasureType = 1
  OverTolerance = 0
  References2D = -> [ProjItem024]
  Rotation = 0
  ScaleType = 0
  TheoreticalExact = false
  Type = 1
  UnderTolerance = 0
  X = 0
  Y = -46.6546
FEATURE [TechDraw::DrawProjGroupItem] ProjItem025  label="Front010"
  CoarseView = false
  Direction = (0,0,1)
  Focus = 100
  HardHidden = false
  IsoCount = 0
  IsoHidden = false
  IsoVisible = false
  LockPosition = true
  Perspective = false
  Rotation = 0
  RotationVector = (1,0,0)
  Scale = 0.25
  ScaleType = 2
  SeamHidden = false
  SeamVisible = true
  SmoothHidden = false
  SmoothVisible = true
  Source = -> [Body009]
  Type = 0
  X = 0
  XDirection = (1,0,0)
  Y = 0
FEATURE [TechDraw::DrawProjGroup] ProjGroup010
  Anchor = -> ProjItem025
  AutoDistribute = true
  LockPosition = false
  ProjectionType = 0
  Rotation = 0
  Scale = 0.25
  ScaleType = 2
  Source = -> [Body009]
  Views = -> [ProjItem025]
  X = 67.7508
  Y = 57.0186
  spacingX = 15
  spacingY = 15
FEATURE [TechDraw::DrawViewAnnotation] Annotation009
  Font = osifont
  LineSpace = 80
  LockPosition = false
  MaxWidth = -1
  Rotation = 0
  ScaleType = 0
  Text = \u041f\u043e\u0434\u0441\u0442\u0430\u0432\u043a\u0430 \u043f\u043e\u0434 \u043d\u043e\u0433\u0438 \u0438\u0437 \u0444\u0430\u043d\u0435\u0440\u044b 6\u043c\u043c. | \u041c\u043e\u0436\u043d\u043e \u0441\u0434\u0435\u043b\u0430\u0442\u044c \u0448\u0438\u0440\u0435 \u0447\u0435\u043c 140\u043c\u043c.  | \u041d\u043e \u0442\u043e\u0433\u0434\u0430 \u0432\u0441\u044f \u043a\u043e\u043d\u0441\u0442\u0440\u0443\u043a\u0446\u0438\u044f \u0431\u0443\u0434\u0435\u0442  | \u043c\u0430\u0441\u0441\u0438\u0432\u043d\u0435\u0435.
  TextSize = 5
  TextStyle = 0
  X = 69.1811
  Y = 55.2632
FEATURE [TechDraw::DrawViewDimension] Dimension118
  Arbitrary = false
  ArbitraryTolerances = false
  EqualTolerance = true
  FormatSpec = %.2f
  FormatSpecOverTolerance = %+.2f
  FormatSpecUnderTolerance = %+.2f
  Inverted = false
  LockPosition = false
  MeasureType = 1
  OverTolerance = 0
  References2D = -> [ProjItem025]
  Rotation = 0
  ScaleType = 0
  TheoreticalExact = false
  Type = 1
  UnderTolerance = 0
  X = 0
  Y = -24.6517
FEATURE [TechDraw::DrawViewDimension] Dimension119
  Arbitrary = false
  ArbitraryTolerances = false
  EqualTolerance = true
  FormatSpec = %.2f
  FormatSpecOverTolerance = %+.2f
  FormatSpecUnderTolerance = %+.2f
  Inverted = false
  LockPosition = false
  MeasureType = 1
  OverTolerance = 0
  References2D = -> [ProjItem025]
  Rotation = 0
  ScaleType = 0
  TheoreticalExact = false
  Type = 2
  UnderTolerance = 0
  X = 49.9768
  Y = -0.325077
FEATURE [TechDraw::DrawProjGroupItem] ProjItem026  label="Front011"
  CoarseView = false
  Direction = (0,0,1)
  Focus = 100
  HardHidden = false
  IsoCount = 0
  IsoHidden = false
  IsoVisible = false
  LockPosition = true
  Perspective = false
  Rotation = 0
  RotationVector = (1,0,0)
  Scale = 0.25
  ScaleType = 2
  SeamHidden = false
  SeamVisible = true
  SmoothHidden = false
  SmoothVisible = true
  Source = -> [Part003]
  Type = 0
  X = 0
  XDirection = (1,0,0)
  Y = 0
FEATURE [TechDraw::DrawProjGroupItem] ProjItem027  label="Left004"
  CoarseView = false
  Direction = (-1,0,1e-16)
  Focus = 100
  HardHidden = false
  IsoCount = 0
  IsoHidden = false
  IsoVisible = false
  LockPosition = false
  Perspective = false
  Rotation = 0
  RotationVector = (1,0,0)
  ScaleType = 2
  SeamHidden = false
  SeamVisible = true
  SmoothHidden = false
  SmoothVisible = true
  Source = -> [Part003]
  Type = 1
  X = 64
  XDirection = (1e-16,0,1)
  Y = 0
FEATURE [TechDraw::DrawProjGroupItem] ProjItem028  label="FrontTopLeft003"
  CoarseView = false
  Direction = (-0.57735,0.57735,0.57735)
  Focus = 100
  HardHidden = false
  IsoCount = 0
  IsoHidden = false
  IsoVisible = false
  LockPosition = false
  Perspective = false
  Rotation = 0
  RotationVector = (1,0,0)
  ScaleType = 2
  SeamHidden = false
  SeamVisible = true
  SmoothHidden = false
  SmoothVisible = true
  Source = -> [Part003]
  Type = 6
  X = 90.2005
  XDirection = (0.707107,0,0.707107)
  Y = -81.4134
FEATURE [TechDraw::DrawProjGroup] ProjGroup011
  Anchor = -> ProjItem026
  AutoDistribute = false
  LockPosition = false
  ProjectionType = 0
  Rotation = 0
  Scale = 0.25
  ScaleType = 2
  Source = -> [Part003]
  Views = -> [ProjItem026,ProjItem027,ProjItem028]
  X = 168.807
  Y = 149.305
  spacingX = 15
  spacingY = 15
FEATURE [TechDraw::DrawProjGroupItem] ProjItem029  label="Front012"
  CoarseView = false
  Direction = (1,0,0)
  Focus = 100
  HardHidden = false
  IsoCount = 0
  IsoHidden = false
  IsoVisible = false
  LockPosition = true
  Perspective = false
  Rotation = 0
  RotationVector = (0,1,0)
  Scale = 0.25
  ScaleType = 2
  SeamHidden = false
  SeamVisible = true
  SmoothHidden = false
  SmoothVisible = true
  Source = -> [Body008]
  Type = 0
  X = 0
  XDirection = (0,1,0)
  Y = 0
FEATURE [TechDraw::DrawProjGroup] ProjGroup012
  Anchor = -> ProjItem029
  AutoDistribute = true
  LockPosition = false
  ProjectionType = 0
  Rotation = 0
  Scale = 0.25
  ScaleType = 2
  Source = -> [Body008]
  Views = -> [ProjItem029]
  X = 149.212
  Y = 69.7457
  spacingX = 15
  spacingY = 15
FEATURE [TechDraw::DrawViewDimension] Dimension120
  Arbitrary = false
  ArbitraryTolerances = false
  EqualTolerance = true
  FormatSpec = %.2f
  FormatSpecOverTolerance = %+.2f
  FormatSpecUnderTolerance = %+.2f
  Inverted = false
  LockPosition = false
  MeasureType = 1
  OverTolerance = 0
  References2D = -> [ProjItem029]
  Rotation = 0
  ScaleType = 0
  TheoreticalExact = false
  Type = 1
  UnderTolerance = 0
  X = 0
  Y = -5.63124
FEATURE [TechDraw::DrawViewDimension] Dimension121
  Arbitrary = false
  ArbitraryTolerances = false
  EqualTolerance = true
  FormatSpec = %.2f
  FormatSpecOverTolerance = %+.2f
  FormatSpecUnderTolerance = %+.2f
  Inverted = false
  LockPosition = false
  MeasureType = 1
  OverTolerance = 0
  References2D = -> [ProjItem029]
  Rotation = 0
  ScaleType = 0
  TheoreticalExact = false
  Type = 2
  UnderTolerance = 0
  X = -22.7675
  Y = 1.12874
FEATURE [TechDraw::DrawProjGroupItem] ProjItem030  label="Front013"
  CoarseView = false
  Direction = (1,0,0)
  Focus = 100
  HardHidden = false
  IsoCount = 0
  IsoHidden = false
  IsoVisible = false
  LockPosition = true
  Perspective = false
  Rotation = 0
  RotationVector = (0,1,0)
  Scale = 0.25
  ScaleType = 2
  SeamHidden = false
  SeamVisible = true
  SmoothHidden = false
  SmoothVisible = true
  Source = -> [Body013]
  Type = 0
  X = 0
  XDirection = (0,1,0)
  Y = 0
FEATURE [TechDraw::DrawProjGroup] ProjGroup013
  Anchor = -> ProjItem030
  AutoDistribute = true
  LockPosition = false
  ProjectionType = 0
  Rotation = 0
  Scale = 0.25
  ScaleType = 2
  Source = -> [Body013]
  Views = -> [ProjItem030]
  X = 189.887
  Y = 69.6328
  spacingX = 15
  spacingY = 15
FEATURE [TechDraw::DrawViewAnnotation] Annotation010
  Font = osifont
  LineSpace = 80
  LockPosition = false
  MaxWidth = -1
  Rotation = 0
  ScaleType = 0
  Text = 2\u0425
  TextSize = 5
  TextStyle = 0
  X = 148.688
  Y = 67.5634
FEATURE [TechDraw::DrawViewDimension] Dimension122
  Arbitrary = false
  ArbitraryTolerances = false
  EqualTolerance = true
  FormatSpec = %.2f
  FormatSpecOverTolerance = %+.2f
  FormatSpecUnderTolerance = %+.2f
  Inverted = false
  LockPosition = false
  MeasureType = 1
  OverTolerance = 0
  References2D = -> [ProjItem030]
  Rotation = 0
  ScaleType = 0
  TheoreticalExact = false
  Type = 1
  UnderTolerance = 0
  X = 0
  Y = -6.57185
FEATURE [TechDraw::DrawViewDimension] Dimension123
  Arbitrary = false
  ArbitraryTolerances = false
  EqualTolerance = true
  FormatSpec = %.2f
  FormatSpecOverTolerance = %+.2f
  FormatSpecUnderTolerance = %+.2f
  Inverted = false
  LockPosition = false
  MeasureType = 1
  OverTolerance = 0
  References2D = -> [ProjItem030]
  Rotation = 0
  ScaleType = 0
  TheoreticalExact = false
  Type = 2
  UnderTolerance = 0
  X = 16.8268
  Y = 0
FEATURE [TechDraw::DrawViewAnnotation] Annotation011
  Font = osifont
  LineSpace = 80
  LockPosition = false
  MaxWidth = -1
  Rotation = 0
  ScaleType = 0
  Text = \u0414\u0432\u0435 \u0431\u043e\u043a\u043e\u0432\u044b\u0435 \u043a\u0440\u044b\u0448\u043a\u0438 \u0438\u0437 \u041b\u0414\u0421\u041f. | \u0418 \u043e\u0434\u043d\u0430 \u043f\u043e\u0434\u043f\u043e\u0440\u043a\u0430 \u043f\u043e \u0446\u0435\u043d\u0442\u0440\u0443,  | \u0447\u0442\u043e\u0431\u044b \u043d\u0435 \u043f\u0440\u043e\u0433\u0438\u0431\u0430\u043b\u0430\u0441\u044c \u0444\u0430\u043d\u0435\u0440\u0430.
  TextSize = 5
  TextStyle = 0
  X = 167.312
  Y = 35.3943
FEATURE [TechDraw::DrawPage] Page004  label="Корпус 1:4"
  KeepUpdated = true
  NextBalloonIndex = 1
  ProjectionType = 0
  Template = -> Template004
  Views = -> [ProjGroup009,Annotation008,Dimension116,Dimension117,ProjGroup010,Annotation009,Dimension118,Dimension119,ProjGroup011,ProjGroup012,Dimension120,Dimension121,ProjGroup013,Annotation010,Dimension122,Dimension123,Annotation011]
FEATURE [TechDraw::DrawSVGTemplate] Template005
  Height = 210
  Orientation = 1
  Width = 297
FEATURE [TechDraw::DrawProjGroupItem] ProjItem031  label="Front014"
  CoarseView = false
  Direction = (1,0,0)
  Focus = 100
  HardHidden = false
  IsoCount = 0
  IsoHidden = false
  IsoVisible = false
  LockPosition = true
  Perspective = false
  Rotation = 0
  RotationVector = (0,1,0)
  Scale = 0.25
  ScaleType = 2
  SeamHidden = false
  SeamVisible = true
  SmoothHidden = false
  SmoothVisible = true
  Source = -> [Part]
  Type = 0
  X = 0
  XDirection = (0,1,0)
  Y = 0
FEATURE [TechDraw::DrawProjGroupItem] ProjItem032  label="Right"
  CoarseView = false
  Direction = (1e-16,1,0)
  Focus = 100
  HardHidden = false
  IsoCount = 0
  IsoHidden = false
  IsoVisible = false
  LockPosition = false
  Perspective = false
  Rotation = 0
  RotationVector = (1,0,0)
  ScaleType = 2
  SeamHidden = false
  SeamVisible = true
  SmoothHidden = false
  SmoothVisible = true
  Source = -> [Part]
  Type = 2
  X = -92.0873
  XDirection = (-1,1e-16,0)
  Y = 0
FEATURE [TechDraw::DrawProjGroupItem] ProjItem033  label="Left005"
  CoarseView = false
  Direction = (1e-16,-1,0)
  Focus = 100
  HardHidden = false
  IsoCount = 0
  IsoHidden = false
  IsoVisible = false
  LockPosition = false
  Perspective = false
  Rotation = 0
  RotationVector = (1,0,0)
  ScaleType = 2
  SeamHidden = false
  SeamVisible = true
  SmoothHidden = false
  SmoothVisible = true
  Source = -> [Part]
  Type = 1
  X = 91.4076
  XDirection = (1,1e-16,0)
  Y = 0
FEATURE [TechDraw::DrawProjGroupItem] ProjItem034  label="FrontTopLeft004"
  CoarseView = false
  Direction = (0.57735,-0.57735,0.57735)
  Focus = 100
  HardHidden = false
  IsoCount = 0
  IsoHidden = false
  IsoVisible = false
  LockPosition = false
  Perspective = false
  Rotation = 0
  RotationVector = (1,0,0)
  ScaleType = 2
  SeamHidden = false
  SeamVisible = true
  SmoothHidden = false
  SmoothVisible = true
  Source = -> [Part]
  Type = 6
  X = 77.3569
  XDirection = (0.707107,0.707107,0)
  Y = -88.6747
FEATURE [TechDraw::DrawProjGroupItem] ProjItem035  label="FrontTopRight"
  CoarseView = false
  Direction = (0.57735,0.57735,0.57735)
  Focus = 100
  HardHidden = false
  IsoCount = 0
  IsoHidden = false
  IsoVisible = false
  LockPosition = false
  Perspective = false
  Rotation = 0
  RotationVector = (1,0,0)
  ScaleType = 2
  SeamHidden = false
  SeamVisible = true
  SmoothHidden = false
  SmoothVisible = true
  Source = -> [Part]
  Type = 7
  X = -75.1574
  XDirection = (-0.707107,0.707107,0)
  Y = -95.8704
FEATURE [TechDraw::DrawProjGroup] ProjGroup014
  Anchor = -> ProjItem031
  AutoDistribute = false
  LockPosition = false
  ProjectionType = 0
  Rotation = 0
  Scale = 0.25
  ScaleType = 2
  Source = -> [Part]
  Views = -> [ProjItem031,ProjItem032,ProjItem033,ProjItem034,ProjItem035]
  X = 151.734
  Y = 166.839
  spacingX = 15
  spacingY = 15
FEATURE [TechDraw::DrawViewDimension] Dimension126
  Arbitrary = false
  ArbitraryTolerances = false
  EqualTolerance = true
  FormatSpec = %.2f
  FormatSpecOverTolerance = %+.2f
  FormatSpecUnderTolerance = %+.2f
  Inverted = false
  LockPosition = false
  MeasureType = 1
  OverTolerance = 0
  References2D = -> [ProjItem032]
  Rotation = 0
  ScaleType = 0
  TheoreticalExact = false
  Type = 1
  UnderTolerance = 0
  X = -40.5362
  Y = 4.24805
FEATURE [TechDraw::DrawViewDimension] Dimension133
  Arbitrary = false
  ArbitraryTolerances = false
  EqualTolerance = true
  FormatSpec = %.2f
  FormatSpecOverTolerance = %+.2f
  FormatSpecUnderTolerance = %+.2f
  Inverted = false
  LockPosition = false
  MeasureType = 1
  OverTolerance = 0
  References2D = -> [ProjItem032]
  Rotation = 0
  ScaleType = 0
  TheoreticalExact = false
  Type = 1
  UnderTolerance = 0
  X = -31.7804
  Y = 31.4983
FEATURE [TechDraw::DrawViewDimension] Dimension134
  Arbitrary = false
  ArbitraryTolerances = false
  EqualTolerance = true
  FormatSpec = %.2f
  FormatSpecOverTolerance = %+.2f
  FormatSpecUnderTolerance = %+.2f
  Inverted = false
  LockPosition = false
  MeasureType = 1
  OverTolerance = 0
  References2D = -> [ProjItem009]
  Rotation = 0
  ScaleType = 0
  TheoreticalExact = false
  Type = 0
  UnderTolerance = 0
  X = 13.5053
  Y = 24.7338
FEATURE [TechDraw::DrawPage] Page  label="Педаль в разрезе и полностью 1:2"
  KeepUpdated = true
  NextBalloonIndex = 1
  ProjectionType = 0
  Template = -> Template001
  Views = -> [ProjGroup002,SectionView,Dimension067,Dimension068,Dimension069,Dimension070,Annotation004,Dimension134]
FEATURE [TechDraw::DrawViewDimension] Dimension135
  Arbitrary = false
  ArbitraryTolerances = false
  EqualTolerance = true
  FormatSpec = %.2f
  FormatSpecOverTolerance = %+.2f
  FormatSpecUnderTolerance = %+.2f
  Inverted = false
  LockPosition = false
  MeasureType = 1
  OverTolerance = 0
  References2D = -> [ProjItem032]
  Rotation = 0
  ScaleType = 0
  TheoreticalExact = false
  Type = 1
  UnderTolerance = 0
  X = -15.7381
  Y = -3.6507
FEATURE [TechDraw::DrawViewDimension] Dimension136
  Arbitrary = false
  ArbitraryTolerances = false
  EqualTolerance = true
  FormatSpec = %.2f
  FormatSpecOverTolerance = %+.2f
  FormatSpecUnderTolerance = %+.2f
  Inverted = false
  LockPosition = false
  MeasureType = 1
  OverTolerance = 0
  References2D = -> [ProjItem032]
  Rotation = 0
  ScaleType = 0
  TheoreticalExact = false
  Type = 1
  UnderTolerance = 0
  X = 15.1293
  Y = -3.91844
FEATURE [TechDraw::DrawViewDimension] Dimension137
  Arbitrary = false
  ArbitraryTolerances = false
  EqualTolerance = true
  FormatSpec = %.2f
  FormatSpecOverTolerance = %+.2f
  FormatSpecUnderTolerance = %+.2f
  Inverted = false
  LockPosition = false
  MeasureType = 1
  OverTolerance = 0
  References2D = -> [ProjItem032]
  Rotation = 0
  ScaleType = 0
  TheoreticalExact = false
  Type = 1
  UnderTolerance = 0
  X = -15.5
  Y = 4.31183
FEATURE [TechDraw::DrawViewDimension] Dimension138
  Arbitrary = false
  ArbitraryTolerances = false
  EqualTolerance = true
  FormatSpec = %.2f
  FormatSpecOverTolerance = %+.2f
  FormatSpecUnderTolerance = %+.2f
  Inverted = false
  LockPosition = false
  MeasureType = 1
  OverTolerance = 0
  References2D = -> [ProjItem032]
  Rotation = 0
  ScaleType = 0
  TheoreticalExact = false
  Type = 1
  UnderTolerance = 0
  X = 15.5323
  Y = 5.61825
FEATURE [TechDraw::DrawViewDimension] Dimension139
  Arbitrary = false
  ArbitraryTolerances = false
  EqualTolerance = true
  FormatSpec = %.2f
  FormatSpecOverTolerance = %+.2f
  FormatSpecUnderTolerance = %+.2f
  Inverted = false
  LockPosition = false
  MeasureType = 1
  OverTolerance = 0
  References2D = -> [ProjItem032]
  Rotation = 0
  ScaleType = 0
  TheoreticalExact = false
  Type = 1
  UnderTolerance = 0
  X = 48.6892
  Y = 8.8862
FEATURE [TechDraw::DrawViewDimension] Dimension140
  Arbitrary = false
  ArbitraryTolerances = false
  EqualTolerance = true
  FormatSpec = %.2f
  FormatSpecOverTolerance = %+.2f
  FormatSpecUnderTolerance = %+.2f
  Inverted = false
  LockPosition = false
  MeasureType = 1
  OverTolerance = 0
  References2D = -> [ProjItem032]
  Rotation = 0
  ScaleType = 0
  TheoreticalExact = false
  Type = 1
  UnderTolerance = 0
  X = -0.608868
  Y = 30.545
FEATURE [TechDraw::DrawViewDimension] Dimension141
  Arbitrary = false
  ArbitraryTolerances = false
  EqualTolerance = true
  FormatSpec = %.2f
  FormatSpecOverTolerance = %+.2f
  FormatSpecUnderTolerance = %+.2f
  Inverted = false
  LockPosition = false
  MeasureType = 1
  OverTolerance = 0
  References2D = -> [ProjItem032]
  Rotation = 0
  ScaleType = 0
  TheoreticalExact = false
  Type = 1
  UnderTolerance = 0
  X = -15.5
  Y = 16.1961
FEATURE [TechDraw::DrawViewDimension] Dimension142
  Arbitrary = false
  ArbitraryTolerances = false
  EqualTolerance = true
  FormatSpec = %.2f
  FormatSpecOverTolerance = %+.2f
  FormatSpecUnderTolerance = %+.2f
  Inverted = false
  LockPosition = false
  MeasureType = 1
  OverTolerance = 0
  References2D = -> [ProjItem032]
  Rotation = 0
  ScaleType = 0
  TheoreticalExact = false
  Type = 1
  UnderTolerance = 0
  X = 14.6613
  Y = 16.6316
FEATURE [TechDraw::DrawPage] Page005  label="Вся конструкция 1:4"
  KeepUpdated = true
  NextBalloonIndex = 1
  ProjectionType = 0
  Template = -> Template005
  Views = -> [ProjGroup014,Dimension126,Dimension133,Dimension135,Dimension136,Dimension137,Dimension138,Dimension139,Dimension140,Dimension141,Dimension142]
FEATURE [TechDraw::DrawSVGTemplate] Template006
  Height = 210
  Orientation = 1
  Width = 297
FEATURE [Part::FeaturePython] Clone010  label="Накладка002"  # Draft clone (typed FeaturePython)
  AttacherType = Attacher::AttachEngine3D
  Fuse = false
  Objects = -> [Body010]
  Placement = pos=(-395,-113.93,124.667) rot=(1,0,0;1.5708rad)
  Scale = (1,1,1)
FEATURE [App::DocumentObjectGroup] Group  label="Для чертежей"
  Group = -> [Clone008,Clone009,Clone010]
FEATURE [TechDraw::DrawProjGroupItem] ProjItem036  label="Front015"
  CoarseView = false
  Direction = (0,-1,0)
  Focus = 100
  HardHidden = false
  IsoCount = 0
  IsoHidden = false
  IsoVisible = false
  LockPosition = true
  Perspective = false
  Rotation = 0
  RotationVector = (1,0,0)
  ScaleType = 2
  SeamHidden = false
  SeamVisible = true
  SmoothHidden = false
  SmoothVisible = true
  Source = -> [Clone010]
  Type = 0
  X = 0
  XDirection = (1,0,0)
  Y = 0
FEATURE [TechDraw::DrawProjGroupItem] ProjItem037  label="FrontTopLeft005"
  CoarseView = false
  Direction = (-0.57735,-0.57735,0.57735)
  Focus = 100
  HardHidden = false
  IsoCount = 0
  IsoHidden = false
  IsoVisible = false
  LockPosition = false
  Perspective = false
  Rotation = 0
  RotationVector = (1,0,0)
  ScaleType = 2
  SeamHidden = false
  SeamVisible = true
  SmoothHidden = false
  SmoothVisible = true
  Source = -> [Clone010]
  Type = 6
  X = 126.543
  XDirection = (0.707107,-0.707107,0)
  Y = -1.65199
FEATURE [TechDraw::DrawProjGroup] ProjGroup015
  Anchor = -> ProjItem036
  AutoDistribute = false
  LockPosition = false
  ProjectionType = 0
  Rotation = 0
  ScaleType = 0
  Source = -> [Clone010]
  Views = -> [ProjItem036,ProjItem037]
  X = 85.1099
  Y = 138.158
  spacingX = 15
  spacingY = 15
FEATURE [TechDraw::DrawViewDimension] Dimension143
  Arbitrary = false
  ArbitraryTolerances = false
  EqualTolerance = true
  FormatSpec = %.2f
  FormatSpecOverTolerance = %+.2f
  FormatSpecUnderTolerance = %+.2f
  Inverted = false
  LockPosition = false
  MeasureType = 1
  OverTolerance = 0
  References2D = -> [ProjItem036]
  Rotation = 0
  ScaleType = 0
  TheoreticalExact = false
  Type = 2
  UnderTolerance = 0
  X = -44.1022
  Y = 0.325077
FEATURE [TechDraw::DrawViewDimension] Dimension144
  Arbitrary = false
  ArbitraryTolerances = false
  EqualTolerance = true
  FormatSpec = %.2f
  FormatSpecOverTolerance = %+.2f
  FormatSpecUnderTolerance = %+.2f
  Inverted = false
  LockPosition = false
  MeasureType = 1
  OverTolerance = 0
  References2D = -> [ProjItem036]
  Rotation = 0
  ScaleType = 0
  TheoreticalExact = false
  Type = 1
  UnderTolerance = 0
  X = 0
  Y = 52.5774
FEATURE [TechDraw::DrawViewDimension] Dimension145
  Arbitrary = false
  ArbitraryTolerances = false
  EqualTolerance = true
  FormatSpec = %.2f
  FormatSpecOverTolerance = %+.2f
  FormatSpecUnderTolerance = %+.2f
  Inverted = false
  LockPosition = false
  MeasureType = 1
  OverTolerance = 0
  References2D = -> [ProjItem036]
  Rotation = 0
  ScaleType = 0
  TheoreticalExact = false
  Type = 2
  UnderTolerance = 0
  X = -19.6401
  Y = 32.7257
FEATURE [TechDraw::DrawViewDimension] Dimension146
  Arbitrary = false
  ArbitraryTolerances = false
  EqualTolerance = true
  FormatSpec = %.2f
  FormatSpecOverTolerance = %+.2f
  FormatSpecUnderTolerance = %+.2f
  Inverted = false
  LockPosition = false
  MeasureType = 1
  OverTolerance = 0
  References2D = -> [ProjItem036]
  Rotation = 0
  ScaleType = 0
  TheoreticalExact = false
  Type = 2
  UnderTolerance = 0
  X = -19.4143
  Y = 14.9832
FEATURE [TechDraw::DrawViewDimension] Dimension147
  Arbitrary = false
  ArbitraryTolerances = false
  EqualTolerance = true
  FormatSpec = %.2f
  FormatSpecOverTolerance = %+.2f
  FormatSpecUnderTolerance = %+.2f
  Inverted = false
  LockPosition = false
  MeasureType = 1
  OverTolerance = 0
  References2D = -> [ProjItem036]
  Rotation = 0
  ScaleType = 0
  TheoreticalExact = false
  Type = 1
  UnderTolerance = 0
  X = 18.1772
  Y = -26.4874
FEATURE [TechDraw::DrawViewAnnotation] Annotation012
  Font = osifont
  LineSpace = 80
  LockPosition = false
  MaxWidth = -1
  Rotation = 0
  ScaleType = 0
  Text = \u041d\u0430\u043a\u043b\u0430\u0434\u043a\u0438 \u043d\u0430 \u043f\u0435\u0434\u0430\u043b\u0438 \u0438\u0437 \u0444\u043e\u043d\u0435\u0440\u044b 6\u043c\u043c
  TextSize = 5
  TextStyle = 0
  X = 88.0898
  Y = 60.5728
FEATURE [TechDraw::DrawPage] Page006  label="Накладки 1:1"
  KeepUpdated = true
  NextBalloonIndex = 1
  ProjectionType = 0
  Template = -> Template006
  Views = -> [ProjGroup015,Dimension143,Dimension144,Dimension145,Dimension146,Dimension147,Annotation012]
FEATURE [App::DocumentObjectGroup] ______________  label="Чертежи"
  Group = -> [Page001,Page,Page002,Page003,Page004,Page005,Page006]
note: 4 file-system paths scrubbed to <path> (originals preserved in the JSON sidecar)
